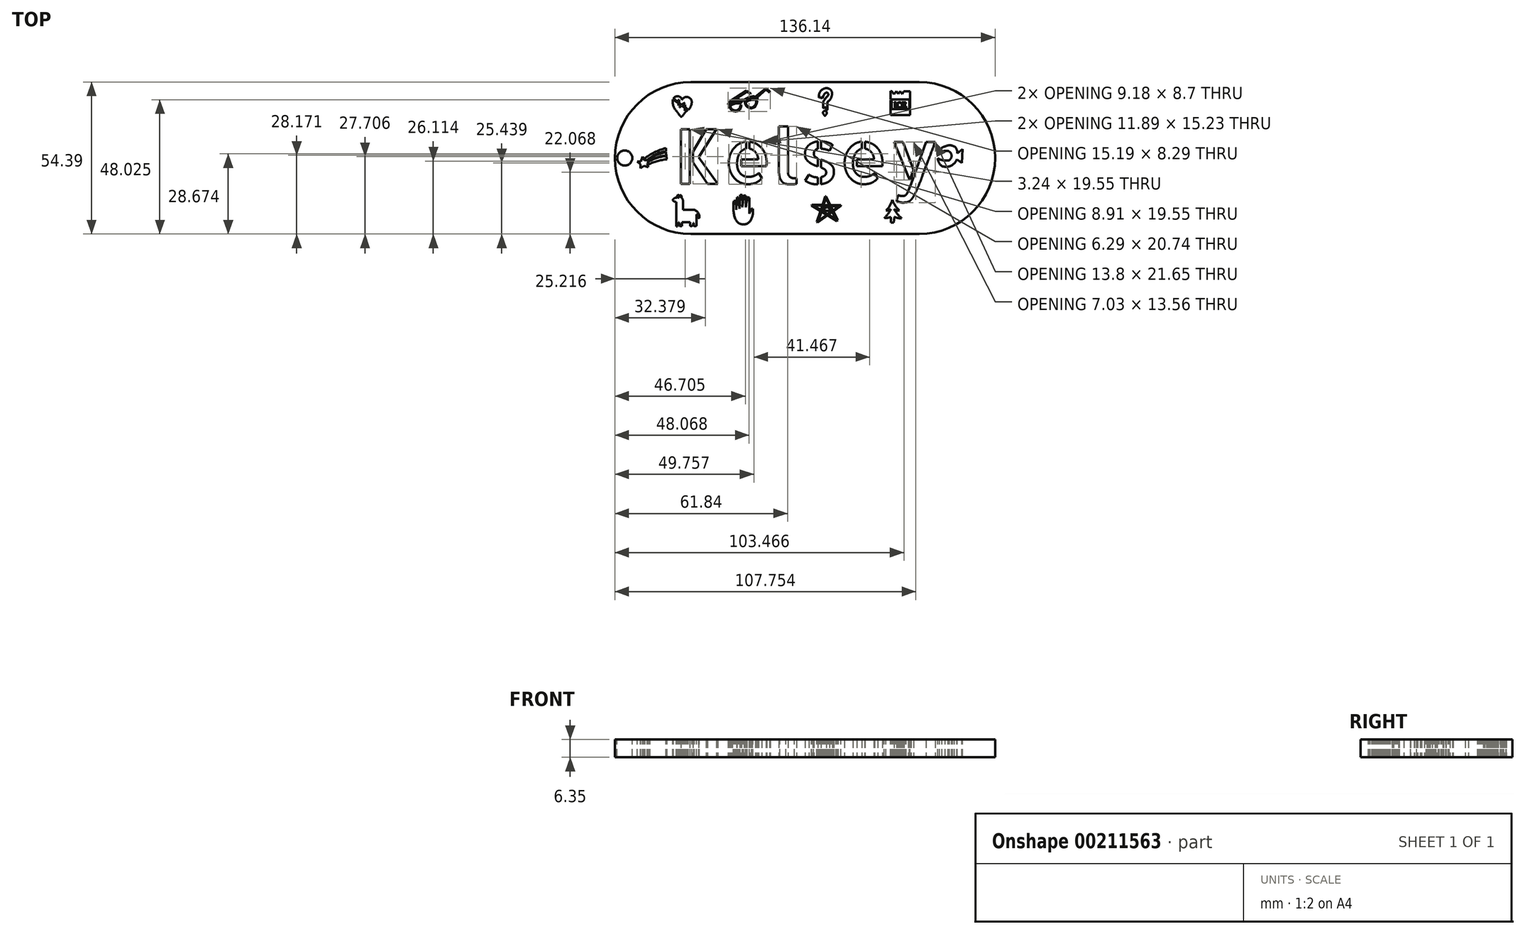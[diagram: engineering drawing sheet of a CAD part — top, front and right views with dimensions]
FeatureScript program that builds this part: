
annotation { "Feature Type Name" : "Feature", "Feature Type Description" : "" }
export const myFeature = defineFeature(function(context is Context, id is Id, definition is map)
    precondition{}
    {
        {
            var Q0;
            Q0=qCreatedBy(makeId("Top.planeOp"),FACE);
            var sketch = newSketch(context, id + "F0", { "sketchPlane" : qUnion([Q0])});
            skLineSegment(sketch, "E0", {"start": v(-66.68, 37.13) * mm, "end": v(15.06, 37.13) * mm});
            skLineSegment(sketch, "E1", {"start": v(15.06, -17.26) * mm, "end": v(-66.68, -17.26) * mm});
            skArc(sketch, "E2", {"start": v(15.06, -17.26) * mm, "mid": v(42.26, 9.93) * mm, "end": v(15.06, 37.13) * mm});
            skArc(sketch, "E3", {"start": v(-66.68, 37.13) * mm, "mid": v(-93.88, 9.93) * mm, "end": v(-66.68, -17.26) * mm});
            skText(sketch, "E4", { "text": "Kelsey", "fontName": "AllertaStencil-Regular.ttf"});
            const initialGuessF0  = {"E4": [-0.07275, 0.00067, 1, 0, 0.01956]};
            skSetInitialGuess(sketch, initialGuessF0);
            skSolve(sketch);
        }
        {
            var Q0;
            Q0=makeQuery(id+"F0.imprint","IMPRINT",FACE,{"disambiguationData":[TD([[makeQuery(id+"F0.imprint","IMPRINT",EDGE,{"derivedFrom":sQuery(id+"F0.wireOp",EDGE,"E0")}),-1.0]])]});
            var sketch = newSketch(context, id + "F1", { "sketchPlane" : qUnion([Q0])});
            skLineSegment(sketch, "E5", {"start": v(-45.3, 32.83) * mm, "end": v(-46.62, 33.7) * mm});
            skLineSegment(sketch, "E6", {"start": v(-46.62, 33.7) * mm, "end": v(-51.86, 30.42) * mm});
            skLineSegment(sketch, "E7", {"start": v(-42.97, 31.66) * mm, "end": v(-39.8, 34.47) * mm});
            skLineSegment(sketch, "E8", {"start": v(-39.8, 34.47) * mm, "end": v(-38.48, 33.25) * mm});
            skLineSegment(sketch, "E9", {"start": v(-38.48, 33.25) * mm, "end": v(-38.22, 33.53) * mm});
            skLineSegment(sketch, "E10", {"start": v(-38.22, 33.53) * mm, "end": v(-39.7, 34.91) * mm});
            skLineSegment(sketch, "E11", {"start": v(-39.7, 34.91) * mm, "end": v(-43.62, 31.93) * mm});
            skLineSegment(sketch, "E12", {"start": v(-45.3, 32.83) * mm, "end": v(-45.17, 33.02) * mm});
            skLineSegment(sketch, "E13", {"start": v(-45.17, 33.02) * mm, "end": v(-46.74, 34.05) * mm});
            skLineSegment(sketch, "E14", {"start": v(-46.74, 34.05) * mm, "end": v(-52.43, 30.37) * mm});
            skArc(sketch, "E15", {"start": v(-48.79, 30.65) * mm, "mid": v(-50.35, 30.92) * mm, "end": v(-51.86, 30.42) * mm});
            skArc(sketch, "E16", {"start": v(-47.64, 30.65) * mm, "mid": v(-48.21, 30.79) * mm, "end": v(-48.79, 30.65) * mm});
            skArc(sketch, "E17", {"start": v(-43.62, 31.93) * mm, "mid": v(-45.78, 31.76) * mm, "end": v(-47.64, 30.65) * mm});
            skArc(sketch, "E18", {"start": v(-42.76, 31.15) * mm, "mid": v(-42.81, 31.43) * mm, "end": v(-42.97, 31.66) * mm});
            skArc(sketch, "E19", {"start": v(-42.97, 31) * mm, "mid": v(-42.82, 31) * mm, "end": v(-42.76, 31.15) * mm});
            skArc(sketch, "E20", {"start": v(-43.62, 28.36) * mm, "mid": v(-43.12, 29.33) * mm, "end": v(-42.93, 30.4) * mm});
            skArc(sketch, "E21", {"start": v(-47.33, 29.92) * mm, "mid": v(-45.98, 27.92) * mm, "end": v(-43.62, 28.36) * mm});
            skArc(sketch, "E22", {"start": v(-47.64, 30.42) * mm, "mid": v(-48.15, 30.48) * mm, "end": v(-48.63, 30.28) * mm});
            skArc(sketch, "E23", {"start": v(-48.54, 29.74) * mm, "mid": v(-48.5, 30.02) * mm, "end": v(-48.63, 30.28) * mm});
            skArc(sketch, "E24", {"start": v(-48.79, 29.74) * mm, "mid": v(-48.66, 29.7) * mm, "end": v(-48.54, 29.74) * mm});
            skArc(sketch, "E25", {"start": v(-49.16, 27.17) * mm, "mid": v(-48.75, 28.02) * mm, "end": v(-48.64, 28.97) * mm});
            skArc(sketch, "E26", {"start": v(-52.24, 27.17) * mm, "mid": v(-50.7, 26.62) * mm, "end": v(-49.16, 27.17) * mm});
            skArc(sketch, "E27", {"start": v(-52.92, 28.67) * mm, "mid": v(-52.72, 27.86) * mm, "end": v(-52.24, 27.17) * mm});
            skArc(sketch, "E28", {"start": v(-52.43, 30.37) * mm, "mid": v(-53.02, 29.83) * mm, "end": v(-53.4, 29.12) * mm});
            skArc(sketch, "E29", {"start": v(-49.04, 29.93) * mm, "mid": v(-51.02, 29.83) * mm, "end": v(-52.82, 29) * mm});
            skArc(sketch, "E30", {"start": v(-49.04, 30.37) * mm, "mid": v(-51.17, 30.39) * mm, "end": v(-53.09, 29.45) * mm});
            skArc(sketch, "E31", {"start": v(-49.04, 29.93) * mm, "mid": v(-48.87, 30.15) * mm, "end": v(-49.04, 30.37) * mm});
            skArc(sketch, "E32", {"start": v(-49.04, 29.5) * mm, "mid": v(-50.88, 29.42) * mm, "end": v(-52.57, 28.67) * mm});
            skArc(sketch, "E33", {"start": v(-50.3, 26.99) * mm, "mid": v(-49.3, 27.71) * mm, "end": v(-48.92, 28.9) * mm});
            skArc(sketch, "E34", {"start": v(-52.57, 28.67) * mm, "mid": v(-51.8, 27.32) * mm, "end": v(-50.3, 26.99) * mm});
            skArc(sketch, "E35", {"start": v(-43.15, 31.48) * mm, "mid": v(-45.32, 31.48) * mm, "end": v(-47.33, 30.65) * mm});
            skArc(sketch, "E36", {"start": v(-43.2, 31.13) * mm, "mid": v(-45.25, 31.05) * mm, "end": v(-47.18, 30.36) * mm});
            skArc(sketch, "E37", {"start": v(-43.2, 31.13) * mm, "mid": v(-43.09, 31.3) * mm, "end": v(-43.15, 31.48) * mm});
            skArc(sketch, "E38", {"start": v(-47.33, 30.65) * mm, "mid": v(-47.35, 30.56) * mm, "end": v(-47.33, 30.47) * mm});
            skArc(sketch, "E39", {"start": v(-43.49, 30.82) * mm, "mid": v(-45.32, 30.67) * mm, "end": v(-47.03, 29.96) * mm});
            skArc(sketch, "E40", {"start": v(-44.66, 28.06) * mm, "mid": v(-43.62, 28.96) * mm, "end": v(-43.35, 30.32) * mm});
            skArc(sketch, "E41", {"start": v(-47.03, 29.96) * mm, "mid": v(-46.3, 28.44) * mm, "end": v(-44.66, 28.06) * mm});
            skLineSegment(sketch, "E42", {"start": v(-52.82, 29) * mm, "end": v(-52.92, 28.67) * mm});
            skLineSegment(sketch, "E43", {"start": v(-53.09, 29.45) * mm, "end": v(-53.4, 29.12) * mm});
            skPoint(sketch, "E44.center.orphan", {"position": v(-52.82, 29.26) * mm});
            skLineSegment(sketch, "E45", {"start": v(-47.33, 29.92) * mm, "end": v(-47.18, 30.36) * mm});
            skLineSegment(sketch, "E46", {"start": v(-47.64, 30.42) * mm, "end": v(-47.33, 30.47) * mm});
            skPoint(sketch, "E46.endSnap0", {"position": v(-47.33, 30.47) * mm});
            skLineSegment(sketch, "E47", {"start": v(-49.04, 29.5) * mm, "end": v(-48.72, 29.5) * mm});
            skLineSegment(sketch, "E48", {"start": v(-48.92, 28.9) * mm, "end": v(-48.64, 28.97) * mm});
            skLineSegment(sketch, "E49", {"start": v(-43.43, 30.66) * mm, "end": v(-42.94, 30.8) * mm});
            skLineSegment(sketch, "E50", {"start": v(-43.35, 30.32) * mm, "end": v(-42.93, 30.4) * mm});
            skArc(sketch, "E51.trimOffspring", {"start": v(-42.94, 30.8) * mm, "mid": v(-42.95, 30.9) * mm, "end": v(-42.97, 31) * mm});
            skArc(sketch, "E52.trimOffspring", {"start": v(-43.43, 30.66) * mm, "mid": v(-43.46, 30.74) * mm, "end": v(-43.49, 30.82) * mm});
            skArc(sketch, "E53.trimOffspring", {"start": v(-48.72, 29.5) * mm, "mid": v(-48.75, 29.63) * mm, "end": v(-48.79, 29.74) * mm});
            skLineSegment(sketch, "E54", {"start": v(-47.33, 30.47) * mm, "end": v(-47.33, 30.47) * mm});
            skSolve(sketch);
        }
        {
            var Q0;
            Q0 = qSketchRegion(id + "F0", true);
            extrude(context, id + "F2", {"entities" : qUnion([Q0]), "depth" : 6.35 * mm});
        }
        {
            var Q0;
            Q0 = qSketchRegion(id + "F1", true);
            extrude(context, id + "F3", {"entities" : qUnion([Q0]), "operationType" : NewBodyOperationType.REMOVE, "endBound" : BoundingType.THROUGH_ALL, "depth" : 25.4 * mm});
        }
        {
            var Q0;
            Q0=makeQuery(id+"F2.opExtrude","CAP_FACE",FACE,{"disambiguationData":[OSD([sQuery(id+"F0.wireOp",EDGE,"E0"),sQuery(id+"F0.wireOp",EDGE,"E1"),sQuery(id+"F0.wireOp",EDGE,"E2"),sQuery(id+"F0.wireOp",EDGE,"E3"),sQuery(id+"F0.wireOp",EDGE,"E4.sketch_text.stroke-0"),sQuery(id+"F0.wireOp",EDGE,"E4.sketch_text.stroke-1"),sQuery(id+"F0.wireOp",EDGE,"E4.sketch_text.stroke-2"),sQuery(id+"F0.wireOp",EDGE,"E4.sketch_text.stroke-3"),sQuery(id+"F0.wireOp",EDGE,"E4.sketch_text.stroke-4"),sQuery(id+"F0.wireOp",EDGE,"E4.sketch_text.stroke-5"),sQuery(id+"F0.wireOp",EDGE,"E4.sketch_text.stroke-6"),sQuery(id+"F0.wireOp",EDGE,"E4.sketch_text.stroke-7"),sQuery(id+"F0.wireOp",EDGE,"E4.sketch_text.stroke-8"),sQuery(id+"F0.wireOp",EDGE,"E4.sketch_text.stroke-9"),sQuery(id+"F0.wireOp",EDGE,"E4.sketch_text.stroke-10"),sQuery(id+"F0.wireOp",EDGE,"E4.sketch_text.stroke-11"),sQuery(id+"F0.wireOp",EDGE,"E4.sketch_text.stroke-12"),sQuery(id+"F0.wireOp",EDGE,"E4.sketch_text.stroke-13"),sQuery(id+"F0.wireOp",EDGE,"E4.sketch_text.stroke-14"),sQuery(id+"F0.wireOp",EDGE,"E4.sketch_text.stroke-15"),sQuery(id+"F0.wireOp",EDGE,"E4.sketch_text.stroke-16"),sQuery(id+"F0.wireOp",EDGE,"E4.sketch_text.stroke-17"),sQuery(id+"F0.wireOp",EDGE,"E4.sketch_text.stroke-18"),sQuery(id+"F0.wireOp",EDGE,"E4.sketch_text.stroke-19"),sQuery(id+"F0.wireOp",EDGE,"E4.sketch_text.stroke-20"),sQuery(id+"F0.wireOp",EDGE,"E4.sketch_text.stroke-21"),sQuery(id+"F0.wireOp",EDGE,"E4.sketch_text.stroke-22"),sQuery(id+"F0.wireOp",EDGE,"E4.sketch_text.stroke-23"),sQuery(id+"F0.wireOp",EDGE,"E4.sketch_text.stroke-24"),sQuery(id+"F0.wireOp",EDGE,"E4.sketch_text.stroke-25"),sQuery(id+"F0.wireOp",EDGE,"E4.sketch_text.stroke-26"),sQuery(id+"F0.wireOp",EDGE,"E4.sketch_text.stroke-27"),sQuery(id+"F0.wireOp",EDGE,"E4.sketch_text.stroke-28"),sQuery(id+"F0.wireOp",EDGE,"E4.sketch_text.stroke-29"),sQuery(id+"F0.wireOp",EDGE,"E4.sketch_text.stroke-30"),sQuery(id+"F0.wireOp",EDGE,"E4.sketch_text.stroke-31"),sQuery(id+"F0.wireOp",EDGE,"E4.sketch_text.stroke-32"),sQuery(id+"F0.wireOp",EDGE,"E4.sketch_text.stroke-33"),sQuery(id+"F0.wireOp",EDGE,"E4.sketch_text.stroke-34"),sQuery(id+"F0.wireOp",EDGE,"E4.sketch_text.stroke-35"),sQuery(id+"F0.wireOp",EDGE,"E4.sketch_text.stroke-36"),sQuery(id+"F0.wireOp",EDGE,"E4.sketch_text.stroke-37"),sQuery(id+"F0.wireOp",EDGE,"E4.sketch_text.stroke-38"),sQuery(id+"F0.wireOp",EDGE,"E4.sketch_text.stroke-39"),sQuery(id+"F0.wireOp",EDGE,"E4.sketch_text.stroke-40"),sQuery(id+"F0.wireOp",EDGE,"E4.sketch_text.stroke-41"),sQuery(id+"F0.wireOp",EDGE,"E4.sketch_text.stroke-42"),sQuery(id+"F0.wireOp",EDGE,"E4.sketch_text.stroke-43"),sQuery(id+"F0.wireOp",EDGE,"E4.sketch_text.stroke-44"),sQuery(id+"F0.wireOp",EDGE,"E4.sketch_text.stroke-45"),sQuery(id+"F0.wireOp",EDGE,"E4.sketch_text.stroke-46"),sQuery(id+"F0.wireOp",EDGE,"E4.sketch_text.stroke-47"),sQuery(id+"F0.wireOp",EDGE,"E4.sketch_text.stroke-48"),sQuery(id+"F0.wireOp",EDGE,"E4.sketch_text.stroke-49"),sQuery(id+"F0.wireOp",EDGE,"E4.sketch_text.stroke-50"),sQuery(id+"F0.wireOp",EDGE,"E4.sketch_text.stroke-51"),sQuery(id+"F0.wireOp",EDGE,"E4.sketch_text.stroke-52"),sQuery(id+"F0.wireOp",EDGE,"E4.sketch_text.stroke-53"),sQuery(id+"F0.wireOp",EDGE,"E4.sketch_text.stroke-54"),sQuery(id+"F0.wireOp",EDGE,"E4.sketch_text.stroke-55"),sQuery(id+"F0.wireOp",EDGE,"E4.sketch_text.stroke-56"),sQuery(id+"F0.wireOp",EDGE,"E4.sketch_text.stroke-57"),sQuery(id+"F0.wireOp",EDGE,"E4.sketch_text.stroke-58"),sQuery(id+"F0.wireOp",EDGE,"E4.sketch_text.stroke-59"),sQuery(id+"F0.wireOp",EDGE,"E4.sketch_text.stroke-60"),sQuery(id+"F0.wireOp",EDGE,"E4.sketch_text.stroke-61"),sQuery(id+"F0.wireOp",EDGE,"E4.sketch_text.stroke-62"),sQuery(id+"F0.wireOp",EDGE,"E4.sketch_text.stroke-63"),sQuery(id+"F0.wireOp",EDGE,"E4.sketch_text.stroke-64"),sQuery(id+"F0.wireOp",EDGE,"E4.sketch_text.stroke-65"),sQuery(id+"F0.wireOp",EDGE,"E4.sketch_text.stroke-66"),sQuery(id+"F0.wireOp",EDGE,"E4.sketch_text.stroke-67"),sQuery(id+"F0.wireOp",EDGE,"E4.sketch_text.stroke-68"),sQuery(id+"F0.wireOp",EDGE,"E4.sketch_text.stroke-69"),sQuery(id+"F0.wireOp",EDGE,"E4.sketch_text.stroke-70"),sQuery(id+"F0.wireOp",EDGE,"E4.sketch_text.stroke-71"),sQuery(id+"F0.wireOp",EDGE,"E4.sketch_text.stroke-72"),sQuery(id+"F0.wireOp",EDGE,"E4.sketch_text.stroke-73"),sQuery(id+"F0.wireOp",EDGE,"E4.sketch_text.stroke-74"),sQuery(id+"F0.wireOp",EDGE,"E4.sketch_text.stroke-75"),sQuery(id+"F0.wireOp",EDGE,"E4.sketch_text.stroke-76"),sQuery(id+"F0.wireOp",EDGE,"E4.sketch_text.stroke-77"),sQuery(id+"F0.wireOp",EDGE,"E4.sketch_text.stroke-78"),sQuery(id+"F0.wireOp",EDGE,"E4.sketch_text.stroke-79"),sQuery(id+"F0.wireOp",EDGE,"E4.sketch_text.stroke-80"),sQuery(id+"F0.wireOp",EDGE,"E4.sketch_text.stroke-81"),sQuery(id+"F0.wireOp",EDGE,"E4.sketch_text.stroke-82"),sQuery(id+"F0.wireOp",EDGE,"E4.sketch_text.stroke-83"),sQuery(id+"F0.wireOp",EDGE,"E4.sketch_text.stroke-84"),sQuery(id+"F0.wireOp",EDGE,"E4.sketch_text.stroke-85"),sQuery(id+"F0.wireOp",EDGE,"E4.sketch_text.stroke-86"),sQuery(id+"F0.wireOp",EDGE,"E4.sketch_text.stroke-87"),sQuery(id+"F0.wireOp",EDGE,"E4.sketch_text.stroke-88"),sQuery(id+"F0.wireOp",EDGE,"E4.sketch_text.stroke-89"),sQuery(id+"F0.wireOp",EDGE,"E4.sketch_text.stroke-90"),sQuery(id+"F0.wireOp",EDGE,"E4.sketch_text.stroke-91"),sQuery(id+"F0.wireOp",EDGE,"E4.sketch_text.stroke-92"),sQuery(id+"F0.wireOp",EDGE,"E4.sketch_text.stroke-93"),sQuery(id+"F0.wireOp",EDGE,"E4.sketch_text.stroke-94"),sQuery(id+"F0.wireOp",EDGE,"E4.sketch_text.stroke-95"),sQuery(id+"F0.wireOp",EDGE,"E4.sketch_text.stroke-96"),sQuery(id+"F0.wireOp",EDGE,"E4.sketch_text.stroke-97"),sQuery(id+"F0.wireOp",EDGE,"E4.sketch_text.stroke-98"),sQuery(id+"F0.wireOp",EDGE,"E4.sketch_text.stroke-99"),sQuery(id+"F0.wireOp",EDGE,"E4.sketch_text.stroke-100"),sQuery(id+"F0.wireOp",EDGE,"E4.sketch_text.stroke-101"),sQuery(id+"F0.wireOp",EDGE,"E4.sketch_text.stroke-102"),sQuery(id+"F0.wireOp",EDGE,"E4.sketch_text.stroke-103"),sQuery(id+"F0.wireOp",EDGE,"E4.sketch_text.stroke-104"),sQuery(id+"F0.wireOp",EDGE,"E4.sketch_text.stroke-105"),sQuery(id+"F0.wireOp",EDGE,"E4.sketch_text.stroke-106"),sQuery(id+"F0.wireOp",EDGE,"E4.sketch_text.stroke-107"),sQuery(id+"F0.wireOp",EDGE,"E4.sketch_text.stroke-108"),sQuery(id+"F0.wireOp",EDGE,"E4.sketch_text.stroke-109"),sQuery(id+"F0.wireOp",EDGE,"E4.sketch_text.stroke-110"),sQuery(id+"F0.wireOp",EDGE,"E4.sketch_text.stroke-111"),sQuery(id+"F0.wireOp",EDGE,"E4.sketch_text.stroke-112"),sQuery(id+"F0.wireOp",EDGE,"E4.sketch_text.stroke-113"),sQuery(id+"F0.wireOp",EDGE,"E4.sketch_text.stroke-114"),sQuery(id+"F0.wireOp",EDGE,"E4.sketch_text.stroke-115"),sQuery(id+"F0.wireOp",EDGE,"E4.sketch_text.stroke-116"),sQuery(id+"F0.wireOp",EDGE,"E4.sketch_text.stroke-117"),sQuery(id+"F0.wireOp",EDGE,"E4.sketch_text.stroke-118"),sQuery(id+"F0.wireOp",EDGE,"E4.sketch_text.stroke-119"),sQuery(id+"F0.wireOp",EDGE,"E4.sketch_text.stroke-120"),sQuery(id+"F0.wireOp",EDGE,"E4.sketch_text.stroke-121"),sQuery(id+"F0.wireOp",EDGE,"E4.sketch_text.stroke-122"),sQuery(id+"F0.wireOp",EDGE,"E4.sketch_text.stroke-123"),sQuery(id+"F0.wireOp",EDGE,"E4.sketch_text.stroke-124"),sQuery(id+"F0.wireOp",EDGE,"E4.sketch_text.stroke-125"),sQuery(id+"F0.wireOp",EDGE,"E4.sketch_text.stroke-126"),sQuery(id+"F0.wireOp",EDGE,"E4.sketch_text.stroke-127"),sQuery(id+"F0.wireOp",EDGE,"E4.sketch_text.stroke-128"),sQuery(id+"F0.wireOp",EDGE,"E4.sketch_text.stroke-129"),sQuery(id+"F0.wireOp",EDGE,"E4.sketch_text.stroke-130"),sQuery(id+"F0.wireOp",EDGE,"E4.sketch_text.stroke-131"),sQuery(id+"F0.wireOp",EDGE,"E4.sketch_text.stroke-132"),sQuery(id+"F0.wireOp",EDGE,"E4.sketch_text.stroke-133"),sQuery(id+"F0.wireOp",EDGE,"E4.sketch_text.stroke-134"),sQuery(id+"F0.wireOp",EDGE,"E4.sketch_text.stroke-135"),sQuery(id+"F0.wireOp",EDGE,"E4.sketch_text.stroke-136"),sQuery(id+"F0.wireOp",EDGE,"E4.sketch_text.stroke-137"),sQuery(id+"F0.wireOp",EDGE,"E4.sketch_text.stroke-138"),sQuery(id+"F0.wireOp",EDGE,"E4.sketch_text.stroke-139"),sQuery(id+"F0.wireOp",EDGE,"E4.sketch_text.stroke-140"),sQuery(id+"F0.wireOp",EDGE,"E4.sketch_text.stroke-141"),sQuery(id+"F0.wireOp",EDGE,"E4.sketch_text.stroke-142"),sQuery(id+"F0.wireOp",EDGE,"E4.sketch_text.stroke-143"),sQuery(id+"F0.wireOp",EDGE,"E4.sketch_text.stroke-144"),sQuery(id+"F0.wireOp",EDGE,"E4.sketch_text.stroke-145"),sQuery(id+"F0.wireOp",EDGE,"E4.sketch_text.stroke-146"),sQuery(id+"F0.wireOp",EDGE,"E4.sketch_text.stroke-147"),sQuery(id+"F0.wireOp",EDGE,"E4.sketch_text.stroke-148"),sQuery(id+"F0.wireOp",EDGE,"E4.sketch_text.stroke-149"),sQuery(id+"F0.wireOp",EDGE,"E4.sketch_text.stroke-150"),sQuery(id+"F0.wireOp",EDGE,"E4.sketch_text.stroke-151"),sQuery(id+"F0.wireOp",EDGE,"E4.sketch_text.stroke-152"),sQuery(id+"F0.wireOp",EDGE,"E4.sketch_text.stroke-153"),sQuery(id+"F0.wireOp",EDGE,"E4.sketch_text.stroke-154"),sQuery(id+"F0.wireOp",EDGE,"E4.sketch_text.stroke-155"),sQuery(id+"F0.wireOp",EDGE,"E4.sketch_text.stroke-156"),sQuery(id+"F0.wireOp",EDGE,"E4.sketch_text.stroke-157"),sQuery(id+"F0.wireOp",EDGE,"E4.sketch_text.stroke-158"),sQuery(id+"F0.wireOp",EDGE,"E4.sketch_text.stroke-159"),sQuery(id+"F0.wireOp",EDGE,"E4.sketch_text.stroke-160"),sQuery(id+"F0.wireOp",EDGE,"E4.sketch_text.stroke-161"),sQuery(id+"F0.wireOp",EDGE,"E4.sketch_text.stroke-162"),sQuery(id+"F0.wireOp",EDGE,"E4.sketch_text.stroke-163"),sQuery(id+"F0.wireOp",EDGE,"E4.sketch_text.stroke-164"),sQuery(id+"F0.wireOp",EDGE,"E4.sketch_text.stroke-165"),sQuery(id+"F0.wireOp",EDGE,"E4.sketch_text.stroke-166"),sQuery(id+"F0.wireOp",EDGE,"E4.sketch_text.stroke-167"),sQuery(id+"F0.wireOp",EDGE,"E4.sketch_text.stroke-168"),sQuery(id+"F0.wireOp",EDGE,"E4.sketch_text.stroke-169"),sQuery(id+"F0.wireOp",EDGE,"E4.sketch_text.stroke-170"),sQuery(id+"F0.wireOp",EDGE,"E4.sketch_text.stroke-171"),sQuery(id+"F0.wireOp",EDGE,"E4.sketch_text.stroke-172"),sQuery(id+"F0.wireOp",EDGE,"E4.sketch_text.stroke-173"),sQuery(id+"F0.wireOp",EDGE,"E4.sketch_text.stroke-174")])],"isStart":false});
            var sketch = newSketch(context, id + "F4", { "sketchPlane" : qUnion([Q0])});
            skArc(sketch, "E55", {"start": v(-18.14, 33.41) * mm, "mid": v(-19.07, 32.53) * mm, "end": v(-19.44, 31.3) * mm});
            skArc(sketch, "E56", {"start": v(-17.69, 32.15) * mm, "mid": v(-17.5, 32.93) * mm, "end": v(-18.14, 33.41) * mm});
            skArc(sketch, "E57", {"start": v(-17.69, 32.15) * mm, "mid": v(-18.57, 31.14) * mm, "end": v(-19.3, 30.01) * mm});
            skArc(sketch, "E58", {"start": v(-17.8, 29.97) * mm, "mid": v(-16.6, 31.21) * mm, "end": v(-16.17, 32.89) * mm});
            skArc(sketch, "E59", {"start": v(-16.17, 32.89) * mm, "mid": v(-16.42, 34.06) * mm, "end": v(-17.36, 34.8) * mm});
            skArc(sketch, "E60", {"start": v(-17.36, 34.8) * mm, "mid": v(-18.92, 34.83) * mm, "end": v(-20.18, 33.93) * mm});
            skArc(sketch, "E61", {"start": v(-20.18, 33.93) * mm, "mid": v(-20.77, 32.8) * mm, "end": v(-20.82, 31.52) * mm});
            skArc(sketch, "E62", {"start": v(-18.03, 26.21) * mm, "mid": v(-18.78, 26.8) * mm, "end": v(-19.39, 26.06) * mm});
            skArc(sketch, "E63", {"start": v(-18.4, 25.51) * mm, "mid": v(-18.07, 25.78) * mm, "end": v(-18.03, 26.21) * mm});
            skArc(sketch, "E64", {"start": v(-19.39, 26.06) * mm, "mid": v(-19.25, 25.72) * mm, "end": v(-18.93, 25.53) * mm});
            skArc(sketch, "E65", {"start": v(-18.93, 25.53) * mm, "mid": v(-18.9, 25.23) * mm, "end": v(-18.69, 25.02) * mm});
            skArc(sketch, "E66", {"start": v(-18.69, 25.02) * mm, "mid": v(-18.44, 25.2) * mm, "end": v(-18.4, 25.51) * mm});
            skLineSegment(sketch, "E67", {"start": v(-17.8, 29.97) * mm, "end": v(-17.8, 27.46) * mm});
            skLineSegment(sketch, "E68", {"start": v(-19.3, 30.01) * mm, "end": v(-19.3, 28.05) * mm});
            skArc(sketch, "E69", {"start": v(-19.8, 31.96) * mm, "mid": v(-19.68, 31.6) * mm, "end": v(-19.44, 31.3) * mm});
            skArc(sketch, "E70", {"start": v(-20.07, 31.3) * mm, "mid": v(-19.85, 31.6) * mm, "end": v(-19.8, 31.96) * mm});
            skArc(sketch, "E71", {"start": v(-20.39, 31.96) * mm, "mid": v(-20.3, 31.6) * mm, "end": v(-20.07, 31.3) * mm});
            skArc(sketch, "E72", {"start": v(-20.82, 31.52) * mm, "mid": v(-20.55, 31.69) * mm, "end": v(-20.39, 31.96) * mm});
            skArc(sketch, "E73", {"start": v(-18.94, 28.2) * mm, "mid": v(-18.86, 28.02) * mm, "end": v(-18.7, 27.9) * mm});
            skArc(sketch, "E74", {"start": v(-18.7, 27.9) * mm, "mid": v(-18.48, 28.15) * mm, "end": v(-18.39, 28.47) * mm});
            skArc(sketch, "E75", {"start": v(-18.39, 28.47) * mm, "mid": v(-18.36, 27.7) * mm, "end": v(-18.06, 27) * mm});
            skArc(sketch, "E76", {"start": v(-18.06, 27) * mm, "mid": v(-17.87, 27.2) * mm, "end": v(-17.8, 27.46) * mm});
            skArc(sketch, "E77", {"start": v(-19.3, 28.05) * mm, "mid": v(-19.27, 27.87) * mm, "end": v(-19.19, 27.7) * mm});
            skArc(sketch, "E78", {"start": v(-19.19, 27.7) * mm, "mid": v(-19.03, 27.94) * mm, "end": v(-18.94, 28.2) * mm});
            skPoint(sketch, "E79", {"position": v(-18.94, 28.2) * mm});
            skSolve(sketch);
        }
        {
            var Q0;
            Q0 = qSketchRegion(id + "F4", true);
            extrude(context, id + "F5", {"entities" : qUnion([Q0]), "operationType" : NewBodyOperationType.REMOVE, "endBound" : BoundingType.THROUGH_ALL, "oppositeDirection" : true, "depth" : 25.4 * mm});
        }
        {
            var Q0;
            Q0=makeQuery(id+"F2.opExtrude","CAP_FACE",FACE,{"disambiguationData":[OSD([sQuery(id+"F0.wireOp",EDGE,"E0"),sQuery(id+"F0.wireOp",EDGE,"E1"),sQuery(id+"F0.wireOp",EDGE,"E2"),sQuery(id+"F0.wireOp",EDGE,"E3"),sQuery(id+"F0.wireOp",EDGE,"E4.sketch_text.stroke-0"),sQuery(id+"F0.wireOp",EDGE,"E4.sketch_text.stroke-1"),sQuery(id+"F0.wireOp",EDGE,"E4.sketch_text.stroke-2"),sQuery(id+"F0.wireOp",EDGE,"E4.sketch_text.stroke-3"),sQuery(id+"F0.wireOp",EDGE,"E4.sketch_text.stroke-4"),sQuery(id+"F0.wireOp",EDGE,"E4.sketch_text.stroke-5"),sQuery(id+"F0.wireOp",EDGE,"E4.sketch_text.stroke-6"),sQuery(id+"F0.wireOp",EDGE,"E4.sketch_text.stroke-7"),sQuery(id+"F0.wireOp",EDGE,"E4.sketch_text.stroke-8"),sQuery(id+"F0.wireOp",EDGE,"E4.sketch_text.stroke-9"),sQuery(id+"F0.wireOp",EDGE,"E4.sketch_text.stroke-10"),sQuery(id+"F0.wireOp",EDGE,"E4.sketch_text.stroke-11"),sQuery(id+"F0.wireOp",EDGE,"E4.sketch_text.stroke-12"),sQuery(id+"F0.wireOp",EDGE,"E4.sketch_text.stroke-13"),sQuery(id+"F0.wireOp",EDGE,"E4.sketch_text.stroke-14"),sQuery(id+"F0.wireOp",EDGE,"E4.sketch_text.stroke-15"),sQuery(id+"F0.wireOp",EDGE,"E4.sketch_text.stroke-16"),sQuery(id+"F0.wireOp",EDGE,"E4.sketch_text.stroke-17"),sQuery(id+"F0.wireOp",EDGE,"E4.sketch_text.stroke-18"),sQuery(id+"F0.wireOp",EDGE,"E4.sketch_text.stroke-19"),sQuery(id+"F0.wireOp",EDGE,"E4.sketch_text.stroke-20"),sQuery(id+"F0.wireOp",EDGE,"E4.sketch_text.stroke-21"),sQuery(id+"F0.wireOp",EDGE,"E4.sketch_text.stroke-22"),sQuery(id+"F0.wireOp",EDGE,"E4.sketch_text.stroke-23"),sQuery(id+"F0.wireOp",EDGE,"E4.sketch_text.stroke-24"),sQuery(id+"F0.wireOp",EDGE,"E4.sketch_text.stroke-25"),sQuery(id+"F0.wireOp",EDGE,"E4.sketch_text.stroke-26"),sQuery(id+"F0.wireOp",EDGE,"E4.sketch_text.stroke-27"),sQuery(id+"F0.wireOp",EDGE,"E4.sketch_text.stroke-28"),sQuery(id+"F0.wireOp",EDGE,"E4.sketch_text.stroke-29"),sQuery(id+"F0.wireOp",EDGE,"E4.sketch_text.stroke-30"),sQuery(id+"F0.wireOp",EDGE,"E4.sketch_text.stroke-31"),sQuery(id+"F0.wireOp",EDGE,"E4.sketch_text.stroke-32"),sQuery(id+"F0.wireOp",EDGE,"E4.sketch_text.stroke-33"),sQuery(id+"F0.wireOp",EDGE,"E4.sketch_text.stroke-34"),sQuery(id+"F0.wireOp",EDGE,"E4.sketch_text.stroke-35"),sQuery(id+"F0.wireOp",EDGE,"E4.sketch_text.stroke-36"),sQuery(id+"F0.wireOp",EDGE,"E4.sketch_text.stroke-37"),sQuery(id+"F0.wireOp",EDGE,"E4.sketch_text.stroke-38"),sQuery(id+"F0.wireOp",EDGE,"E4.sketch_text.stroke-39"),sQuery(id+"F0.wireOp",EDGE,"E4.sketch_text.stroke-40"),sQuery(id+"F0.wireOp",EDGE,"E4.sketch_text.stroke-41"),sQuery(id+"F0.wireOp",EDGE,"E4.sketch_text.stroke-42"),sQuery(id+"F0.wireOp",EDGE,"E4.sketch_text.stroke-43"),sQuery(id+"F0.wireOp",EDGE,"E4.sketch_text.stroke-44"),sQuery(id+"F0.wireOp",EDGE,"E4.sketch_text.stroke-45"),sQuery(id+"F0.wireOp",EDGE,"E4.sketch_text.stroke-46"),sQuery(id+"F0.wireOp",EDGE,"E4.sketch_text.stroke-47"),sQuery(id+"F0.wireOp",EDGE,"E4.sketch_text.stroke-48"),sQuery(id+"F0.wireOp",EDGE,"E4.sketch_text.stroke-49"),sQuery(id+"F0.wireOp",EDGE,"E4.sketch_text.stroke-50"),sQuery(id+"F0.wireOp",EDGE,"E4.sketch_text.stroke-51"),sQuery(id+"F0.wireOp",EDGE,"E4.sketch_text.stroke-52"),sQuery(id+"F0.wireOp",EDGE,"E4.sketch_text.stroke-53"),sQuery(id+"F0.wireOp",EDGE,"E4.sketch_text.stroke-54"),sQuery(id+"F0.wireOp",EDGE,"E4.sketch_text.stroke-55"),sQuery(id+"F0.wireOp",EDGE,"E4.sketch_text.stroke-56"),sQuery(id+"F0.wireOp",EDGE,"E4.sketch_text.stroke-57"),sQuery(id+"F0.wireOp",EDGE,"E4.sketch_text.stroke-58"),sQuery(id+"F0.wireOp",EDGE,"E4.sketch_text.stroke-59"),sQuery(id+"F0.wireOp",EDGE,"E4.sketch_text.stroke-60"),sQuery(id+"F0.wireOp",EDGE,"E4.sketch_text.stroke-61"),sQuery(id+"F0.wireOp",EDGE,"E4.sketch_text.stroke-62"),sQuery(id+"F0.wireOp",EDGE,"E4.sketch_text.stroke-63"),sQuery(id+"F0.wireOp",EDGE,"E4.sketch_text.stroke-64"),sQuery(id+"F0.wireOp",EDGE,"E4.sketch_text.stroke-65"),sQuery(id+"F0.wireOp",EDGE,"E4.sketch_text.stroke-66"),sQuery(id+"F0.wireOp",EDGE,"E4.sketch_text.stroke-67"),sQuery(id+"F0.wireOp",EDGE,"E4.sketch_text.stroke-68"),sQuery(id+"F0.wireOp",EDGE,"E4.sketch_text.stroke-69"),sQuery(id+"F0.wireOp",EDGE,"E4.sketch_text.stroke-70"),sQuery(id+"F0.wireOp",EDGE,"E4.sketch_text.stroke-71"),sQuery(id+"F0.wireOp",EDGE,"E4.sketch_text.stroke-72"),sQuery(id+"F0.wireOp",EDGE,"E4.sketch_text.stroke-73"),sQuery(id+"F0.wireOp",EDGE,"E4.sketch_text.stroke-74"),sQuery(id+"F0.wireOp",EDGE,"E4.sketch_text.stroke-75"),sQuery(id+"F0.wireOp",EDGE,"E4.sketch_text.stroke-76"),sQuery(id+"F0.wireOp",EDGE,"E4.sketch_text.stroke-77"),sQuery(id+"F0.wireOp",EDGE,"E4.sketch_text.stroke-78"),sQuery(id+"F0.wireOp",EDGE,"E4.sketch_text.stroke-79"),sQuery(id+"F0.wireOp",EDGE,"E4.sketch_text.stroke-80"),sQuery(id+"F0.wireOp",EDGE,"E4.sketch_text.stroke-81"),sQuery(id+"F0.wireOp",EDGE,"E4.sketch_text.stroke-82"),sQuery(id+"F0.wireOp",EDGE,"E4.sketch_text.stroke-83"),sQuery(id+"F0.wireOp",EDGE,"E4.sketch_text.stroke-84"),sQuery(id+"F0.wireOp",EDGE,"E4.sketch_text.stroke-85"),sQuery(id+"F0.wireOp",EDGE,"E4.sketch_text.stroke-86"),sQuery(id+"F0.wireOp",EDGE,"E4.sketch_text.stroke-87"),sQuery(id+"F0.wireOp",EDGE,"E4.sketch_text.stroke-88"),sQuery(id+"F0.wireOp",EDGE,"E4.sketch_text.stroke-89"),sQuery(id+"F0.wireOp",EDGE,"E4.sketch_text.stroke-90"),sQuery(id+"F0.wireOp",EDGE,"E4.sketch_text.stroke-91"),sQuery(id+"F0.wireOp",EDGE,"E4.sketch_text.stroke-92"),sQuery(id+"F0.wireOp",EDGE,"E4.sketch_text.stroke-93"),sQuery(id+"F0.wireOp",EDGE,"E4.sketch_text.stroke-94"),sQuery(id+"F0.wireOp",EDGE,"E4.sketch_text.stroke-95"),sQuery(id+"F0.wireOp",EDGE,"E4.sketch_text.stroke-96"),sQuery(id+"F0.wireOp",EDGE,"E4.sketch_text.stroke-97"),sQuery(id+"F0.wireOp",EDGE,"E4.sketch_text.stroke-98"),sQuery(id+"F0.wireOp",EDGE,"E4.sketch_text.stroke-99"),sQuery(id+"F0.wireOp",EDGE,"E4.sketch_text.stroke-100"),sQuery(id+"F0.wireOp",EDGE,"E4.sketch_text.stroke-101"),sQuery(id+"F0.wireOp",EDGE,"E4.sketch_text.stroke-102"),sQuery(id+"F0.wireOp",EDGE,"E4.sketch_text.stroke-103"),sQuery(id+"F0.wireOp",EDGE,"E4.sketch_text.stroke-104"),sQuery(id+"F0.wireOp",EDGE,"E4.sketch_text.stroke-105"),sQuery(id+"F0.wireOp",EDGE,"E4.sketch_text.stroke-106"),sQuery(id+"F0.wireOp",EDGE,"E4.sketch_text.stroke-107"),sQuery(id+"F0.wireOp",EDGE,"E4.sketch_text.stroke-108"),sQuery(id+"F0.wireOp",EDGE,"E4.sketch_text.stroke-109"),sQuery(id+"F0.wireOp",EDGE,"E4.sketch_text.stroke-110"),sQuery(id+"F0.wireOp",EDGE,"E4.sketch_text.stroke-111"),sQuery(id+"F0.wireOp",EDGE,"E4.sketch_text.stroke-112"),sQuery(id+"F0.wireOp",EDGE,"E4.sketch_text.stroke-113"),sQuery(id+"F0.wireOp",EDGE,"E4.sketch_text.stroke-114"),sQuery(id+"F0.wireOp",EDGE,"E4.sketch_text.stroke-115"),sQuery(id+"F0.wireOp",EDGE,"E4.sketch_text.stroke-116"),sQuery(id+"F0.wireOp",EDGE,"E4.sketch_text.stroke-117"),sQuery(id+"F0.wireOp",EDGE,"E4.sketch_text.stroke-118"),sQuery(id+"F0.wireOp",EDGE,"E4.sketch_text.stroke-119"),sQuery(id+"F0.wireOp",EDGE,"E4.sketch_text.stroke-120"),sQuery(id+"F0.wireOp",EDGE,"E4.sketch_text.stroke-121"),sQuery(id+"F0.wireOp",EDGE,"E4.sketch_text.stroke-122"),sQuery(id+"F0.wireOp",EDGE,"E4.sketch_text.stroke-123"),sQuery(id+"F0.wireOp",EDGE,"E4.sketch_text.stroke-124"),sQuery(id+"F0.wireOp",EDGE,"E4.sketch_text.stroke-125"),sQuery(id+"F0.wireOp",EDGE,"E4.sketch_text.stroke-126"),sQuery(id+"F0.wireOp",EDGE,"E4.sketch_text.stroke-127"),sQuery(id+"F0.wireOp",EDGE,"E4.sketch_text.stroke-128"),sQuery(id+"F0.wireOp",EDGE,"E4.sketch_text.stroke-129"),sQuery(id+"F0.wireOp",EDGE,"E4.sketch_text.stroke-130"),sQuery(id+"F0.wireOp",EDGE,"E4.sketch_text.stroke-131"),sQuery(id+"F0.wireOp",EDGE,"E4.sketch_text.stroke-132"),sQuery(id+"F0.wireOp",EDGE,"E4.sketch_text.stroke-133"),sQuery(id+"F0.wireOp",EDGE,"E4.sketch_text.stroke-134"),sQuery(id+"F0.wireOp",EDGE,"E4.sketch_text.stroke-135"),sQuery(id+"F0.wireOp",EDGE,"E4.sketch_text.stroke-136"),sQuery(id+"F0.wireOp",EDGE,"E4.sketch_text.stroke-137"),sQuery(id+"F0.wireOp",EDGE,"E4.sketch_text.stroke-138"),sQuery(id+"F0.wireOp",EDGE,"E4.sketch_text.stroke-139"),sQuery(id+"F0.wireOp",EDGE,"E4.sketch_text.stroke-140"),sQuery(id+"F0.wireOp",EDGE,"E4.sketch_text.stroke-141"),sQuery(id+"F0.wireOp",EDGE,"E4.sketch_text.stroke-142"),sQuery(id+"F0.wireOp",EDGE,"E4.sketch_text.stroke-143"),sQuery(id+"F0.wireOp",EDGE,"E4.sketch_text.stroke-144"),sQuery(id+"F0.wireOp",EDGE,"E4.sketch_text.stroke-145"),sQuery(id+"F0.wireOp",EDGE,"E4.sketch_text.stroke-146"),sQuery(id+"F0.wireOp",EDGE,"E4.sketch_text.stroke-147"),sQuery(id+"F0.wireOp",EDGE,"E4.sketch_text.stroke-148"),sQuery(id+"F0.wireOp",EDGE,"E4.sketch_text.stroke-149"),sQuery(id+"F0.wireOp",EDGE,"E4.sketch_text.stroke-150"),sQuery(id+"F0.wireOp",EDGE,"E4.sketch_text.stroke-151"),sQuery(id+"F0.wireOp",EDGE,"E4.sketch_text.stroke-152"),sQuery(id+"F0.wireOp",EDGE,"E4.sketch_text.stroke-153"),sQuery(id+"F0.wireOp",EDGE,"E4.sketch_text.stroke-154"),sQuery(id+"F0.wireOp",EDGE,"E4.sketch_text.stroke-155"),sQuery(id+"F0.wireOp",EDGE,"E4.sketch_text.stroke-156"),sQuery(id+"F0.wireOp",EDGE,"E4.sketch_text.stroke-157"),sQuery(id+"F0.wireOp",EDGE,"E4.sketch_text.stroke-158"),sQuery(id+"F0.wireOp",EDGE,"E4.sketch_text.stroke-159"),sQuery(id+"F0.wireOp",EDGE,"E4.sketch_text.stroke-160"),sQuery(id+"F0.wireOp",EDGE,"E4.sketch_text.stroke-161"),sQuery(id+"F0.wireOp",EDGE,"E4.sketch_text.stroke-162"),sQuery(id+"F0.wireOp",EDGE,"E4.sketch_text.stroke-163"),sQuery(id+"F0.wireOp",EDGE,"E4.sketch_text.stroke-164"),sQuery(id+"F0.wireOp",EDGE,"E4.sketch_text.stroke-165"),sQuery(id+"F0.wireOp",EDGE,"E4.sketch_text.stroke-166"),sQuery(id+"F0.wireOp",EDGE,"E4.sketch_text.stroke-167"),sQuery(id+"F0.wireOp",EDGE,"E4.sketch_text.stroke-168"),sQuery(id+"F0.wireOp",EDGE,"E4.sketch_text.stroke-169"),sQuery(id+"F0.wireOp",EDGE,"E4.sketch_text.stroke-170"),sQuery(id+"F0.wireOp",EDGE,"E4.sketch_text.stroke-171"),sQuery(id+"F0.wireOp",EDGE,"E4.sketch_text.stroke-172"),sQuery(id+"F0.wireOp",EDGE,"E4.sketch_text.stroke-173"),sQuery(id+"F0.wireOp",EDGE,"E4.sketch_text.stroke-174")])],"isStart":false});
            var sketch = newSketch(context, id + "F6", { "sketchPlane" : qUnion([Q0])});
            skLineSegment(sketch, "E80", {"start": v(5.14, 30.85) * mm, "end": v(11.6, 30.85) * mm});
            skLineSegment(sketch, "E81", {"start": v(11.84, 30.85) * mm, "end": v(11.84, 33.8) * mm});
            skLineSegment(sketch, "E82", {"start": v(11.84, 33.8) * mm, "end": v(9.47, 33.8) * mm});
            skLineSegment(sketch, "E83", {"start": v(9.47, 33.8) * mm, "end": v(9.01, 32.79) * mm});
            skLineSegment(sketch, "E84", {"start": v(9.01, 32.79) * mm, "end": v(8.18, 33.83) * mm});
            skLineSegment(sketch, "E85", {"start": v(8.18, 33.83) * mm, "end": v(7.62, 32.94) * mm});
            skLineSegment(sketch, "E86", {"start": v(7.62, 32.94) * mm, "end": v(6.88, 33.82) * mm});
            skLineSegment(sketch, "E87", {"start": v(6.88, 33.82) * mm, "end": v(6.04, 32.84) * mm});
            skLineSegment(sketch, "E88", {"start": v(6.04, 32.84) * mm, "end": v(5.14, 33.78) * mm});
            skLineSegment(sketch, "E89", {"start": v(5.14, 27.44) * mm, "end": v(5.14, 25.28) * mm});
            skLineSegment(sketch, "E90", {"start": v(5.14, 25.28) * mm, "end": v(11.6, 25.28) * mm});
            skLineSegment(sketch, "E91", {"start": v(11.6, 27.46) * mm, "end": v(5.14, 27.44) * mm});
            skText(sketch, "E92", { "text": "ICE", "fontName": "Tinos-Regular.ttf"});
            skLineSegment(sketch, "E93", {"start": v(5.14, 25.28) * mm, "end": v(4.83, 25.28) * mm});
            skLineSegment(sketch, "E94", {"start": v(4.83, 25.28) * mm, "end": v(4.83, 30.64) * mm});
            skLineSegment(sketch, "E95", {"start": v(4.83, 30.64) * mm, "end": v(5.14, 30.64) * mm});
            skLineSegment(sketch, "E96", {"start": v(5.14, 30.64) * mm, "end": v(5.14, 27.44) * mm});
            skLineSegment(sketch, "E97", {"start": v(5.14, 30.85) * mm, "end": v(4.83, 30.85) * mm});
            skLineSegment(sketch, "E98", {"start": v(4.83, 30.85) * mm, "end": v(4.82, 34) * mm});
            skLineSegment(sketch, "E99", {"start": v(4.82, 34) * mm, "end": v(5.14, 33.78) * mm});
            skLineSegment(sketch, "E100", {"start": v(11.84, 33.8) * mm, "end": v(11.6, 33.8) * mm});
            skLineSegment(sketch, "E101", {"start": v(11.6, 30.85) * mm, "end": v(11.61, 27.68) * mm});
            skLineSegment(sketch, "E102", {"start": v(11.61, 27.68) * mm, "end": v(11.84, 27.68) * mm});
            skLineSegment(sketch, "E103", {"start": v(11.84, 27.68) * mm, "end": v(11.84, 30.85) * mm});
            skLineSegment(sketch, "E104", {"start": v(11.6, 27.46) * mm, "end": v(11.84, 27.46) * mm});
            skLineSegment(sketch, "E105", {"start": v(11.84, 27.46) * mm, "end": v(11.85, 25.28) * mm});
            skLineSegment(sketch, "E106", {"start": v(11.85, 25.28) * mm, "end": v(11.6, 25.28) * mm});
            const initialGuessF6  = {"E92": [0.00594, 0.02796, 1, 0, 0.00205]};
            skSetInitialGuess(sketch, initialGuessF6);
            skSolve(sketch);
        }
        {
            var Q0;
            Q0 = qSketchRegion(id + "F6", true);
            extrude(context, id + "F7", {"entities" : qUnion([Q0]), "operationType" : NewBodyOperationType.REMOVE, "endBound" : BoundingType.THROUGH_ALL, "oppositeDirection" : true, "depth" : 25.4 * mm});
        }
        {
            var Q0;
            Q0=makeQuery(id+"F2.opExtrude","CAP_FACE",FACE,{"disambiguationData":[OSD([sQuery(id+"F0.wireOp",EDGE,"E0"),sQuery(id+"F0.wireOp",EDGE,"E1"),sQuery(id+"F0.wireOp",EDGE,"E2"),sQuery(id+"F0.wireOp",EDGE,"E3"),sQuery(id+"F0.wireOp",EDGE,"E4.sketch_text.stroke-0"),sQuery(id+"F0.wireOp",EDGE,"E4.sketch_text.stroke-1"),sQuery(id+"F0.wireOp",EDGE,"E4.sketch_text.stroke-2"),sQuery(id+"F0.wireOp",EDGE,"E4.sketch_text.stroke-3"),sQuery(id+"F0.wireOp",EDGE,"E4.sketch_text.stroke-4"),sQuery(id+"F0.wireOp",EDGE,"E4.sketch_text.stroke-5"),sQuery(id+"F0.wireOp",EDGE,"E4.sketch_text.stroke-6"),sQuery(id+"F0.wireOp",EDGE,"E4.sketch_text.stroke-7"),sQuery(id+"F0.wireOp",EDGE,"E4.sketch_text.stroke-8"),sQuery(id+"F0.wireOp",EDGE,"E4.sketch_text.stroke-9"),sQuery(id+"F0.wireOp",EDGE,"E4.sketch_text.stroke-10"),sQuery(id+"F0.wireOp",EDGE,"E4.sketch_text.stroke-11"),sQuery(id+"F0.wireOp",EDGE,"E4.sketch_text.stroke-12"),sQuery(id+"F0.wireOp",EDGE,"E4.sketch_text.stroke-13"),sQuery(id+"F0.wireOp",EDGE,"E4.sketch_text.stroke-14"),sQuery(id+"F0.wireOp",EDGE,"E4.sketch_text.stroke-15"),sQuery(id+"F0.wireOp",EDGE,"E4.sketch_text.stroke-16"),sQuery(id+"F0.wireOp",EDGE,"E4.sketch_text.stroke-17"),sQuery(id+"F0.wireOp",EDGE,"E4.sketch_text.stroke-18"),sQuery(id+"F0.wireOp",EDGE,"E4.sketch_text.stroke-19"),sQuery(id+"F0.wireOp",EDGE,"E4.sketch_text.stroke-20"),sQuery(id+"F0.wireOp",EDGE,"E4.sketch_text.stroke-21"),sQuery(id+"F0.wireOp",EDGE,"E4.sketch_text.stroke-22"),sQuery(id+"F0.wireOp",EDGE,"E4.sketch_text.stroke-23"),sQuery(id+"F0.wireOp",EDGE,"E4.sketch_text.stroke-24"),sQuery(id+"F0.wireOp",EDGE,"E4.sketch_text.stroke-25"),sQuery(id+"F0.wireOp",EDGE,"E4.sketch_text.stroke-26"),sQuery(id+"F0.wireOp",EDGE,"E4.sketch_text.stroke-27"),sQuery(id+"F0.wireOp",EDGE,"E4.sketch_text.stroke-28"),sQuery(id+"F0.wireOp",EDGE,"E4.sketch_text.stroke-29"),sQuery(id+"F0.wireOp",EDGE,"E4.sketch_text.stroke-30"),sQuery(id+"F0.wireOp",EDGE,"E4.sketch_text.stroke-31"),sQuery(id+"F0.wireOp",EDGE,"E4.sketch_text.stroke-32"),sQuery(id+"F0.wireOp",EDGE,"E4.sketch_text.stroke-33"),sQuery(id+"F0.wireOp",EDGE,"E4.sketch_text.stroke-34"),sQuery(id+"F0.wireOp",EDGE,"E4.sketch_text.stroke-35"),sQuery(id+"F0.wireOp",EDGE,"E4.sketch_text.stroke-36"),sQuery(id+"F0.wireOp",EDGE,"E4.sketch_text.stroke-37"),sQuery(id+"F0.wireOp",EDGE,"E4.sketch_text.stroke-38"),sQuery(id+"F0.wireOp",EDGE,"E4.sketch_text.stroke-39"),sQuery(id+"F0.wireOp",EDGE,"E4.sketch_text.stroke-40"),sQuery(id+"F0.wireOp",EDGE,"E4.sketch_text.stroke-41"),sQuery(id+"F0.wireOp",EDGE,"E4.sketch_text.stroke-42"),sQuery(id+"F0.wireOp",EDGE,"E4.sketch_text.stroke-43"),sQuery(id+"F0.wireOp",EDGE,"E4.sketch_text.stroke-44"),sQuery(id+"F0.wireOp",EDGE,"E4.sketch_text.stroke-45"),sQuery(id+"F0.wireOp",EDGE,"E4.sketch_text.stroke-46"),sQuery(id+"F0.wireOp",EDGE,"E4.sketch_text.stroke-47"),sQuery(id+"F0.wireOp",EDGE,"E4.sketch_text.stroke-48"),sQuery(id+"F0.wireOp",EDGE,"E4.sketch_text.stroke-49"),sQuery(id+"F0.wireOp",EDGE,"E4.sketch_text.stroke-50"),sQuery(id+"F0.wireOp",EDGE,"E4.sketch_text.stroke-51"),sQuery(id+"F0.wireOp",EDGE,"E4.sketch_text.stroke-52"),sQuery(id+"F0.wireOp",EDGE,"E4.sketch_text.stroke-53"),sQuery(id+"F0.wireOp",EDGE,"E4.sketch_text.stroke-54"),sQuery(id+"F0.wireOp",EDGE,"E4.sketch_text.stroke-55"),sQuery(id+"F0.wireOp",EDGE,"E4.sketch_text.stroke-56"),sQuery(id+"F0.wireOp",EDGE,"E4.sketch_text.stroke-57"),sQuery(id+"F0.wireOp",EDGE,"E4.sketch_text.stroke-58"),sQuery(id+"F0.wireOp",EDGE,"E4.sketch_text.stroke-59"),sQuery(id+"F0.wireOp",EDGE,"E4.sketch_text.stroke-60"),sQuery(id+"F0.wireOp",EDGE,"E4.sketch_text.stroke-61"),sQuery(id+"F0.wireOp",EDGE,"E4.sketch_text.stroke-62"),sQuery(id+"F0.wireOp",EDGE,"E4.sketch_text.stroke-63"),sQuery(id+"F0.wireOp",EDGE,"E4.sketch_text.stroke-64"),sQuery(id+"F0.wireOp",EDGE,"E4.sketch_text.stroke-65"),sQuery(id+"F0.wireOp",EDGE,"E4.sketch_text.stroke-66"),sQuery(id+"F0.wireOp",EDGE,"E4.sketch_text.stroke-67"),sQuery(id+"F0.wireOp",EDGE,"E4.sketch_text.stroke-68"),sQuery(id+"F0.wireOp",EDGE,"E4.sketch_text.stroke-69"),sQuery(id+"F0.wireOp",EDGE,"E4.sketch_text.stroke-70"),sQuery(id+"F0.wireOp",EDGE,"E4.sketch_text.stroke-71"),sQuery(id+"F0.wireOp",EDGE,"E4.sketch_text.stroke-72"),sQuery(id+"F0.wireOp",EDGE,"E4.sketch_text.stroke-73"),sQuery(id+"F0.wireOp",EDGE,"E4.sketch_text.stroke-74"),sQuery(id+"F0.wireOp",EDGE,"E4.sketch_text.stroke-75"),sQuery(id+"F0.wireOp",EDGE,"E4.sketch_text.stroke-76"),sQuery(id+"F0.wireOp",EDGE,"E4.sketch_text.stroke-77"),sQuery(id+"F0.wireOp",EDGE,"E4.sketch_text.stroke-78"),sQuery(id+"F0.wireOp",EDGE,"E4.sketch_text.stroke-79"),sQuery(id+"F0.wireOp",EDGE,"E4.sketch_text.stroke-80"),sQuery(id+"F0.wireOp",EDGE,"E4.sketch_text.stroke-81"),sQuery(id+"F0.wireOp",EDGE,"E4.sketch_text.stroke-82"),sQuery(id+"F0.wireOp",EDGE,"E4.sketch_text.stroke-83"),sQuery(id+"F0.wireOp",EDGE,"E4.sketch_text.stroke-84"),sQuery(id+"F0.wireOp",EDGE,"E4.sketch_text.stroke-85"),sQuery(id+"F0.wireOp",EDGE,"E4.sketch_text.stroke-86"),sQuery(id+"F0.wireOp",EDGE,"E4.sketch_text.stroke-87"),sQuery(id+"F0.wireOp",EDGE,"E4.sketch_text.stroke-88"),sQuery(id+"F0.wireOp",EDGE,"E4.sketch_text.stroke-89"),sQuery(id+"F0.wireOp",EDGE,"E4.sketch_text.stroke-90"),sQuery(id+"F0.wireOp",EDGE,"E4.sketch_text.stroke-91"),sQuery(id+"F0.wireOp",EDGE,"E4.sketch_text.stroke-92"),sQuery(id+"F0.wireOp",EDGE,"E4.sketch_text.stroke-93"),sQuery(id+"F0.wireOp",EDGE,"E4.sketch_text.stroke-94"),sQuery(id+"F0.wireOp",EDGE,"E4.sketch_text.stroke-95"),sQuery(id+"F0.wireOp",EDGE,"E4.sketch_text.stroke-96"),sQuery(id+"F0.wireOp",EDGE,"E4.sketch_text.stroke-97"),sQuery(id+"F0.wireOp",EDGE,"E4.sketch_text.stroke-98"),sQuery(id+"F0.wireOp",EDGE,"E4.sketch_text.stroke-99"),sQuery(id+"F0.wireOp",EDGE,"E4.sketch_text.stroke-100"),sQuery(id+"F0.wireOp",EDGE,"E4.sketch_text.stroke-101"),sQuery(id+"F0.wireOp",EDGE,"E4.sketch_text.stroke-102"),sQuery(id+"F0.wireOp",EDGE,"E4.sketch_text.stroke-103"),sQuery(id+"F0.wireOp",EDGE,"E4.sketch_text.stroke-104"),sQuery(id+"F0.wireOp",EDGE,"E4.sketch_text.stroke-105"),sQuery(id+"F0.wireOp",EDGE,"E4.sketch_text.stroke-106"),sQuery(id+"F0.wireOp",EDGE,"E4.sketch_text.stroke-107"),sQuery(id+"F0.wireOp",EDGE,"E4.sketch_text.stroke-108"),sQuery(id+"F0.wireOp",EDGE,"E4.sketch_text.stroke-109"),sQuery(id+"F0.wireOp",EDGE,"E4.sketch_text.stroke-110"),sQuery(id+"F0.wireOp",EDGE,"E4.sketch_text.stroke-111"),sQuery(id+"F0.wireOp",EDGE,"E4.sketch_text.stroke-112"),sQuery(id+"F0.wireOp",EDGE,"E4.sketch_text.stroke-113"),sQuery(id+"F0.wireOp",EDGE,"E4.sketch_text.stroke-114"),sQuery(id+"F0.wireOp",EDGE,"E4.sketch_text.stroke-115"),sQuery(id+"F0.wireOp",EDGE,"E4.sketch_text.stroke-116"),sQuery(id+"F0.wireOp",EDGE,"E4.sketch_text.stroke-117"),sQuery(id+"F0.wireOp",EDGE,"E4.sketch_text.stroke-118"),sQuery(id+"F0.wireOp",EDGE,"E4.sketch_text.stroke-119"),sQuery(id+"F0.wireOp",EDGE,"E4.sketch_text.stroke-120"),sQuery(id+"F0.wireOp",EDGE,"E4.sketch_text.stroke-121"),sQuery(id+"F0.wireOp",EDGE,"E4.sketch_text.stroke-122"),sQuery(id+"F0.wireOp",EDGE,"E4.sketch_text.stroke-123"),sQuery(id+"F0.wireOp",EDGE,"E4.sketch_text.stroke-124"),sQuery(id+"F0.wireOp",EDGE,"E4.sketch_text.stroke-125"),sQuery(id+"F0.wireOp",EDGE,"E4.sketch_text.stroke-126"),sQuery(id+"F0.wireOp",EDGE,"E4.sketch_text.stroke-127"),sQuery(id+"F0.wireOp",EDGE,"E4.sketch_text.stroke-128"),sQuery(id+"F0.wireOp",EDGE,"E4.sketch_text.stroke-129"),sQuery(id+"F0.wireOp",EDGE,"E4.sketch_text.stroke-130"),sQuery(id+"F0.wireOp",EDGE,"E4.sketch_text.stroke-131"),sQuery(id+"F0.wireOp",EDGE,"E4.sketch_text.stroke-132"),sQuery(id+"F0.wireOp",EDGE,"E4.sketch_text.stroke-133"),sQuery(id+"F0.wireOp",EDGE,"E4.sketch_text.stroke-134"),sQuery(id+"F0.wireOp",EDGE,"E4.sketch_text.stroke-135"),sQuery(id+"F0.wireOp",EDGE,"E4.sketch_text.stroke-136"),sQuery(id+"F0.wireOp",EDGE,"E4.sketch_text.stroke-137"),sQuery(id+"F0.wireOp",EDGE,"E4.sketch_text.stroke-138"),sQuery(id+"F0.wireOp",EDGE,"E4.sketch_text.stroke-139"),sQuery(id+"F0.wireOp",EDGE,"E4.sketch_text.stroke-140"),sQuery(id+"F0.wireOp",EDGE,"E4.sketch_text.stroke-141"),sQuery(id+"F0.wireOp",EDGE,"E4.sketch_text.stroke-142"),sQuery(id+"F0.wireOp",EDGE,"E4.sketch_text.stroke-143"),sQuery(id+"F0.wireOp",EDGE,"E4.sketch_text.stroke-144"),sQuery(id+"F0.wireOp",EDGE,"E4.sketch_text.stroke-145"),sQuery(id+"F0.wireOp",EDGE,"E4.sketch_text.stroke-146"),sQuery(id+"F0.wireOp",EDGE,"E4.sketch_text.stroke-147"),sQuery(id+"F0.wireOp",EDGE,"E4.sketch_text.stroke-148"),sQuery(id+"F0.wireOp",EDGE,"E4.sketch_text.stroke-149"),sQuery(id+"F0.wireOp",EDGE,"E4.sketch_text.stroke-150"),sQuery(id+"F0.wireOp",EDGE,"E4.sketch_text.stroke-151"),sQuery(id+"F0.wireOp",EDGE,"E4.sketch_text.stroke-152"),sQuery(id+"F0.wireOp",EDGE,"E4.sketch_text.stroke-153"),sQuery(id+"F0.wireOp",EDGE,"E4.sketch_text.stroke-154"),sQuery(id+"F0.wireOp",EDGE,"E4.sketch_text.stroke-155"),sQuery(id+"F0.wireOp",EDGE,"E4.sketch_text.stroke-156"),sQuery(id+"F0.wireOp",EDGE,"E4.sketch_text.stroke-157"),sQuery(id+"F0.wireOp",EDGE,"E4.sketch_text.stroke-158"),sQuery(id+"F0.wireOp",EDGE,"E4.sketch_text.stroke-159"),sQuery(id+"F0.wireOp",EDGE,"E4.sketch_text.stroke-160"),sQuery(id+"F0.wireOp",EDGE,"E4.sketch_text.stroke-161"),sQuery(id+"F0.wireOp",EDGE,"E4.sketch_text.stroke-162"),sQuery(id+"F0.wireOp",EDGE,"E4.sketch_text.stroke-163"),sQuery(id+"F0.wireOp",EDGE,"E4.sketch_text.stroke-164"),sQuery(id+"F0.wireOp",EDGE,"E4.sketch_text.stroke-165"),sQuery(id+"F0.wireOp",EDGE,"E4.sketch_text.stroke-166"),sQuery(id+"F0.wireOp",EDGE,"E4.sketch_text.stroke-167"),sQuery(id+"F0.wireOp",EDGE,"E4.sketch_text.stroke-168"),sQuery(id+"F0.wireOp",EDGE,"E4.sketch_text.stroke-169"),sQuery(id+"F0.wireOp",EDGE,"E4.sketch_text.stroke-170"),sQuery(id+"F0.wireOp",EDGE,"E4.sketch_text.stroke-171"),sQuery(id+"F0.wireOp",EDGE,"E4.sketch_text.stroke-172"),sQuery(id+"F0.wireOp",EDGE,"E4.sketch_text.stroke-173"),sQuery(id+"F0.wireOp",EDGE,"E4.sketch_text.stroke-174")])],"isStart":false});
            var sketch = newSketch(context, id + "F8", { "sketchPlane" : qUnion([Q0])});
            skArc(sketch, "E107", {"start": v(-69.84, 30.72) * mm, "mid": v(-71.2, 32.03) * mm, "end": v(-72.92, 31.27) * mm});
            skArc(sketch, "E108", {"start": v(-66.36, 29.79) * mm, "mid": v(-67.7, 31.73) * mm, "end": v(-69.84, 30.72) * mm});
            skArc(sketch, "E109", {"start": v(-68.28, 26.7) * mm, "mid": v(-68.05, 26.84) * mm, "end": v(-67.83, 27) * mm});
            skArc(sketch, "E110", {"start": v(-73.15, 30.09) * mm, "mid": v(-72.83, 28.23) * mm, "end": v(-71.74, 26.7) * mm});
            skArc(sketch, "E111", {"start": v(-71.74, 26.7) * mm, "mid": v(-71.23, 25.94) * mm, "end": v(-70.68, 25.22) * mm});
            skArc(sketch, "E112", {"start": v(-68.28, 26.7) * mm, "mid": v(-68.8, 26.14) * mm, "end": v(-69.27, 25.55) * mm});
            skArc(sketch, "E113", {"start": v(-70.14, 24.68) * mm, "mid": v(-69.63, 25.04) * mm, "end": v(-69.27, 25.55) * mm});
            skArc(sketch, "E114", {"start": v(-70.68, 25.22) * mm, "mid": v(-70.43, 24.94) * mm, "end": v(-70.14, 24.68) * mm});
            skLineSegment(sketch, "E115", {"start": v(-71.97, 30.13) * mm, "end": v(-71.1, 29.47) * mm});
            skLineSegment(sketch, "E116", {"start": v(-71.97, 30.13) * mm, "end": v(-73.07, 30.94) * mm});
            skLineSegment(sketch, "E117", {"start": v(-68.51, 27.95) * mm, "end": v(-68.68, 28.08) * mm});
            skLineSegment(sketch, "E118", {"start": v(-68.51, 27.95) * mm, "end": v(-67.58, 27.22) * mm});
            skLineSegment(sketch, "E119", {"start": v(-68.9, 28.95) * mm, "end": v(-68.9, 28.24) * mm});
            skLineSegment(sketch, "E120", {"start": v(-68.9, 26.8) * mm, "end": v(-68.68, 26.8) * mm});
            skLineSegment(sketch, "E121", {"start": v(-68.68, 26.8) * mm, "end": v(-68.68, 27.65) * mm});
            skLineSegment(sketch, "E122", {"start": v(-68.68, 28.96) * mm, "end": v(-68.9, 28.95) * mm});
            skArc(sketch, "E123", {"start": v(-70.8, 28.05) * mm, "mid": v(-70.37, 28.32) * mm, "end": v(-69.96, 28.61) * mm});
            skArc(sketch, "E124", {"start": v(-68.87, 29.69) * mm, "mid": v(-69.43, 29.4) * mm, "end": v(-69.94, 29.03) * mm});
            skArc(sketch, "E125", {"start": v(-71.14, 28.7) * mm, "mid": v(-71.06, 29.05) * mm, "end": v(-71, 29.4) * mm});
            skArc(sketch, "E126", {"start": v(-71.14, 28.7) * mm, "mid": v(-71.12, 29.1) * mm, "end": v(-71.1, 29.47) * mm});
            skArc(sketch, "E127", {"start": v(-70.9, 30.72) * mm, "mid": v(-71.03, 30.74) * mm, "end": v(-71.13, 30.67) * mm});
            skArc(sketch, "E128.trimOffspring", {"start": v(-73.07, 30.94) * mm, "mid": v(-73.17, 30.52) * mm, "end": v(-73.15, 30.09) * mm});
            skArc(sketch, "E129.trimOffspring", {"start": v(-67.58, 27.22) * mm, "mid": v(-66.73, 28.39) * mm, "end": v(-66.36, 29.79) * mm});
            skLineSegment(sketch, "E130.trimOffspring", {"start": v(-68.68, 27.65) * mm, "end": v(-67.83, 27) * mm});
            skLineSegment(sketch, "E131.trimOffspring", {"start": v(-68.9, 27.82) * mm, "end": v(-68.9, 26.8) * mm});
            skLineSegment(sketch, "E132.trimOffspring", {"start": v(-68.68, 28.08) * mm, "end": v(-68.68, 28.96) * mm});
            skLineSegment(sketch, "E133.trimOffspring", {"start": v(-68.9, 28.24) * mm, "end": v(-69.7, 28.84) * mm});
            skLineSegment(sketch, "E134.trimOffspring", {"start": v(-69.96, 28.61) * mm, "end": v(-68.9, 27.82) * mm});
            skArc(sketch, "E135.trimOffspring", {"start": v(-70.2, 28.8) * mm, "mid": v(-70.52, 28.44) * mm, "end": v(-70.8, 28.05) * mm});
            skLineSegment(sketch, "E136.trimOffspring", {"start": v(-69.94, 29.03) * mm, "end": v(-70.94, 29.78) * mm});
            skArc(sketch, "E137.trimOffspring", {"start": v(-69.7, 28.84) * mm, "mid": v(-69.26, 29.24) * mm, "end": v(-68.87, 29.69) * mm});
            skArc(sketch, "E138.trimOffspring", {"start": v(-71.1, 29.9) * mm, "mid": v(-71.1, 30.28) * mm, "end": v(-71.13, 30.66) * mm});
            skArc(sketch, "E139.trimOffspring", {"start": v(-70.94, 29.78) * mm, "mid": v(-70.9, 30.25) * mm, "end": v(-70.9, 30.72) * mm});
            skLineSegment(sketch, "E140.trimOffspring", {"start": v(-71.1, 29.9) * mm, "end": v(-72.92, 31.27) * mm});
            skLineSegment(sketch, "E141.trimOffspring", {"start": v(-71, 29.4) * mm, "end": v(-70.2, 28.8) * mm});
            skArc(sketch, "E142", {"start": v(-71.13, 30.67) * mm, "mid": v(-71.13, 30.67) * mm, "end": v(-71.13, 30.66) * mm});
            skSolve(sketch);
        }
        {
            var Q0;
            Q0 = qSketchRegion(id + "F8", true);
            extrude(context, id + "F9", {"entities" : qUnion([Q0]), "operationType" : NewBodyOperationType.REMOVE, "endBound" : BoundingType.THROUGH_ALL, "oppositeDirection" : true, "depth" : 25.4 * mm});
        }
        {
            var Q0;
            Q0=makeQuery(id+"F2.opExtrude","CAP_FACE",FACE,{"disambiguationData":[OSD([sQuery(id+"F0.wireOp",EDGE,"E0"),sQuery(id+"F0.wireOp",EDGE,"E1"),sQuery(id+"F0.wireOp",EDGE,"E2"),sQuery(id+"F0.wireOp",EDGE,"E3"),sQuery(id+"F0.wireOp",EDGE,"E4.sketch_text.stroke-0"),sQuery(id+"F0.wireOp",EDGE,"E4.sketch_text.stroke-1"),sQuery(id+"F0.wireOp",EDGE,"E4.sketch_text.stroke-2"),sQuery(id+"F0.wireOp",EDGE,"E4.sketch_text.stroke-3"),sQuery(id+"F0.wireOp",EDGE,"E4.sketch_text.stroke-4"),sQuery(id+"F0.wireOp",EDGE,"E4.sketch_text.stroke-5"),sQuery(id+"F0.wireOp",EDGE,"E4.sketch_text.stroke-6"),sQuery(id+"F0.wireOp",EDGE,"E4.sketch_text.stroke-7"),sQuery(id+"F0.wireOp",EDGE,"E4.sketch_text.stroke-8"),sQuery(id+"F0.wireOp",EDGE,"E4.sketch_text.stroke-9"),sQuery(id+"F0.wireOp",EDGE,"E4.sketch_text.stroke-10"),sQuery(id+"F0.wireOp",EDGE,"E4.sketch_text.stroke-11"),sQuery(id+"F0.wireOp",EDGE,"E4.sketch_text.stroke-12"),sQuery(id+"F0.wireOp",EDGE,"E4.sketch_text.stroke-13"),sQuery(id+"F0.wireOp",EDGE,"E4.sketch_text.stroke-14"),sQuery(id+"F0.wireOp",EDGE,"E4.sketch_text.stroke-15"),sQuery(id+"F0.wireOp",EDGE,"E4.sketch_text.stroke-16"),sQuery(id+"F0.wireOp",EDGE,"E4.sketch_text.stroke-17"),sQuery(id+"F0.wireOp",EDGE,"E4.sketch_text.stroke-18"),sQuery(id+"F0.wireOp",EDGE,"E4.sketch_text.stroke-19"),sQuery(id+"F0.wireOp",EDGE,"E4.sketch_text.stroke-20"),sQuery(id+"F0.wireOp",EDGE,"E4.sketch_text.stroke-21"),sQuery(id+"F0.wireOp",EDGE,"E4.sketch_text.stroke-22"),sQuery(id+"F0.wireOp",EDGE,"E4.sketch_text.stroke-23"),sQuery(id+"F0.wireOp",EDGE,"E4.sketch_text.stroke-24"),sQuery(id+"F0.wireOp",EDGE,"E4.sketch_text.stroke-25"),sQuery(id+"F0.wireOp",EDGE,"E4.sketch_text.stroke-26"),sQuery(id+"F0.wireOp",EDGE,"E4.sketch_text.stroke-27"),sQuery(id+"F0.wireOp",EDGE,"E4.sketch_text.stroke-28"),sQuery(id+"F0.wireOp",EDGE,"E4.sketch_text.stroke-29"),sQuery(id+"F0.wireOp",EDGE,"E4.sketch_text.stroke-30"),sQuery(id+"F0.wireOp",EDGE,"E4.sketch_text.stroke-31"),sQuery(id+"F0.wireOp",EDGE,"E4.sketch_text.stroke-32"),sQuery(id+"F0.wireOp",EDGE,"E4.sketch_text.stroke-33"),sQuery(id+"F0.wireOp",EDGE,"E4.sketch_text.stroke-34"),sQuery(id+"F0.wireOp",EDGE,"E4.sketch_text.stroke-35"),sQuery(id+"F0.wireOp",EDGE,"E4.sketch_text.stroke-36"),sQuery(id+"F0.wireOp",EDGE,"E4.sketch_text.stroke-37"),sQuery(id+"F0.wireOp",EDGE,"E4.sketch_text.stroke-38"),sQuery(id+"F0.wireOp",EDGE,"E4.sketch_text.stroke-39"),sQuery(id+"F0.wireOp",EDGE,"E4.sketch_text.stroke-40"),sQuery(id+"F0.wireOp",EDGE,"E4.sketch_text.stroke-41"),sQuery(id+"F0.wireOp",EDGE,"E4.sketch_text.stroke-42"),sQuery(id+"F0.wireOp",EDGE,"E4.sketch_text.stroke-43"),sQuery(id+"F0.wireOp",EDGE,"E4.sketch_text.stroke-44"),sQuery(id+"F0.wireOp",EDGE,"E4.sketch_text.stroke-45"),sQuery(id+"F0.wireOp",EDGE,"E4.sketch_text.stroke-46"),sQuery(id+"F0.wireOp",EDGE,"E4.sketch_text.stroke-47"),sQuery(id+"F0.wireOp",EDGE,"E4.sketch_text.stroke-48"),sQuery(id+"F0.wireOp",EDGE,"E4.sketch_text.stroke-49"),sQuery(id+"F0.wireOp",EDGE,"E4.sketch_text.stroke-50"),sQuery(id+"F0.wireOp",EDGE,"E4.sketch_text.stroke-51"),sQuery(id+"F0.wireOp",EDGE,"E4.sketch_text.stroke-52"),sQuery(id+"F0.wireOp",EDGE,"E4.sketch_text.stroke-53"),sQuery(id+"F0.wireOp",EDGE,"E4.sketch_text.stroke-54"),sQuery(id+"F0.wireOp",EDGE,"E4.sketch_text.stroke-55"),sQuery(id+"F0.wireOp",EDGE,"E4.sketch_text.stroke-56"),sQuery(id+"F0.wireOp",EDGE,"E4.sketch_text.stroke-57"),sQuery(id+"F0.wireOp",EDGE,"E4.sketch_text.stroke-58"),sQuery(id+"F0.wireOp",EDGE,"E4.sketch_text.stroke-59"),sQuery(id+"F0.wireOp",EDGE,"E4.sketch_text.stroke-60"),sQuery(id+"F0.wireOp",EDGE,"E4.sketch_text.stroke-61"),sQuery(id+"F0.wireOp",EDGE,"E4.sketch_text.stroke-62"),sQuery(id+"F0.wireOp",EDGE,"E4.sketch_text.stroke-63"),sQuery(id+"F0.wireOp",EDGE,"E4.sketch_text.stroke-64"),sQuery(id+"F0.wireOp",EDGE,"E4.sketch_text.stroke-65"),sQuery(id+"F0.wireOp",EDGE,"E4.sketch_text.stroke-66"),sQuery(id+"F0.wireOp",EDGE,"E4.sketch_text.stroke-67"),sQuery(id+"F0.wireOp",EDGE,"E4.sketch_text.stroke-68"),sQuery(id+"F0.wireOp",EDGE,"E4.sketch_text.stroke-69"),sQuery(id+"F0.wireOp",EDGE,"E4.sketch_text.stroke-70"),sQuery(id+"F0.wireOp",EDGE,"E4.sketch_text.stroke-71"),sQuery(id+"F0.wireOp",EDGE,"E4.sketch_text.stroke-72"),sQuery(id+"F0.wireOp",EDGE,"E4.sketch_text.stroke-73"),sQuery(id+"F0.wireOp",EDGE,"E4.sketch_text.stroke-74"),sQuery(id+"F0.wireOp",EDGE,"E4.sketch_text.stroke-75"),sQuery(id+"F0.wireOp",EDGE,"E4.sketch_text.stroke-76"),sQuery(id+"F0.wireOp",EDGE,"E4.sketch_text.stroke-77"),sQuery(id+"F0.wireOp",EDGE,"E4.sketch_text.stroke-78"),sQuery(id+"F0.wireOp",EDGE,"E4.sketch_text.stroke-79"),sQuery(id+"F0.wireOp",EDGE,"E4.sketch_text.stroke-80"),sQuery(id+"F0.wireOp",EDGE,"E4.sketch_text.stroke-81"),sQuery(id+"F0.wireOp",EDGE,"E4.sketch_text.stroke-82"),sQuery(id+"F0.wireOp",EDGE,"E4.sketch_text.stroke-83"),sQuery(id+"F0.wireOp",EDGE,"E4.sketch_text.stroke-84"),sQuery(id+"F0.wireOp",EDGE,"E4.sketch_text.stroke-85"),sQuery(id+"F0.wireOp",EDGE,"E4.sketch_text.stroke-86"),sQuery(id+"F0.wireOp",EDGE,"E4.sketch_text.stroke-87"),sQuery(id+"F0.wireOp",EDGE,"E4.sketch_text.stroke-88"),sQuery(id+"F0.wireOp",EDGE,"E4.sketch_text.stroke-89"),sQuery(id+"F0.wireOp",EDGE,"E4.sketch_text.stroke-90"),sQuery(id+"F0.wireOp",EDGE,"E4.sketch_text.stroke-91"),sQuery(id+"F0.wireOp",EDGE,"E4.sketch_text.stroke-92"),sQuery(id+"F0.wireOp",EDGE,"E4.sketch_text.stroke-93"),sQuery(id+"F0.wireOp",EDGE,"E4.sketch_text.stroke-94"),sQuery(id+"F0.wireOp",EDGE,"E4.sketch_text.stroke-95"),sQuery(id+"F0.wireOp",EDGE,"E4.sketch_text.stroke-96"),sQuery(id+"F0.wireOp",EDGE,"E4.sketch_text.stroke-97"),sQuery(id+"F0.wireOp",EDGE,"E4.sketch_text.stroke-98"),sQuery(id+"F0.wireOp",EDGE,"E4.sketch_text.stroke-99"),sQuery(id+"F0.wireOp",EDGE,"E4.sketch_text.stroke-100"),sQuery(id+"F0.wireOp",EDGE,"E4.sketch_text.stroke-101"),sQuery(id+"F0.wireOp",EDGE,"E4.sketch_text.stroke-102"),sQuery(id+"F0.wireOp",EDGE,"E4.sketch_text.stroke-103"),sQuery(id+"F0.wireOp",EDGE,"E4.sketch_text.stroke-104"),sQuery(id+"F0.wireOp",EDGE,"E4.sketch_text.stroke-105"),sQuery(id+"F0.wireOp",EDGE,"E4.sketch_text.stroke-106"),sQuery(id+"F0.wireOp",EDGE,"E4.sketch_text.stroke-107"),sQuery(id+"F0.wireOp",EDGE,"E4.sketch_text.stroke-108"),sQuery(id+"F0.wireOp",EDGE,"E4.sketch_text.stroke-109"),sQuery(id+"F0.wireOp",EDGE,"E4.sketch_text.stroke-110"),sQuery(id+"F0.wireOp",EDGE,"E4.sketch_text.stroke-111"),sQuery(id+"F0.wireOp",EDGE,"E4.sketch_text.stroke-112"),sQuery(id+"F0.wireOp",EDGE,"E4.sketch_text.stroke-113"),sQuery(id+"F0.wireOp",EDGE,"E4.sketch_text.stroke-114"),sQuery(id+"F0.wireOp",EDGE,"E4.sketch_text.stroke-115"),sQuery(id+"F0.wireOp",EDGE,"E4.sketch_text.stroke-116"),sQuery(id+"F0.wireOp",EDGE,"E4.sketch_text.stroke-117"),sQuery(id+"F0.wireOp",EDGE,"E4.sketch_text.stroke-118"),sQuery(id+"F0.wireOp",EDGE,"E4.sketch_text.stroke-119"),sQuery(id+"F0.wireOp",EDGE,"E4.sketch_text.stroke-120"),sQuery(id+"F0.wireOp",EDGE,"E4.sketch_text.stroke-121"),sQuery(id+"F0.wireOp",EDGE,"E4.sketch_text.stroke-122"),sQuery(id+"F0.wireOp",EDGE,"E4.sketch_text.stroke-123"),sQuery(id+"F0.wireOp",EDGE,"E4.sketch_text.stroke-124"),sQuery(id+"F0.wireOp",EDGE,"E4.sketch_text.stroke-125"),sQuery(id+"F0.wireOp",EDGE,"E4.sketch_text.stroke-126"),sQuery(id+"F0.wireOp",EDGE,"E4.sketch_text.stroke-127"),sQuery(id+"F0.wireOp",EDGE,"E4.sketch_text.stroke-128"),sQuery(id+"F0.wireOp",EDGE,"E4.sketch_text.stroke-129"),sQuery(id+"F0.wireOp",EDGE,"E4.sketch_text.stroke-130"),sQuery(id+"F0.wireOp",EDGE,"E4.sketch_text.stroke-131"),sQuery(id+"F0.wireOp",EDGE,"E4.sketch_text.stroke-132"),sQuery(id+"F0.wireOp",EDGE,"E4.sketch_text.stroke-133"),sQuery(id+"F0.wireOp",EDGE,"E4.sketch_text.stroke-134"),sQuery(id+"F0.wireOp",EDGE,"E4.sketch_text.stroke-135"),sQuery(id+"F0.wireOp",EDGE,"E4.sketch_text.stroke-136"),sQuery(id+"F0.wireOp",EDGE,"E4.sketch_text.stroke-137"),sQuery(id+"F0.wireOp",EDGE,"E4.sketch_text.stroke-138"),sQuery(id+"F0.wireOp",EDGE,"E4.sketch_text.stroke-139"),sQuery(id+"F0.wireOp",EDGE,"E4.sketch_text.stroke-140"),sQuery(id+"F0.wireOp",EDGE,"E4.sketch_text.stroke-141"),sQuery(id+"F0.wireOp",EDGE,"E4.sketch_text.stroke-142"),sQuery(id+"F0.wireOp",EDGE,"E4.sketch_text.stroke-143"),sQuery(id+"F0.wireOp",EDGE,"E4.sketch_text.stroke-144"),sQuery(id+"F0.wireOp",EDGE,"E4.sketch_text.stroke-145"),sQuery(id+"F0.wireOp",EDGE,"E4.sketch_text.stroke-146"),sQuery(id+"F0.wireOp",EDGE,"E4.sketch_text.stroke-147"),sQuery(id+"F0.wireOp",EDGE,"E4.sketch_text.stroke-148"),sQuery(id+"F0.wireOp",EDGE,"E4.sketch_text.stroke-149"),sQuery(id+"F0.wireOp",EDGE,"E4.sketch_text.stroke-150"),sQuery(id+"F0.wireOp",EDGE,"E4.sketch_text.stroke-151"),sQuery(id+"F0.wireOp",EDGE,"E4.sketch_text.stroke-152"),sQuery(id+"F0.wireOp",EDGE,"E4.sketch_text.stroke-153"),sQuery(id+"F0.wireOp",EDGE,"E4.sketch_text.stroke-154"),sQuery(id+"F0.wireOp",EDGE,"E4.sketch_text.stroke-155"),sQuery(id+"F0.wireOp",EDGE,"E4.sketch_text.stroke-156"),sQuery(id+"F0.wireOp",EDGE,"E4.sketch_text.stroke-157"),sQuery(id+"F0.wireOp",EDGE,"E4.sketch_text.stroke-158"),sQuery(id+"F0.wireOp",EDGE,"E4.sketch_text.stroke-159"),sQuery(id+"F0.wireOp",EDGE,"E4.sketch_text.stroke-160"),sQuery(id+"F0.wireOp",EDGE,"E4.sketch_text.stroke-161"),sQuery(id+"F0.wireOp",EDGE,"E4.sketch_text.stroke-162"),sQuery(id+"F0.wireOp",EDGE,"E4.sketch_text.stroke-163"),sQuery(id+"F0.wireOp",EDGE,"E4.sketch_text.stroke-164"),sQuery(id+"F0.wireOp",EDGE,"E4.sketch_text.stroke-165"),sQuery(id+"F0.wireOp",EDGE,"E4.sketch_text.stroke-166"),sQuery(id+"F0.wireOp",EDGE,"E4.sketch_text.stroke-167"),sQuery(id+"F0.wireOp",EDGE,"E4.sketch_text.stroke-168"),sQuery(id+"F0.wireOp",EDGE,"E4.sketch_text.stroke-169"),sQuery(id+"F0.wireOp",EDGE,"E4.sketch_text.stroke-170"),sQuery(id+"F0.wireOp",EDGE,"E4.sketch_text.stroke-171"),sQuery(id+"F0.wireOp",EDGE,"E4.sketch_text.stroke-172"),sQuery(id+"F0.wireOp",EDGE,"E4.sketch_text.stroke-173"),sQuery(id+"F0.wireOp",EDGE,"E4.sketch_text.stroke-174")])],"isStart":false});
            var sketch = newSketch(context, id + "F10", { "sketchPlane" : qUnion([Q0])});
            skArc(sketch, "E143", {"start": v(-75.64, 13.45) * mm, "mid": v(-79.76, 11.92) * mm, "end": v(-83.48, 9.6) * mm});
            skArc(sketch, "E144", {"start": v(-75.59, 12.05) * mm, "mid": v(-78.86, 11.06) * mm, "end": v(-81.88, 9.44) * mm});
            skArc(sketch, "E145", {"start": v(-75.42, 10.68) * mm, "mid": v(-78.48, 10.06) * mm, "end": v(-81.37, 8.87) * mm});
            skArc(sketch, "E146", {"start": v(-75.26, 9.47) * mm, "mid": v(-78.7, 8.83) * mm, "end": v(-81.98, 7.58) * mm});
            skArc(sketch, "E147", {"start": v(-75.64, 13.45) * mm, "mid": v(-75.63, 12.89) * mm, "end": v(-75.6, 12.32) * mm});
            skLineSegment(sketch, "E148", {"start": v(-84, 10.49) * mm, "end": v(-83.18, 9.08) * mm});
            skLineSegment(sketch, "E149", {"start": v(-83.18, 9.08) * mm, "end": v(-81.51, 9.22) * mm});
            skLineSegment(sketch, "E150", {"start": v(-81.51, 9.22) * mm, "end": v(-82.25, 8.03) * mm});
            skLineSegment(sketch, "E151", {"start": v(-82.25, 8.03) * mm, "end": v(-81.87, 6.6) * mm});
            skLineSegment(sketch, "E152", {"start": v(-81.87, 6.6) * mm, "end": v(-83.44, 7.15) * mm});
            skLineSegment(sketch, "E153", {"start": v(-83.44, 7.15) * mm, "end": v(-84.66, 6.22) * mm});
            skLineSegment(sketch, "E154", {"start": v(-84.66, 6.22) * mm, "end": v(-84.7, 7.65) * mm});
            skLineSegment(sketch, "E155", {"start": v(-84.7, 7.65) * mm, "end": v(-85.9, 8.7) * mm});
            skLineSegment(sketch, "E156", {"start": v(-85.9, 8.7) * mm, "end": v(-84.56, 8.7) * mm});
            skLineSegment(sketch, "E157", {"start": v(-84.56, 8.7) * mm, "end": v(-84, 10.49) * mm});
            skArc(sketch, "E158", {"start": v(-75.6, 12.32) * mm, "mid": v(-79.1, 11.3) * mm, "end": v(-82.15, 9.33) * mm});
            skArc(sketch, "E159", {"start": v(-81.88, 9.44) * mm, "mid": v(-82, 9.33) * mm, "end": v(-82.08, 9.18) * mm});
            skArc(sketch, "E160", {"start": v(-81.37, 8.87) * mm, "mid": v(-81.63, 8.76) * mm, "end": v(-81.88, 8.64) * mm});
            skArc(sketch, "E161", {"start": v(-75.47, 10.86) * mm, "mid": v(-78.64, 10.2) * mm, "end": v(-81.61, 8.9) * mm});
            skLineSegment(sketch, "E162", {"start": v(-75.6, 12.32) * mm, "end": v(-75.6, 12.33) * mm});
            skLineSegment(sketch, "E163", {"start": v(-75.6, 12.32) * mm, "end": v(-75.6, 12.32) * mm});
            skPoint(sketch, "E164", {"position": v(-75.43, 10.68) * mm});
            skLineSegment(sketch, "E165", {"start": v(-75.47, 10.86) * mm, "end": v(-75.47, 10.86) * mm});
            skPoint(sketch, "E166.orphan", {"position": v(-83.44, 9.63) * mm});
            skArc(sketch, "E167.trimOffspring", {"start": v(-75.59, 12.05) * mm, "mid": v(-75.54, 11.45) * mm, "end": v(-75.47, 10.86) * mm});
            skArc(sketch, "E168.trimOffspring", {"start": v(-75.45, 10.68) * mm, "mid": v(-75.36, 10.07) * mm, "end": v(-75.26, 9.47) * mm});
            skLineSegment(sketch, "E169", {"start": v(-82.05, 9.27) * mm, "end": v(-81.32, 9.33) * mm});
            skPoint(sketch, "E169.endSnap0", {"position": v(-82, 9.33) * mm});
            skLineSegment(sketch, "E170", {"start": v(-81.32, 9.33) * mm, "end": v(-81.61, 8.9) * mm});
            skLineSegment(sketch, "E171", {"start": v(-83.4, 9.67) * mm, "end": v(-83.09, 9.22) * mm});
            skLineSegment(sketch, "E172", {"start": v(-83.09, 9.22) * mm, "end": v(-82.15, 9.33) * mm});
            skPoint(sketch, "E173.orphan", {"position": v(-82.35, 9.15) * mm});
            skLineSegment(sketch, "E174", {"start": v(-81.77, 8.7) * mm, "end": v(-82.12, 8.08) * mm});
            skLineSegment(sketch, "E175", {"start": v(-82.12, 8.08) * mm, "end": v(-81.98, 7.58) * mm});
            skSolve(sketch);
        }
        {
            var Q0;
            Q0 = qSketchRegion(id + "F10", true);
            extrude(context, id + "F11", {"entities" : qUnion([Q0]), "operationType" : NewBodyOperationType.REMOVE, "endBound" : BoundingType.THROUGH_ALL, "oppositeDirection" : true, "depth" : 25.4 * mm});
        }
        {
            var Q0;
            Q0=makeQuery(id+"F2.opExtrude","CAP_FACE",FACE,{"disambiguationData":[OSD([sQuery(id+"F0.wireOp",EDGE,"E0"),sQuery(id+"F0.wireOp",EDGE,"E1"),sQuery(id+"F0.wireOp",EDGE,"E2"),sQuery(id+"F0.wireOp",EDGE,"E3"),sQuery(id+"F0.wireOp",EDGE,"E4.sketch_text.stroke-0"),sQuery(id+"F0.wireOp",EDGE,"E4.sketch_text.stroke-1"),sQuery(id+"F0.wireOp",EDGE,"E4.sketch_text.stroke-2"),sQuery(id+"F0.wireOp",EDGE,"E4.sketch_text.stroke-3"),sQuery(id+"F0.wireOp",EDGE,"E4.sketch_text.stroke-4"),sQuery(id+"F0.wireOp",EDGE,"E4.sketch_text.stroke-5"),sQuery(id+"F0.wireOp",EDGE,"E4.sketch_text.stroke-6"),sQuery(id+"F0.wireOp",EDGE,"E4.sketch_text.stroke-7"),sQuery(id+"F0.wireOp",EDGE,"E4.sketch_text.stroke-8"),sQuery(id+"F0.wireOp",EDGE,"E4.sketch_text.stroke-9"),sQuery(id+"F0.wireOp",EDGE,"E4.sketch_text.stroke-10"),sQuery(id+"F0.wireOp",EDGE,"E4.sketch_text.stroke-11"),sQuery(id+"F0.wireOp",EDGE,"E4.sketch_text.stroke-12"),sQuery(id+"F0.wireOp",EDGE,"E4.sketch_text.stroke-13"),sQuery(id+"F0.wireOp",EDGE,"E4.sketch_text.stroke-14"),sQuery(id+"F0.wireOp",EDGE,"E4.sketch_text.stroke-15"),sQuery(id+"F0.wireOp",EDGE,"E4.sketch_text.stroke-16"),sQuery(id+"F0.wireOp",EDGE,"E4.sketch_text.stroke-17"),sQuery(id+"F0.wireOp",EDGE,"E4.sketch_text.stroke-18"),sQuery(id+"F0.wireOp",EDGE,"E4.sketch_text.stroke-19"),sQuery(id+"F0.wireOp",EDGE,"E4.sketch_text.stroke-20"),sQuery(id+"F0.wireOp",EDGE,"E4.sketch_text.stroke-21"),sQuery(id+"F0.wireOp",EDGE,"E4.sketch_text.stroke-22"),sQuery(id+"F0.wireOp",EDGE,"E4.sketch_text.stroke-23"),sQuery(id+"F0.wireOp",EDGE,"E4.sketch_text.stroke-24"),sQuery(id+"F0.wireOp",EDGE,"E4.sketch_text.stroke-25"),sQuery(id+"F0.wireOp",EDGE,"E4.sketch_text.stroke-26"),sQuery(id+"F0.wireOp",EDGE,"E4.sketch_text.stroke-27"),sQuery(id+"F0.wireOp",EDGE,"E4.sketch_text.stroke-28"),sQuery(id+"F0.wireOp",EDGE,"E4.sketch_text.stroke-29"),sQuery(id+"F0.wireOp",EDGE,"E4.sketch_text.stroke-30"),sQuery(id+"F0.wireOp",EDGE,"E4.sketch_text.stroke-31"),sQuery(id+"F0.wireOp",EDGE,"E4.sketch_text.stroke-32"),sQuery(id+"F0.wireOp",EDGE,"E4.sketch_text.stroke-33"),sQuery(id+"F0.wireOp",EDGE,"E4.sketch_text.stroke-34"),sQuery(id+"F0.wireOp",EDGE,"E4.sketch_text.stroke-35"),sQuery(id+"F0.wireOp",EDGE,"E4.sketch_text.stroke-36"),sQuery(id+"F0.wireOp",EDGE,"E4.sketch_text.stroke-37"),sQuery(id+"F0.wireOp",EDGE,"E4.sketch_text.stroke-38"),sQuery(id+"F0.wireOp",EDGE,"E4.sketch_text.stroke-39"),sQuery(id+"F0.wireOp",EDGE,"E4.sketch_text.stroke-40"),sQuery(id+"F0.wireOp",EDGE,"E4.sketch_text.stroke-41"),sQuery(id+"F0.wireOp",EDGE,"E4.sketch_text.stroke-42"),sQuery(id+"F0.wireOp",EDGE,"E4.sketch_text.stroke-43"),sQuery(id+"F0.wireOp",EDGE,"E4.sketch_text.stroke-44"),sQuery(id+"F0.wireOp",EDGE,"E4.sketch_text.stroke-45"),sQuery(id+"F0.wireOp",EDGE,"E4.sketch_text.stroke-46"),sQuery(id+"F0.wireOp",EDGE,"E4.sketch_text.stroke-47"),sQuery(id+"F0.wireOp",EDGE,"E4.sketch_text.stroke-48"),sQuery(id+"F0.wireOp",EDGE,"E4.sketch_text.stroke-49"),sQuery(id+"F0.wireOp",EDGE,"E4.sketch_text.stroke-50"),sQuery(id+"F0.wireOp",EDGE,"E4.sketch_text.stroke-51"),sQuery(id+"F0.wireOp",EDGE,"E4.sketch_text.stroke-52"),sQuery(id+"F0.wireOp",EDGE,"E4.sketch_text.stroke-53"),sQuery(id+"F0.wireOp",EDGE,"E4.sketch_text.stroke-54"),sQuery(id+"F0.wireOp",EDGE,"E4.sketch_text.stroke-55"),sQuery(id+"F0.wireOp",EDGE,"E4.sketch_text.stroke-56"),sQuery(id+"F0.wireOp",EDGE,"E4.sketch_text.stroke-57"),sQuery(id+"F0.wireOp",EDGE,"E4.sketch_text.stroke-58"),sQuery(id+"F0.wireOp",EDGE,"E4.sketch_text.stroke-59"),sQuery(id+"F0.wireOp",EDGE,"E4.sketch_text.stroke-60"),sQuery(id+"F0.wireOp",EDGE,"E4.sketch_text.stroke-61"),sQuery(id+"F0.wireOp",EDGE,"E4.sketch_text.stroke-62"),sQuery(id+"F0.wireOp",EDGE,"E4.sketch_text.stroke-63"),sQuery(id+"F0.wireOp",EDGE,"E4.sketch_text.stroke-64"),sQuery(id+"F0.wireOp",EDGE,"E4.sketch_text.stroke-65"),sQuery(id+"F0.wireOp",EDGE,"E4.sketch_text.stroke-66"),sQuery(id+"F0.wireOp",EDGE,"E4.sketch_text.stroke-67"),sQuery(id+"F0.wireOp",EDGE,"E4.sketch_text.stroke-68"),sQuery(id+"F0.wireOp",EDGE,"E4.sketch_text.stroke-69"),sQuery(id+"F0.wireOp",EDGE,"E4.sketch_text.stroke-70"),sQuery(id+"F0.wireOp",EDGE,"E4.sketch_text.stroke-71"),sQuery(id+"F0.wireOp",EDGE,"E4.sketch_text.stroke-72"),sQuery(id+"F0.wireOp",EDGE,"E4.sketch_text.stroke-73"),sQuery(id+"F0.wireOp",EDGE,"E4.sketch_text.stroke-74"),sQuery(id+"F0.wireOp",EDGE,"E4.sketch_text.stroke-75"),sQuery(id+"F0.wireOp",EDGE,"E4.sketch_text.stroke-76"),sQuery(id+"F0.wireOp",EDGE,"E4.sketch_text.stroke-77"),sQuery(id+"F0.wireOp",EDGE,"E4.sketch_text.stroke-78"),sQuery(id+"F0.wireOp",EDGE,"E4.sketch_text.stroke-79"),sQuery(id+"F0.wireOp",EDGE,"E4.sketch_text.stroke-80"),sQuery(id+"F0.wireOp",EDGE,"E4.sketch_text.stroke-81"),sQuery(id+"F0.wireOp",EDGE,"E4.sketch_text.stroke-82"),sQuery(id+"F0.wireOp",EDGE,"E4.sketch_text.stroke-83"),sQuery(id+"F0.wireOp",EDGE,"E4.sketch_text.stroke-84"),sQuery(id+"F0.wireOp",EDGE,"E4.sketch_text.stroke-85"),sQuery(id+"F0.wireOp",EDGE,"E4.sketch_text.stroke-86"),sQuery(id+"F0.wireOp",EDGE,"E4.sketch_text.stroke-87"),sQuery(id+"F0.wireOp",EDGE,"E4.sketch_text.stroke-88"),sQuery(id+"F0.wireOp",EDGE,"E4.sketch_text.stroke-89"),sQuery(id+"F0.wireOp",EDGE,"E4.sketch_text.stroke-90"),sQuery(id+"F0.wireOp",EDGE,"E4.sketch_text.stroke-91"),sQuery(id+"F0.wireOp",EDGE,"E4.sketch_text.stroke-92"),sQuery(id+"F0.wireOp",EDGE,"E4.sketch_text.stroke-93"),sQuery(id+"F0.wireOp",EDGE,"E4.sketch_text.stroke-94"),sQuery(id+"F0.wireOp",EDGE,"E4.sketch_text.stroke-95"),sQuery(id+"F0.wireOp",EDGE,"E4.sketch_text.stroke-96"),sQuery(id+"F0.wireOp",EDGE,"E4.sketch_text.stroke-97"),sQuery(id+"F0.wireOp",EDGE,"E4.sketch_text.stroke-98"),sQuery(id+"F0.wireOp",EDGE,"E4.sketch_text.stroke-99"),sQuery(id+"F0.wireOp",EDGE,"E4.sketch_text.stroke-100"),sQuery(id+"F0.wireOp",EDGE,"E4.sketch_text.stroke-101"),sQuery(id+"F0.wireOp",EDGE,"E4.sketch_text.stroke-102"),sQuery(id+"F0.wireOp",EDGE,"E4.sketch_text.stroke-103"),sQuery(id+"F0.wireOp",EDGE,"E4.sketch_text.stroke-104"),sQuery(id+"F0.wireOp",EDGE,"E4.sketch_text.stroke-105"),sQuery(id+"F0.wireOp",EDGE,"E4.sketch_text.stroke-106"),sQuery(id+"F0.wireOp",EDGE,"E4.sketch_text.stroke-107"),sQuery(id+"F0.wireOp",EDGE,"E4.sketch_text.stroke-108"),sQuery(id+"F0.wireOp",EDGE,"E4.sketch_text.stroke-109"),sQuery(id+"F0.wireOp",EDGE,"E4.sketch_text.stroke-110"),sQuery(id+"F0.wireOp",EDGE,"E4.sketch_text.stroke-111"),sQuery(id+"F0.wireOp",EDGE,"E4.sketch_text.stroke-112"),sQuery(id+"F0.wireOp",EDGE,"E4.sketch_text.stroke-113"),sQuery(id+"F0.wireOp",EDGE,"E4.sketch_text.stroke-114"),sQuery(id+"F0.wireOp",EDGE,"E4.sketch_text.stroke-115"),sQuery(id+"F0.wireOp",EDGE,"E4.sketch_text.stroke-116"),sQuery(id+"F0.wireOp",EDGE,"E4.sketch_text.stroke-117"),sQuery(id+"F0.wireOp",EDGE,"E4.sketch_text.stroke-118"),sQuery(id+"F0.wireOp",EDGE,"E4.sketch_text.stroke-119"),sQuery(id+"F0.wireOp",EDGE,"E4.sketch_text.stroke-120"),sQuery(id+"F0.wireOp",EDGE,"E4.sketch_text.stroke-121"),sQuery(id+"F0.wireOp",EDGE,"E4.sketch_text.stroke-122"),sQuery(id+"F0.wireOp",EDGE,"E4.sketch_text.stroke-123"),sQuery(id+"F0.wireOp",EDGE,"E4.sketch_text.stroke-124"),sQuery(id+"F0.wireOp",EDGE,"E4.sketch_text.stroke-125"),sQuery(id+"F0.wireOp",EDGE,"E4.sketch_text.stroke-126"),sQuery(id+"F0.wireOp",EDGE,"E4.sketch_text.stroke-127"),sQuery(id+"F0.wireOp",EDGE,"E4.sketch_text.stroke-128"),sQuery(id+"F0.wireOp",EDGE,"E4.sketch_text.stroke-129"),sQuery(id+"F0.wireOp",EDGE,"E4.sketch_text.stroke-130"),sQuery(id+"F0.wireOp",EDGE,"E4.sketch_text.stroke-131"),sQuery(id+"F0.wireOp",EDGE,"E4.sketch_text.stroke-132"),sQuery(id+"F0.wireOp",EDGE,"E4.sketch_text.stroke-133"),sQuery(id+"F0.wireOp",EDGE,"E4.sketch_text.stroke-134"),sQuery(id+"F0.wireOp",EDGE,"E4.sketch_text.stroke-135"),sQuery(id+"F0.wireOp",EDGE,"E4.sketch_text.stroke-136"),sQuery(id+"F0.wireOp",EDGE,"E4.sketch_text.stroke-137"),sQuery(id+"F0.wireOp",EDGE,"E4.sketch_text.stroke-138"),sQuery(id+"F0.wireOp",EDGE,"E4.sketch_text.stroke-139"),sQuery(id+"F0.wireOp",EDGE,"E4.sketch_text.stroke-140"),sQuery(id+"F0.wireOp",EDGE,"E4.sketch_text.stroke-141"),sQuery(id+"F0.wireOp",EDGE,"E4.sketch_text.stroke-142"),sQuery(id+"F0.wireOp",EDGE,"E4.sketch_text.stroke-143"),sQuery(id+"F0.wireOp",EDGE,"E4.sketch_text.stroke-144"),sQuery(id+"F0.wireOp",EDGE,"E4.sketch_text.stroke-145"),sQuery(id+"F0.wireOp",EDGE,"E4.sketch_text.stroke-146"),sQuery(id+"F0.wireOp",EDGE,"E4.sketch_text.stroke-147"),sQuery(id+"F0.wireOp",EDGE,"E4.sketch_text.stroke-148"),sQuery(id+"F0.wireOp",EDGE,"E4.sketch_text.stroke-149"),sQuery(id+"F0.wireOp",EDGE,"E4.sketch_text.stroke-150"),sQuery(id+"F0.wireOp",EDGE,"E4.sketch_text.stroke-151"),sQuery(id+"F0.wireOp",EDGE,"E4.sketch_text.stroke-152"),sQuery(id+"F0.wireOp",EDGE,"E4.sketch_text.stroke-153"),sQuery(id+"F0.wireOp",EDGE,"E4.sketch_text.stroke-154"),sQuery(id+"F0.wireOp",EDGE,"E4.sketch_text.stroke-155"),sQuery(id+"F0.wireOp",EDGE,"E4.sketch_text.stroke-156"),sQuery(id+"F0.wireOp",EDGE,"E4.sketch_text.stroke-157"),sQuery(id+"F0.wireOp",EDGE,"E4.sketch_text.stroke-158"),sQuery(id+"F0.wireOp",EDGE,"E4.sketch_text.stroke-159"),sQuery(id+"F0.wireOp",EDGE,"E4.sketch_text.stroke-160"),sQuery(id+"F0.wireOp",EDGE,"E4.sketch_text.stroke-161"),sQuery(id+"F0.wireOp",EDGE,"E4.sketch_text.stroke-162"),sQuery(id+"F0.wireOp",EDGE,"E4.sketch_text.stroke-163"),sQuery(id+"F0.wireOp",EDGE,"E4.sketch_text.stroke-164"),sQuery(id+"F0.wireOp",EDGE,"E4.sketch_text.stroke-165"),sQuery(id+"F0.wireOp",EDGE,"E4.sketch_text.stroke-166"),sQuery(id+"F0.wireOp",EDGE,"E4.sketch_text.stroke-167"),sQuery(id+"F0.wireOp",EDGE,"E4.sketch_text.stroke-168"),sQuery(id+"F0.wireOp",EDGE,"E4.sketch_text.stroke-169"),sQuery(id+"F0.wireOp",EDGE,"E4.sketch_text.stroke-170"),sQuery(id+"F0.wireOp",EDGE,"E4.sketch_text.stroke-171"),sQuery(id+"F0.wireOp",EDGE,"E4.sketch_text.stroke-172"),sQuery(id+"F0.wireOp",EDGE,"E4.sketch_text.stroke-173"),sQuery(id+"F0.wireOp",EDGE,"E4.sketch_text.stroke-174")])],"isStart":false});
            var sketch = newSketch(context, id + "F12", { "sketchPlane" : qUnion([Q0])});
            skLineSegment(sketch, "E176", {"start": v(-71.93, -5.76) * mm, "end": v(-71.93, -14.5) * mm});
            skLineSegment(sketch, "E177", {"start": v(-71.93, -14.5) * mm, "end": v(-71.45, -14.5) * mm});
            skLineSegment(sketch, "E178", {"start": v(-69.52, -8.6) * mm, "end": v(-65.4, -8.6) * mm});
            skLineSegment(sketch, "E179", {"start": v(-69.52, -8.6) * mm, "end": v(-69.52, -5.38) * mm});
            skLineSegment(sketch, "E180", {"start": v(-64.61, -10.2) * mm, "end": v(-64.61, -14.3) * mm});
            skLineSegment(sketch, "E181", {"start": v(-65.73, -13.27) * mm, "end": v(-65.73, -14.32) * mm});
            skLineSegment(sketch, "E182", {"start": v(-66.95, -13.1) * mm, "end": v(-66.95, -14.34) * mm});
            skLineSegment(sketch, "E183", {"start": v(-66.95, -13.1) * mm, "end": v(-69.9, -13.1) * mm});
            skLineSegment(sketch, "E184", {"start": v(-69.9, -13.1) * mm, "end": v(-69.9, -14.39) * mm});
            skLineSegment(sketch, "E185", {"start": v(-71.07, -13.03) * mm, "end": v(-71.45, -14.5) * mm});
            skArc(sketch, "E186", {"start": v(-73.17, -5.1) * mm, "mid": v(-72.66, -5.62) * mm, "end": v(-71.93, -5.76) * mm});
            skArc(sketch, "E187", {"start": v(-71.93, -4.26) * mm, "mid": v(-72.66, -4.5) * mm, "end": v(-73.17, -5.1) * mm});
            skArc(sketch, "E188", {"start": v(-70.93, -4.26) * mm, "mid": v(-71.43, -4.2) * mm, "end": v(-71.93, -4.26) * mm});
            skArc(sketch, "E189", {"start": v(-69.52, -5.38) * mm, "mid": v(-69.66, -4.78) * mm, "end": v(-70.05, -4.3) * mm});
            skArc(sketch, "E190", {"start": v(-70.05, -4.3) * mm, "mid": v(-70.03, -3.88) * mm, "end": v(-70.12, -3.47) * mm});
            skArc(sketch, "E191", {"start": v(-70.44, -3.41) * mm, "mid": v(-70.73, -3.8) * mm, "end": v(-70.93, -4.26) * mm});
            skArc(sketch, "E192", {"start": v(-70.12, -3.47) * mm, "mid": v(-70.27, -3.39) * mm, "end": v(-70.44, -3.41) * mm});
            skArc(sketch, "E193", {"start": v(-71.2, -3.3) * mm, "mid": v(-71.58, -3.64) * mm, "end": v(-71.71, -4.11) * mm});
            skArc(sketch, "E194", {"start": v(-70.93, -3.58) * mm, "mid": v(-71, -3.38) * mm, "end": v(-71.2, -3.3) * mm});
            skArc(sketch, "E195", {"start": v(-70.93, -4.07) * mm, "mid": v(-70.92, -3.83) * mm, "end": v(-70.93, -3.58) * mm});
            skArc(sketch, "E196", {"start": v(-70.93, -4.07) * mm, "mid": v(-71.32, -4.05) * mm, "end": v(-71.71, -4.11) * mm});
            skArc(sketch, "E197", {"start": v(-70.73, -14.36) * mm, "mid": v(-70.32, -14.49) * mm, "end": v(-69.9, -14.39) * mm});
            skArc(sketch, "E198", {"start": v(-70.73, -14.36) * mm, "mid": v(-70.78, -13.66) * mm, "end": v(-71.07, -13.03) * mm});
            skArc(sketch, "E199", {"start": v(-66.25, -14.36) * mm, "mid": v(-65.87, -13.87) * mm, "end": v(-65.73, -13.27) * mm});
            skArc(sketch, "E200", {"start": v(-66.95, -14.34) * mm, "mid": v(-66.6, -14.44) * mm, "end": v(-66.25, -14.36) * mm});
            skArc(sketch, "E201", {"start": v(-65.73, -14.32) * mm, "mid": v(-65.17, -14.5) * mm, "end": v(-64.61, -14.3) * mm});
            skArc(sketch, "E202", {"start": v(-63.93, -11.55) * mm, "mid": v(-64.14, -10.8) * mm, "end": v(-64.61, -10.2) * mm});
            skArc(sketch, "E203", {"start": v(-63.62, -11.55) * mm, "mid": v(-64.03, -9.78) * mm, "end": v(-65.4, -8.6) * mm});
            skArc(sketch, "E204", {"start": v(-63.93, -11.55) * mm, "mid": v(-63.78, -11.6) * mm, "end": v(-63.62, -11.55) * mm});
            skSolve(sketch);
        }
        {
            var Q0;
            Q0 = qSketchRegion(id + "F12", true);
            extrude(context, id + "F13", {"entities" : qUnion([Q0]), "operationType" : NewBodyOperationType.REMOVE, "endBound" : BoundingType.THROUGH_ALL, "oppositeDirection" : true, "depth" : 25.4 * mm});
        }
        {
            var Q0;
            Q0=makeQuery(id+"F2.opExtrude","CAP_FACE",FACE,{"disambiguationData":[OSD([sQuery(id+"F0.wireOp",EDGE,"E0"),sQuery(id+"F0.wireOp",EDGE,"E1"),sQuery(id+"F0.wireOp",EDGE,"E2"),sQuery(id+"F0.wireOp",EDGE,"E3"),sQuery(id+"F0.wireOp",EDGE,"E4.sketch_text.stroke-0"),sQuery(id+"F0.wireOp",EDGE,"E4.sketch_text.stroke-1"),sQuery(id+"F0.wireOp",EDGE,"E4.sketch_text.stroke-2"),sQuery(id+"F0.wireOp",EDGE,"E4.sketch_text.stroke-3"),sQuery(id+"F0.wireOp",EDGE,"E4.sketch_text.stroke-4"),sQuery(id+"F0.wireOp",EDGE,"E4.sketch_text.stroke-5"),sQuery(id+"F0.wireOp",EDGE,"E4.sketch_text.stroke-6"),sQuery(id+"F0.wireOp",EDGE,"E4.sketch_text.stroke-7"),sQuery(id+"F0.wireOp",EDGE,"E4.sketch_text.stroke-8"),sQuery(id+"F0.wireOp",EDGE,"E4.sketch_text.stroke-9"),sQuery(id+"F0.wireOp",EDGE,"E4.sketch_text.stroke-10"),sQuery(id+"F0.wireOp",EDGE,"E4.sketch_text.stroke-11"),sQuery(id+"F0.wireOp",EDGE,"E4.sketch_text.stroke-12"),sQuery(id+"F0.wireOp",EDGE,"E4.sketch_text.stroke-13"),sQuery(id+"F0.wireOp",EDGE,"E4.sketch_text.stroke-14"),sQuery(id+"F0.wireOp",EDGE,"E4.sketch_text.stroke-15"),sQuery(id+"F0.wireOp",EDGE,"E4.sketch_text.stroke-16"),sQuery(id+"F0.wireOp",EDGE,"E4.sketch_text.stroke-17"),sQuery(id+"F0.wireOp",EDGE,"E4.sketch_text.stroke-18"),sQuery(id+"F0.wireOp",EDGE,"E4.sketch_text.stroke-19"),sQuery(id+"F0.wireOp",EDGE,"E4.sketch_text.stroke-20"),sQuery(id+"F0.wireOp",EDGE,"E4.sketch_text.stroke-21"),sQuery(id+"F0.wireOp",EDGE,"E4.sketch_text.stroke-22"),sQuery(id+"F0.wireOp",EDGE,"E4.sketch_text.stroke-23"),sQuery(id+"F0.wireOp",EDGE,"E4.sketch_text.stroke-24"),sQuery(id+"F0.wireOp",EDGE,"E4.sketch_text.stroke-25"),sQuery(id+"F0.wireOp",EDGE,"E4.sketch_text.stroke-26"),sQuery(id+"F0.wireOp",EDGE,"E4.sketch_text.stroke-27"),sQuery(id+"F0.wireOp",EDGE,"E4.sketch_text.stroke-28"),sQuery(id+"F0.wireOp",EDGE,"E4.sketch_text.stroke-29"),sQuery(id+"F0.wireOp",EDGE,"E4.sketch_text.stroke-30"),sQuery(id+"F0.wireOp",EDGE,"E4.sketch_text.stroke-31"),sQuery(id+"F0.wireOp",EDGE,"E4.sketch_text.stroke-32"),sQuery(id+"F0.wireOp",EDGE,"E4.sketch_text.stroke-33"),sQuery(id+"F0.wireOp",EDGE,"E4.sketch_text.stroke-34"),sQuery(id+"F0.wireOp",EDGE,"E4.sketch_text.stroke-35"),sQuery(id+"F0.wireOp",EDGE,"E4.sketch_text.stroke-36"),sQuery(id+"F0.wireOp",EDGE,"E4.sketch_text.stroke-37"),sQuery(id+"F0.wireOp",EDGE,"E4.sketch_text.stroke-38"),sQuery(id+"F0.wireOp",EDGE,"E4.sketch_text.stroke-39"),sQuery(id+"F0.wireOp",EDGE,"E4.sketch_text.stroke-40"),sQuery(id+"F0.wireOp",EDGE,"E4.sketch_text.stroke-41"),sQuery(id+"F0.wireOp",EDGE,"E4.sketch_text.stroke-42"),sQuery(id+"F0.wireOp",EDGE,"E4.sketch_text.stroke-43"),sQuery(id+"F0.wireOp",EDGE,"E4.sketch_text.stroke-44"),sQuery(id+"F0.wireOp",EDGE,"E4.sketch_text.stroke-45"),sQuery(id+"F0.wireOp",EDGE,"E4.sketch_text.stroke-46"),sQuery(id+"F0.wireOp",EDGE,"E4.sketch_text.stroke-47"),sQuery(id+"F0.wireOp",EDGE,"E4.sketch_text.stroke-48"),sQuery(id+"F0.wireOp",EDGE,"E4.sketch_text.stroke-49"),sQuery(id+"F0.wireOp",EDGE,"E4.sketch_text.stroke-50"),sQuery(id+"F0.wireOp",EDGE,"E4.sketch_text.stroke-51"),sQuery(id+"F0.wireOp",EDGE,"E4.sketch_text.stroke-52"),sQuery(id+"F0.wireOp",EDGE,"E4.sketch_text.stroke-53"),sQuery(id+"F0.wireOp",EDGE,"E4.sketch_text.stroke-54"),sQuery(id+"F0.wireOp",EDGE,"E4.sketch_text.stroke-55"),sQuery(id+"F0.wireOp",EDGE,"E4.sketch_text.stroke-56"),sQuery(id+"F0.wireOp",EDGE,"E4.sketch_text.stroke-57"),sQuery(id+"F0.wireOp",EDGE,"E4.sketch_text.stroke-58"),sQuery(id+"F0.wireOp",EDGE,"E4.sketch_text.stroke-59"),sQuery(id+"F0.wireOp",EDGE,"E4.sketch_text.stroke-60"),sQuery(id+"F0.wireOp",EDGE,"E4.sketch_text.stroke-61"),sQuery(id+"F0.wireOp",EDGE,"E4.sketch_text.stroke-62"),sQuery(id+"F0.wireOp",EDGE,"E4.sketch_text.stroke-63"),sQuery(id+"F0.wireOp",EDGE,"E4.sketch_text.stroke-64"),sQuery(id+"F0.wireOp",EDGE,"E4.sketch_text.stroke-65"),sQuery(id+"F0.wireOp",EDGE,"E4.sketch_text.stroke-66"),sQuery(id+"F0.wireOp",EDGE,"E4.sketch_text.stroke-67"),sQuery(id+"F0.wireOp",EDGE,"E4.sketch_text.stroke-68"),sQuery(id+"F0.wireOp",EDGE,"E4.sketch_text.stroke-69"),sQuery(id+"F0.wireOp",EDGE,"E4.sketch_text.stroke-70"),sQuery(id+"F0.wireOp",EDGE,"E4.sketch_text.stroke-71"),sQuery(id+"F0.wireOp",EDGE,"E4.sketch_text.stroke-72"),sQuery(id+"F0.wireOp",EDGE,"E4.sketch_text.stroke-73"),sQuery(id+"F0.wireOp",EDGE,"E4.sketch_text.stroke-74"),sQuery(id+"F0.wireOp",EDGE,"E4.sketch_text.stroke-75"),sQuery(id+"F0.wireOp",EDGE,"E4.sketch_text.stroke-76"),sQuery(id+"F0.wireOp",EDGE,"E4.sketch_text.stroke-77"),sQuery(id+"F0.wireOp",EDGE,"E4.sketch_text.stroke-78"),sQuery(id+"F0.wireOp",EDGE,"E4.sketch_text.stroke-79"),sQuery(id+"F0.wireOp",EDGE,"E4.sketch_text.stroke-80"),sQuery(id+"F0.wireOp",EDGE,"E4.sketch_text.stroke-81"),sQuery(id+"F0.wireOp",EDGE,"E4.sketch_text.stroke-82"),sQuery(id+"F0.wireOp",EDGE,"E4.sketch_text.stroke-83"),sQuery(id+"F0.wireOp",EDGE,"E4.sketch_text.stroke-84"),sQuery(id+"F0.wireOp",EDGE,"E4.sketch_text.stroke-85"),sQuery(id+"F0.wireOp",EDGE,"E4.sketch_text.stroke-86"),sQuery(id+"F0.wireOp",EDGE,"E4.sketch_text.stroke-87"),sQuery(id+"F0.wireOp",EDGE,"E4.sketch_text.stroke-88"),sQuery(id+"F0.wireOp",EDGE,"E4.sketch_text.stroke-89"),sQuery(id+"F0.wireOp",EDGE,"E4.sketch_text.stroke-90"),sQuery(id+"F0.wireOp",EDGE,"E4.sketch_text.stroke-91"),sQuery(id+"F0.wireOp",EDGE,"E4.sketch_text.stroke-92"),sQuery(id+"F0.wireOp",EDGE,"E4.sketch_text.stroke-93"),sQuery(id+"F0.wireOp",EDGE,"E4.sketch_text.stroke-94"),sQuery(id+"F0.wireOp",EDGE,"E4.sketch_text.stroke-95"),sQuery(id+"F0.wireOp",EDGE,"E4.sketch_text.stroke-96"),sQuery(id+"F0.wireOp",EDGE,"E4.sketch_text.stroke-97"),sQuery(id+"F0.wireOp",EDGE,"E4.sketch_text.stroke-98"),sQuery(id+"F0.wireOp",EDGE,"E4.sketch_text.stroke-99"),sQuery(id+"F0.wireOp",EDGE,"E4.sketch_text.stroke-100"),sQuery(id+"F0.wireOp",EDGE,"E4.sketch_text.stroke-101"),sQuery(id+"F0.wireOp",EDGE,"E4.sketch_text.stroke-102"),sQuery(id+"F0.wireOp",EDGE,"E4.sketch_text.stroke-103"),sQuery(id+"F0.wireOp",EDGE,"E4.sketch_text.stroke-104"),sQuery(id+"F0.wireOp",EDGE,"E4.sketch_text.stroke-105"),sQuery(id+"F0.wireOp",EDGE,"E4.sketch_text.stroke-106"),sQuery(id+"F0.wireOp",EDGE,"E4.sketch_text.stroke-107"),sQuery(id+"F0.wireOp",EDGE,"E4.sketch_text.stroke-108"),sQuery(id+"F0.wireOp",EDGE,"E4.sketch_text.stroke-109"),sQuery(id+"F0.wireOp",EDGE,"E4.sketch_text.stroke-110"),sQuery(id+"F0.wireOp",EDGE,"E4.sketch_text.stroke-111"),sQuery(id+"F0.wireOp",EDGE,"E4.sketch_text.stroke-112"),sQuery(id+"F0.wireOp",EDGE,"E4.sketch_text.stroke-113"),sQuery(id+"F0.wireOp",EDGE,"E4.sketch_text.stroke-114"),sQuery(id+"F0.wireOp",EDGE,"E4.sketch_text.stroke-115"),sQuery(id+"F0.wireOp",EDGE,"E4.sketch_text.stroke-116"),sQuery(id+"F0.wireOp",EDGE,"E4.sketch_text.stroke-117"),sQuery(id+"F0.wireOp",EDGE,"E4.sketch_text.stroke-118"),sQuery(id+"F0.wireOp",EDGE,"E4.sketch_text.stroke-119"),sQuery(id+"F0.wireOp",EDGE,"E4.sketch_text.stroke-120"),sQuery(id+"F0.wireOp",EDGE,"E4.sketch_text.stroke-121"),sQuery(id+"F0.wireOp",EDGE,"E4.sketch_text.stroke-122"),sQuery(id+"F0.wireOp",EDGE,"E4.sketch_text.stroke-123"),sQuery(id+"F0.wireOp",EDGE,"E4.sketch_text.stroke-124"),sQuery(id+"F0.wireOp",EDGE,"E4.sketch_text.stroke-125"),sQuery(id+"F0.wireOp",EDGE,"E4.sketch_text.stroke-126"),sQuery(id+"F0.wireOp",EDGE,"E4.sketch_text.stroke-127"),sQuery(id+"F0.wireOp",EDGE,"E4.sketch_text.stroke-128"),sQuery(id+"F0.wireOp",EDGE,"E4.sketch_text.stroke-129"),sQuery(id+"F0.wireOp",EDGE,"E4.sketch_text.stroke-130"),sQuery(id+"F0.wireOp",EDGE,"E4.sketch_text.stroke-131"),sQuery(id+"F0.wireOp",EDGE,"E4.sketch_text.stroke-132"),sQuery(id+"F0.wireOp",EDGE,"E4.sketch_text.stroke-133"),sQuery(id+"F0.wireOp",EDGE,"E4.sketch_text.stroke-134"),sQuery(id+"F0.wireOp",EDGE,"E4.sketch_text.stroke-135"),sQuery(id+"F0.wireOp",EDGE,"E4.sketch_text.stroke-136"),sQuery(id+"F0.wireOp",EDGE,"E4.sketch_text.stroke-137"),sQuery(id+"F0.wireOp",EDGE,"E4.sketch_text.stroke-138"),sQuery(id+"F0.wireOp",EDGE,"E4.sketch_text.stroke-139"),sQuery(id+"F0.wireOp",EDGE,"E4.sketch_text.stroke-140"),sQuery(id+"F0.wireOp",EDGE,"E4.sketch_text.stroke-141"),sQuery(id+"F0.wireOp",EDGE,"E4.sketch_text.stroke-142"),sQuery(id+"F0.wireOp",EDGE,"E4.sketch_text.stroke-143"),sQuery(id+"F0.wireOp",EDGE,"E4.sketch_text.stroke-144"),sQuery(id+"F0.wireOp",EDGE,"E4.sketch_text.stroke-145"),sQuery(id+"F0.wireOp",EDGE,"E4.sketch_text.stroke-146"),sQuery(id+"F0.wireOp",EDGE,"E4.sketch_text.stroke-147"),sQuery(id+"F0.wireOp",EDGE,"E4.sketch_text.stroke-148"),sQuery(id+"F0.wireOp",EDGE,"E4.sketch_text.stroke-149"),sQuery(id+"F0.wireOp",EDGE,"E4.sketch_text.stroke-150"),sQuery(id+"F0.wireOp",EDGE,"E4.sketch_text.stroke-151"),sQuery(id+"F0.wireOp",EDGE,"E4.sketch_text.stroke-152"),sQuery(id+"F0.wireOp",EDGE,"E4.sketch_text.stroke-153"),sQuery(id+"F0.wireOp",EDGE,"E4.sketch_text.stroke-154"),sQuery(id+"F0.wireOp",EDGE,"E4.sketch_text.stroke-155"),sQuery(id+"F0.wireOp",EDGE,"E4.sketch_text.stroke-156"),sQuery(id+"F0.wireOp",EDGE,"E4.sketch_text.stroke-157"),sQuery(id+"F0.wireOp",EDGE,"E4.sketch_text.stroke-158"),sQuery(id+"F0.wireOp",EDGE,"E4.sketch_text.stroke-159"),sQuery(id+"F0.wireOp",EDGE,"E4.sketch_text.stroke-160"),sQuery(id+"F0.wireOp",EDGE,"E4.sketch_text.stroke-161"),sQuery(id+"F0.wireOp",EDGE,"E4.sketch_text.stroke-162"),sQuery(id+"F0.wireOp",EDGE,"E4.sketch_text.stroke-163"),sQuery(id+"F0.wireOp",EDGE,"E4.sketch_text.stroke-164"),sQuery(id+"F0.wireOp",EDGE,"E4.sketch_text.stroke-165"),sQuery(id+"F0.wireOp",EDGE,"E4.sketch_text.stroke-166"),sQuery(id+"F0.wireOp",EDGE,"E4.sketch_text.stroke-167"),sQuery(id+"F0.wireOp",EDGE,"E4.sketch_text.stroke-168"),sQuery(id+"F0.wireOp",EDGE,"E4.sketch_text.stroke-169"),sQuery(id+"F0.wireOp",EDGE,"E4.sketch_text.stroke-170"),sQuery(id+"F0.wireOp",EDGE,"E4.sketch_text.stroke-171"),sQuery(id+"F0.wireOp",EDGE,"E4.sketch_text.stroke-172"),sQuery(id+"F0.wireOp",EDGE,"E4.sketch_text.stroke-173"),sQuery(id+"F0.wireOp",EDGE,"E4.sketch_text.stroke-174")])],"isStart":false});
            var sketch = newSketch(context, id + "F14", { "sketchPlane" : qUnion([Q0])});
            skArc(sketch, "E205", {"start": v(-51.26, -5.38) * mm, "mid": v(-51.47, -8.64) * mm, "end": v(-50.78, -11.83) * mm});
            skArc(sketch, "E206", {"start": v(-50.78, -11.83) * mm, "mid": v(-49.8, -13.15) * mm, "end": v(-48.3, -13.83) * mm});
            skArc(sketch, "E207", {"start": v(-48.3, -13.83) * mm, "mid": v(-46.3, -13.41) * mm, "end": v(-45.02, -11.83) * mm});
            skArc(sketch, "E208", {"start": v(-45.02, -11.83) * mm, "mid": v(-44.49, -10.09) * mm, "end": v(-44.54, -8.27) * mm});
            skArc(sketch, "E209", {"start": v(-49.32, -8.27) * mm, "mid": v(-49.42, -6.23) * mm, "end": v(-49.62, -4.19) * mm});
            skArc(sketch, "E210", {"start": v(-49.32, -8.27) * mm, "mid": v(-49.13, -5.79) * mm, "end": v(-48.99, -3.3) * mm});
            skArc(sketch, "E211", {"start": v(-48.3, -7.76) * mm, "mid": v(-48.17, -5.54) * mm, "end": v(-48.28, -3.32) * mm});
            skArc(sketch, "E212", {"start": v(-48.3, -7.76) * mm, "mid": v(-48, -5.6) * mm, "end": v(-47.72, -3.42) * mm});
            skArc(sketch, "E213", {"start": v(-47.04, -7.76) * mm, "mid": v(-46.94, -5.67) * mm, "end": v(-47.07, -3.58) * mm});
            skArc(sketch, "E214", {"start": v(-46.44, -4.06) * mm, "mid": v(-46.75, -5.91) * mm, "end": v(-47.04, -7.76) * mm});
            skArc(sketch, "E215", {"start": v(-45.73, -10.02) * mm, "mid": v(-45.7, -7.13) * mm, "end": v(-45.78, -4.24) * mm});
            skArc(sketch, "E216", {"start": v(-45.73, -10.02) * mm, "mid": v(-45.36, -9.15) * mm, "end": v(-45.02, -8.27) * mm});
            skArc(sketch, "E217", {"start": v(-50.2, -4.19) * mm, "mid": v(-50.33, -6.4) * mm, "end": v(-50.45, -8.6) * mm});
            skArc(sketch, "E218", {"start": v(-50.45, -8.6) * mm, "mid": v(-50.49, -6.98) * mm, "end": v(-50.68, -5.38) * mm});
            skLineSegment(sketch, "E219", {"start": v(-51.26, -5.38) * mm, "end": v(-50.68, -5.38) * mm});
            skLineSegment(sketch, "E220", {"start": v(-50.2, -4.19) * mm, "end": v(-49.62, -4.19) * mm});
            skLineSegment(sketch, "E221", {"start": v(-48.99, -3.3) * mm, "end": v(-48.28, -3.32) * mm});
            skLineSegment(sketch, "E222", {"start": v(-47.72, -3.42) * mm, "end": v(-47.07, -3.58) * mm});
            skLineSegment(sketch, "E223", {"start": v(-46.44, -4.06) * mm, "end": v(-45.78, -4.24) * mm});
            skLineSegment(sketch, "E224", {"start": v(-45.02, -8.27) * mm, "end": v(-44.54, -8.27) * mm});
            skSolve(sketch);
        }
        {
            var Q0;
            Q0=makeQuery(id+"F14.imprint","IMPRINT",FACE,{"disambiguationData":[TD([[makeQuery(id+"F14.imprint","IMPRINT",EDGE,{"derivedFrom":sQuery(id+"F14.wireOp",EDGE,"E205")}),1.0]])]});
            extrude(context, id + "F15", {"entities" : qUnion([Q0]), "operationType" : NewBodyOperationType.REMOVE, "endBound" : BoundingType.THROUGH_ALL, "oppositeDirection" : true, "depth" : 25.4 * mm});
        }
        {
            var Q0;
            Q0=makeQuery(id+"F2.opExtrude","CAP_FACE",FACE,{"disambiguationData":[OSD([sQuery(id+"F0.wireOp",EDGE,"E0"),sQuery(id+"F0.wireOp",EDGE,"E1"),sQuery(id+"F0.wireOp",EDGE,"E2"),sQuery(id+"F0.wireOp",EDGE,"E3"),sQuery(id+"F0.wireOp",EDGE,"E4.sketch_text.stroke-0"),sQuery(id+"F0.wireOp",EDGE,"E4.sketch_text.stroke-1"),sQuery(id+"F0.wireOp",EDGE,"E4.sketch_text.stroke-2"),sQuery(id+"F0.wireOp",EDGE,"E4.sketch_text.stroke-3"),sQuery(id+"F0.wireOp",EDGE,"E4.sketch_text.stroke-4"),sQuery(id+"F0.wireOp",EDGE,"E4.sketch_text.stroke-5"),sQuery(id+"F0.wireOp",EDGE,"E4.sketch_text.stroke-6"),sQuery(id+"F0.wireOp",EDGE,"E4.sketch_text.stroke-7"),sQuery(id+"F0.wireOp",EDGE,"E4.sketch_text.stroke-8"),sQuery(id+"F0.wireOp",EDGE,"E4.sketch_text.stroke-9"),sQuery(id+"F0.wireOp",EDGE,"E4.sketch_text.stroke-10"),sQuery(id+"F0.wireOp",EDGE,"E4.sketch_text.stroke-11"),sQuery(id+"F0.wireOp",EDGE,"E4.sketch_text.stroke-12"),sQuery(id+"F0.wireOp",EDGE,"E4.sketch_text.stroke-13"),sQuery(id+"F0.wireOp",EDGE,"E4.sketch_text.stroke-14"),sQuery(id+"F0.wireOp",EDGE,"E4.sketch_text.stroke-15"),sQuery(id+"F0.wireOp",EDGE,"E4.sketch_text.stroke-16"),sQuery(id+"F0.wireOp",EDGE,"E4.sketch_text.stroke-17"),sQuery(id+"F0.wireOp",EDGE,"E4.sketch_text.stroke-18"),sQuery(id+"F0.wireOp",EDGE,"E4.sketch_text.stroke-19"),sQuery(id+"F0.wireOp",EDGE,"E4.sketch_text.stroke-20"),sQuery(id+"F0.wireOp",EDGE,"E4.sketch_text.stroke-21"),sQuery(id+"F0.wireOp",EDGE,"E4.sketch_text.stroke-22"),sQuery(id+"F0.wireOp",EDGE,"E4.sketch_text.stroke-23"),sQuery(id+"F0.wireOp",EDGE,"E4.sketch_text.stroke-24"),sQuery(id+"F0.wireOp",EDGE,"E4.sketch_text.stroke-25"),sQuery(id+"F0.wireOp",EDGE,"E4.sketch_text.stroke-26"),sQuery(id+"F0.wireOp",EDGE,"E4.sketch_text.stroke-27"),sQuery(id+"F0.wireOp",EDGE,"E4.sketch_text.stroke-28"),sQuery(id+"F0.wireOp",EDGE,"E4.sketch_text.stroke-29"),sQuery(id+"F0.wireOp",EDGE,"E4.sketch_text.stroke-30"),sQuery(id+"F0.wireOp",EDGE,"E4.sketch_text.stroke-31"),sQuery(id+"F0.wireOp",EDGE,"E4.sketch_text.stroke-32"),sQuery(id+"F0.wireOp",EDGE,"E4.sketch_text.stroke-33"),sQuery(id+"F0.wireOp",EDGE,"E4.sketch_text.stroke-34"),sQuery(id+"F0.wireOp",EDGE,"E4.sketch_text.stroke-35"),sQuery(id+"F0.wireOp",EDGE,"E4.sketch_text.stroke-36"),sQuery(id+"F0.wireOp",EDGE,"E4.sketch_text.stroke-37"),sQuery(id+"F0.wireOp",EDGE,"E4.sketch_text.stroke-38"),sQuery(id+"F0.wireOp",EDGE,"E4.sketch_text.stroke-39"),sQuery(id+"F0.wireOp",EDGE,"E4.sketch_text.stroke-40"),sQuery(id+"F0.wireOp",EDGE,"E4.sketch_text.stroke-41"),sQuery(id+"F0.wireOp",EDGE,"E4.sketch_text.stroke-42"),sQuery(id+"F0.wireOp",EDGE,"E4.sketch_text.stroke-43"),sQuery(id+"F0.wireOp",EDGE,"E4.sketch_text.stroke-44"),sQuery(id+"F0.wireOp",EDGE,"E4.sketch_text.stroke-45"),sQuery(id+"F0.wireOp",EDGE,"E4.sketch_text.stroke-46"),sQuery(id+"F0.wireOp",EDGE,"E4.sketch_text.stroke-47"),sQuery(id+"F0.wireOp",EDGE,"E4.sketch_text.stroke-48"),sQuery(id+"F0.wireOp",EDGE,"E4.sketch_text.stroke-49"),sQuery(id+"F0.wireOp",EDGE,"E4.sketch_text.stroke-50"),sQuery(id+"F0.wireOp",EDGE,"E4.sketch_text.stroke-51"),sQuery(id+"F0.wireOp",EDGE,"E4.sketch_text.stroke-52"),sQuery(id+"F0.wireOp",EDGE,"E4.sketch_text.stroke-53"),sQuery(id+"F0.wireOp",EDGE,"E4.sketch_text.stroke-54"),sQuery(id+"F0.wireOp",EDGE,"E4.sketch_text.stroke-55"),sQuery(id+"F0.wireOp",EDGE,"E4.sketch_text.stroke-56"),sQuery(id+"F0.wireOp",EDGE,"E4.sketch_text.stroke-57"),sQuery(id+"F0.wireOp",EDGE,"E4.sketch_text.stroke-58"),sQuery(id+"F0.wireOp",EDGE,"E4.sketch_text.stroke-59"),sQuery(id+"F0.wireOp",EDGE,"E4.sketch_text.stroke-60"),sQuery(id+"F0.wireOp",EDGE,"E4.sketch_text.stroke-61"),sQuery(id+"F0.wireOp",EDGE,"E4.sketch_text.stroke-62"),sQuery(id+"F0.wireOp",EDGE,"E4.sketch_text.stroke-63"),sQuery(id+"F0.wireOp",EDGE,"E4.sketch_text.stroke-64"),sQuery(id+"F0.wireOp",EDGE,"E4.sketch_text.stroke-65"),sQuery(id+"F0.wireOp",EDGE,"E4.sketch_text.stroke-66"),sQuery(id+"F0.wireOp",EDGE,"E4.sketch_text.stroke-67"),sQuery(id+"F0.wireOp",EDGE,"E4.sketch_text.stroke-68"),sQuery(id+"F0.wireOp",EDGE,"E4.sketch_text.stroke-69"),sQuery(id+"F0.wireOp",EDGE,"E4.sketch_text.stroke-70"),sQuery(id+"F0.wireOp",EDGE,"E4.sketch_text.stroke-71"),sQuery(id+"F0.wireOp",EDGE,"E4.sketch_text.stroke-72"),sQuery(id+"F0.wireOp",EDGE,"E4.sketch_text.stroke-73"),sQuery(id+"F0.wireOp",EDGE,"E4.sketch_text.stroke-74"),sQuery(id+"F0.wireOp",EDGE,"E4.sketch_text.stroke-75"),sQuery(id+"F0.wireOp",EDGE,"E4.sketch_text.stroke-76"),sQuery(id+"F0.wireOp",EDGE,"E4.sketch_text.stroke-77"),sQuery(id+"F0.wireOp",EDGE,"E4.sketch_text.stroke-78"),sQuery(id+"F0.wireOp",EDGE,"E4.sketch_text.stroke-79"),sQuery(id+"F0.wireOp",EDGE,"E4.sketch_text.stroke-80"),sQuery(id+"F0.wireOp",EDGE,"E4.sketch_text.stroke-81"),sQuery(id+"F0.wireOp",EDGE,"E4.sketch_text.stroke-82"),sQuery(id+"F0.wireOp",EDGE,"E4.sketch_text.stroke-83"),sQuery(id+"F0.wireOp",EDGE,"E4.sketch_text.stroke-84"),sQuery(id+"F0.wireOp",EDGE,"E4.sketch_text.stroke-85"),sQuery(id+"F0.wireOp",EDGE,"E4.sketch_text.stroke-86"),sQuery(id+"F0.wireOp",EDGE,"E4.sketch_text.stroke-87"),sQuery(id+"F0.wireOp",EDGE,"E4.sketch_text.stroke-88"),sQuery(id+"F0.wireOp",EDGE,"E4.sketch_text.stroke-89"),sQuery(id+"F0.wireOp",EDGE,"E4.sketch_text.stroke-90"),sQuery(id+"F0.wireOp",EDGE,"E4.sketch_text.stroke-91"),sQuery(id+"F0.wireOp",EDGE,"E4.sketch_text.stroke-92"),sQuery(id+"F0.wireOp",EDGE,"E4.sketch_text.stroke-93"),sQuery(id+"F0.wireOp",EDGE,"E4.sketch_text.stroke-94"),sQuery(id+"F0.wireOp",EDGE,"E4.sketch_text.stroke-95"),sQuery(id+"F0.wireOp",EDGE,"E4.sketch_text.stroke-96"),sQuery(id+"F0.wireOp",EDGE,"E4.sketch_text.stroke-97"),sQuery(id+"F0.wireOp",EDGE,"E4.sketch_text.stroke-98"),sQuery(id+"F0.wireOp",EDGE,"E4.sketch_text.stroke-99"),sQuery(id+"F0.wireOp",EDGE,"E4.sketch_text.stroke-100"),sQuery(id+"F0.wireOp",EDGE,"E4.sketch_text.stroke-101"),sQuery(id+"F0.wireOp",EDGE,"E4.sketch_text.stroke-102"),sQuery(id+"F0.wireOp",EDGE,"E4.sketch_text.stroke-103"),sQuery(id+"F0.wireOp",EDGE,"E4.sketch_text.stroke-104"),sQuery(id+"F0.wireOp",EDGE,"E4.sketch_text.stroke-105"),sQuery(id+"F0.wireOp",EDGE,"E4.sketch_text.stroke-106"),sQuery(id+"F0.wireOp",EDGE,"E4.sketch_text.stroke-107"),sQuery(id+"F0.wireOp",EDGE,"E4.sketch_text.stroke-108"),sQuery(id+"F0.wireOp",EDGE,"E4.sketch_text.stroke-109"),sQuery(id+"F0.wireOp",EDGE,"E4.sketch_text.stroke-110"),sQuery(id+"F0.wireOp",EDGE,"E4.sketch_text.stroke-111"),sQuery(id+"F0.wireOp",EDGE,"E4.sketch_text.stroke-112"),sQuery(id+"F0.wireOp",EDGE,"E4.sketch_text.stroke-113"),sQuery(id+"F0.wireOp",EDGE,"E4.sketch_text.stroke-114"),sQuery(id+"F0.wireOp",EDGE,"E4.sketch_text.stroke-115"),sQuery(id+"F0.wireOp",EDGE,"E4.sketch_text.stroke-116"),sQuery(id+"F0.wireOp",EDGE,"E4.sketch_text.stroke-117"),sQuery(id+"F0.wireOp",EDGE,"E4.sketch_text.stroke-118"),sQuery(id+"F0.wireOp",EDGE,"E4.sketch_text.stroke-119"),sQuery(id+"F0.wireOp",EDGE,"E4.sketch_text.stroke-120"),sQuery(id+"F0.wireOp",EDGE,"E4.sketch_text.stroke-121"),sQuery(id+"F0.wireOp",EDGE,"E4.sketch_text.stroke-122"),sQuery(id+"F0.wireOp",EDGE,"E4.sketch_text.stroke-123"),sQuery(id+"F0.wireOp",EDGE,"E4.sketch_text.stroke-124"),sQuery(id+"F0.wireOp",EDGE,"E4.sketch_text.stroke-125"),sQuery(id+"F0.wireOp",EDGE,"E4.sketch_text.stroke-126"),sQuery(id+"F0.wireOp",EDGE,"E4.sketch_text.stroke-127"),sQuery(id+"F0.wireOp",EDGE,"E4.sketch_text.stroke-128"),sQuery(id+"F0.wireOp",EDGE,"E4.sketch_text.stroke-129"),sQuery(id+"F0.wireOp",EDGE,"E4.sketch_text.stroke-130"),sQuery(id+"F0.wireOp",EDGE,"E4.sketch_text.stroke-131"),sQuery(id+"F0.wireOp",EDGE,"E4.sketch_text.stroke-132"),sQuery(id+"F0.wireOp",EDGE,"E4.sketch_text.stroke-133"),sQuery(id+"F0.wireOp",EDGE,"E4.sketch_text.stroke-134"),sQuery(id+"F0.wireOp",EDGE,"E4.sketch_text.stroke-135"),sQuery(id+"F0.wireOp",EDGE,"E4.sketch_text.stroke-136"),sQuery(id+"F0.wireOp",EDGE,"E4.sketch_text.stroke-137"),sQuery(id+"F0.wireOp",EDGE,"E4.sketch_text.stroke-138"),sQuery(id+"F0.wireOp",EDGE,"E4.sketch_text.stroke-139"),sQuery(id+"F0.wireOp",EDGE,"E4.sketch_text.stroke-140"),sQuery(id+"F0.wireOp",EDGE,"E4.sketch_text.stroke-141"),sQuery(id+"F0.wireOp",EDGE,"E4.sketch_text.stroke-142"),sQuery(id+"F0.wireOp",EDGE,"E4.sketch_text.stroke-143"),sQuery(id+"F0.wireOp",EDGE,"E4.sketch_text.stroke-144"),sQuery(id+"F0.wireOp",EDGE,"E4.sketch_text.stroke-145"),sQuery(id+"F0.wireOp",EDGE,"E4.sketch_text.stroke-146"),sQuery(id+"F0.wireOp",EDGE,"E4.sketch_text.stroke-147"),sQuery(id+"F0.wireOp",EDGE,"E4.sketch_text.stroke-148"),sQuery(id+"F0.wireOp",EDGE,"E4.sketch_text.stroke-149"),sQuery(id+"F0.wireOp",EDGE,"E4.sketch_text.stroke-150"),sQuery(id+"F0.wireOp",EDGE,"E4.sketch_text.stroke-151"),sQuery(id+"F0.wireOp",EDGE,"E4.sketch_text.stroke-152"),sQuery(id+"F0.wireOp",EDGE,"E4.sketch_text.stroke-153"),sQuery(id+"F0.wireOp",EDGE,"E4.sketch_text.stroke-154"),sQuery(id+"F0.wireOp",EDGE,"E4.sketch_text.stroke-155"),sQuery(id+"F0.wireOp",EDGE,"E4.sketch_text.stroke-156"),sQuery(id+"F0.wireOp",EDGE,"E4.sketch_text.stroke-157"),sQuery(id+"F0.wireOp",EDGE,"E4.sketch_text.stroke-158"),sQuery(id+"F0.wireOp",EDGE,"E4.sketch_text.stroke-159"),sQuery(id+"F0.wireOp",EDGE,"E4.sketch_text.stroke-160"),sQuery(id+"F0.wireOp",EDGE,"E4.sketch_text.stroke-161"),sQuery(id+"F0.wireOp",EDGE,"E4.sketch_text.stroke-162"),sQuery(id+"F0.wireOp",EDGE,"E4.sketch_text.stroke-163"),sQuery(id+"F0.wireOp",EDGE,"E4.sketch_text.stroke-164"),sQuery(id+"F0.wireOp",EDGE,"E4.sketch_text.stroke-165"),sQuery(id+"F0.wireOp",EDGE,"E4.sketch_text.stroke-166"),sQuery(id+"F0.wireOp",EDGE,"E4.sketch_text.stroke-167"),sQuery(id+"F0.wireOp",EDGE,"E4.sketch_text.stroke-168"),sQuery(id+"F0.wireOp",EDGE,"E4.sketch_text.stroke-169"),sQuery(id+"F0.wireOp",EDGE,"E4.sketch_text.stroke-170"),sQuery(id+"F0.wireOp",EDGE,"E4.sketch_text.stroke-171"),sQuery(id+"F0.wireOp",EDGE,"E4.sketch_text.stroke-172"),sQuery(id+"F0.wireOp",EDGE,"E4.sketch_text.stroke-173"),sQuery(id+"F0.wireOp",EDGE,"E4.sketch_text.stroke-174")])],"isStart":false});
            var sketch = newSketch(context, id + "F16", { "sketchPlane" : qUnion([Q0])});
            skLineSegment(sketch, "E225", {"start": v(-18.27, -3.76) * mm, "end": v(-16.88, -6.63) * mm});
            skLineSegment(sketch, "E226", {"start": v(-14.14, -12.3) * mm, "end": v(-14.4, -12.64) * mm});
            skLineSegment(sketch, "E227", {"start": v(-14.4, -12.64) * mm, "end": v(-17.45, -10.78) * mm});
            skLineSegment(sketch, "E228", {"start": v(-23.45, -7.13) * mm, "end": v(-23.39, -6.8) * mm});
            skLineSegment(sketch, "E229", {"start": v(-23.39, -6.8) * mm, "end": v(-19.9, -6.86) * mm});
            skLineSegment(sketch, "E230", {"start": v(-13.01, -7) * mm, "end": v(-12.92, -7.2) * mm});
            skLineSegment(sketch, "E231", {"start": v(-12.92, -7.2) * mm, "end": v(-15.44, -9) * mm});
            skLineSegment(sketch, "E232", {"start": v(-21.38, -13.22) * mm, "end": v(-21.62, -12.97) * mm});
            skLineSegment(sketch, "E233", {"start": v(-21.62, -12.97) * mm, "end": v(-20.36, -9.27) * mm});
            skLineSegment(sketch, "E234", {"start": v(-18.5, -3.76) * mm, "end": v(-18.27, -3.76) * mm});
            skArc(sketch, "E235", {"start": v(-16.93, -8.46) * mm, "mid": v(-17.02, -8.3) * mm, "end": v(-17.14, -8.14) * mm});
            skArc(sketch, "E236", {"start": v(-18.96, -8.4) * mm, "mid": v(-18.87, -8.55) * mm, "end": v(-18.76, -8.68) * mm});
            skLineSegment(sketch, "E237", {"start": v(-22.73, -7.15) * mm, "end": v(-20.13, -8.58) * mm});
            skLineSegment(sketch, "E238", {"start": v(-22.8, -7.1) * mm, "end": v(-19.99, -7.1) * mm});
            skLineSegment(sketch, "E239", {"start": v(-19.15, -6.88) * mm, "end": v(-18.36, -4.46) * mm});
            skLineSegment(sketch, "E240", {"start": v(-18.36, -4.46) * mm, "end": v(-17.24, -6.63) * mm});
            skLineSegment(sketch, "E241", {"start": v(-16.55, -7.32) * mm, "end": v(-13.8, -7.32) * mm});
            skLineSegment(sketch, "E242", {"start": v(-13.8, -7.32) * mm, "end": v(-15.67, -8.7) * mm});
            skLineSegment(sketch, "E243", {"start": v(-16.03, -9.42) * mm, "end": v(-14.74, -12.08) * mm});
            skLineSegment(sketch, "E244", {"start": v(-14.74, -12.08) * mm, "end": v(-17.14, -10.5) * mm});
            skLineSegment(sketch, "E245", {"start": v(-18.11, -10.38) * mm, "end": v(-21.04, -12.5) * mm});
            skLineSegment(sketch, "E246", {"start": v(-21.04, -12.5) * mm, "end": v(-19.94, -9.52) * mm});
            skLineSegment(sketch, "E247", {"start": v(-19.78, -8.85) * mm, "end": v(-19.11, -9.26) * mm});
            skLineSegment(sketch, "E248", {"start": v(-17.75, -10.09) * mm, "end": v(-17.06, -9.6) * mm});
            skLineSegment(sketch, "E249", {"start": v(-16.14, -8.96) * mm, "end": v(-16.51, -8.14) * mm});
            skLineSegment(sketch, "E250", {"start": v(-16.87, -7.35) * mm, "end": v(-17.83, -7.27) * mm});
            skLineSegment(sketch, "E251", {"start": v(-19.03, -7.17) * mm, "end": v(-19.26, -7.68) * mm});
            skLineSegment(sketch, "E252", {"start": v(-19.9, -6.86) * mm, "end": v(-19.99, -7.1) * mm});
            skLineSegment(sketch, "E253", {"start": v(-20.36, -9.27) * mm, "end": v(-19.94, -9.52) * mm});
            skLineSegment(sketch, "E254", {"start": v(-17.45, -10.78) * mm, "end": v(-17.14, -10.5) * mm});
            skLineSegment(sketch, "E255", {"start": v(-15.44, -9) * mm, "end": v(-15.67, -8.7) * mm});
            skLineSegment(sketch, "E256", {"start": v(-16.88, -6.63) * mm, "end": v(-17.24, -6.63) * mm});
            skLineSegment(sketch, "E257.trimOffspring", {"start": v(-19.15, -6.88) * mm, "end": v(-13.01, -7) * mm});
            skLineSegment(sketch, "E258.trimOffspring", {"start": v(-20.13, -8.58) * mm, "end": v(-18.5, -3.76) * mm});
            skLineSegment(sketch, "E259.trimOffspring", {"start": v(-18.11, -10.38) * mm, "end": v(-23.45, -7.13) * mm});
            skLineSegment(sketch, "E260.trimOffspring", {"start": v(-16.03, -9.42) * mm, "end": v(-21.38, -13.22) * mm});
            skLineSegment(sketch, "E261.trimOffspring", {"start": v(-16.55, -7.32) * mm, "end": v(-14.14, -12.3) * mm});
            skLineSegment(sketch, "E262", {"start": v(-18.76, -8.68) * mm, "end": v(-19.11, -9.26) * mm});
            skLineSegment(sketch, "E263", {"start": v(-18.58, -8.81) * mm, "end": v(-18.92, -9.38) * mm});
            skLineSegment(sketch, "E264", {"start": v(-17.52, -8.94) * mm, "end": v(-17.06, -9.6) * mm});
            skLineSegment(sketch, "E265", {"start": v(-17.34, -8.83) * mm, "end": v(-16.88, -9.48) * mm});
            skLineSegment(sketch, "E266", {"start": v(-17.14, -8.14) * mm, "end": v(-16.51, -8.14) * mm});
            skLineSegment(sketch, "E267", {"start": v(-17.27, -8.02) * mm, "end": v(-16.57, -8.02) * mm});
            skLineSegment(sketch, "E268", {"start": v(-17.74, -7.8) * mm, "end": v(-17.83, -7.27) * mm});
            skLineSegment(sketch, "E269", {"start": v(-18.06, -7.78) * mm, "end": v(-18.06, -7.25) * mm});
            skLineSegment(sketch, "E270", {"start": v(-18.6, -7.98) * mm, "end": v(-19.26, -7.68) * mm});
            skLineSegment(sketch, "E271", {"start": v(-18.76, -8.12) * mm, "end": v(-19.34, -7.86) * mm});
            skArc(sketch, "E272.trimOffspring", {"start": v(-18.58, -8.82) * mm, "mid": v(-18.07, -9) * mm, "end": v(-17.52, -8.94) * mm});
            skLineSegment(sketch, "E273.trimOffspring", {"start": v(-18.92, -9.38) * mm, "end": v(-17.75, -10.09) * mm});
            skLineSegment(sketch, "E274.trimOffspring", {"start": v(-19.34, -7.86) * mm, "end": v(-19.78, -8.85) * mm});
            skArc(sketch, "E275.trimOffspring", {"start": v(-18.76, -8.12) * mm, "mid": v(-18.87, -8.25) * mm, "end": v(-18.96, -8.4) * mm});
            skArc(sketch, "E276.trimOffspring", {"start": v(-18.06, -7.78) * mm, "mid": v(-18.34, -7.84) * mm, "end": v(-18.6, -7.98) * mm});
            skLineSegment(sketch, "E277.trimOffspring", {"start": v(-18.06, -7.25) * mm, "end": v(-19.03, -7.17) * mm});
            skArc(sketch, "E278.trimOffspring", {"start": v(-17.26, -8.02) * mm, "mid": v(-17.49, -7.88) * mm, "end": v(-17.74, -7.8) * mm});
            skLineSegment(sketch, "E279.trimOffspring", {"start": v(-16.57, -8.02) * mm, "end": v(-16.87, -7.35) * mm});
            skArc(sketch, "E280.trimOffspring", {"start": v(-17.32, -8.85) * mm, "mid": v(-17.1, -8.68) * mm, "end": v(-16.93, -8.46) * mm});
            skLineSegment(sketch, "E281.trimOffspring", {"start": v(-16.88, -9.48) * mm, "end": v(-16.14, -8.96) * mm});
            skLineSegment(sketch, "E282", {"start": v(-22.8, -7.1) * mm, "end": v(-22.73, -7.15) * mm});
            skSolve(sketch);
        }
        {
            var Q0;
            Q0 = qSketchRegion(id + "F16", true);
            extrude(context, id + "F17", {"entities" : qUnion([Q0]), "operationType" : NewBodyOperationType.REMOVE, "endBound" : BoundingType.THROUGH_ALL, "oppositeDirection" : true, "depth" : 25.4 * mm});
        }
        {
            var Q0;
            {var subQ0=sQuery(id+"F0.wireOp",EDGE,"E4.sketch_text.stroke-2");var subQ1=sQuery(id+"F0.wireOp",EDGE,"E4.sketch_text.stroke-122");var subQ2=sQuery(id+"F0.wireOp",EDGE,"E4.sketch_text.stroke-22");var subQ3=sQuery(id+"F0.wireOp",EDGE,"E4.sketch_text.stroke-94");var subQ4=sQuery(id+"F0.wireOp",EDGE,"E4.sketch_text.stroke-86");var subQ5=sQuery(id+"F0.wireOp",EDGE,"E4.sketch_text.stroke-92");var subQ6=sQuery(id+"F0.wireOp",EDGE,"E4.sketch_text.stroke-75");var subQ7=sQuery(id+"F0.wireOp",EDGE,"E4.sketch_text.stroke-112");var subQ8=sQuery(id+"F0.wireOp",EDGE,"E4.sketch_text.stroke-23");var subQ9=sQuery(id+"F0.wireOp",EDGE,"E4.sketch_text.stroke-114");var subQ10=sQuery(id+"F0.wireOp",EDGE,"E4.sketch_text.stroke-106");var subQ11=sQuery(id+"F0.wireOp",EDGE,"E4.sketch_text.stroke-101");var subQ12=sQuery(id+"F0.wireOp",EDGE,"E4.sketch_text.stroke-105");var subQ13=sQuery(id+"F0.wireOp",EDGE,"E4.sketch_text.stroke-104");var subQ14=sQuery(id+"F0.wireOp",EDGE,"E4.sketch_text.stroke-85");var subQ15=sQuery(id+"F0.wireOp",EDGE,"E4.sketch_text.stroke-84");var subQ16=sQuery(id+"F0.wireOp",EDGE,"E4.sketch_text.stroke-83");var subQ17=sQuery(id+"F0.wireOp",EDGE,"E4.sketch_text.stroke-82");var subQ18=sQuery(id+"F0.wireOp",EDGE,"E4.sketch_text.stroke-170");var subQ19=sQuery(id+"F0.wireOp",EDGE,"E4.sketch_text.stroke-81");var subQ20=sQuery(id+"F0.wireOp",EDGE,"E4.sketch_text.stroke-9");var subQ21=sQuery(id+"F0.wireOp",EDGE,"E4.sketch_text.stroke-169");var subQ22=sQuery(id+"F0.wireOp",EDGE,"E4.sketch_text.stroke-80");var subQ23=sQuery(id+"F0.wireOp",EDGE,"E4.sketch_text.stroke-8");var subQ24=sQuery(id+"F0.wireOp",EDGE,"E4.sketch_text.stroke-27");var subQ25=sQuery(id+"F0.wireOp",EDGE,"E4.sketch_text.stroke-79");var subQ26=sQuery(id+"F0.wireOp",EDGE,"E4.sketch_text.stroke-7");var subQ27=sQuery(id+"F0.wireOp",EDGE,"E4.sketch_text.stroke-18");var subQ28=sQuery(id+"F0.wireOp",EDGE,"E4.sketch_text.stroke-67");var subQ29=sQuery(id+"F0.wireOp",EDGE,"E4.sketch_text.stroke-66");var subQ30=sQuery(id+"F0.wireOp",EDGE,"E4.sketch_text.stroke-65");var subQ31=sQuery(id+"F0.wireOp",EDGE,"E4.sketch_text.stroke-64");var subQ32=sQuery(id+"F0.wireOp",EDGE,"E4.sketch_text.stroke-60");var subQ33=sQuery(id+"F0.wireOp",EDGE,"E4.sketch_text.stroke-148");var subQ34=sQuery(id+"F0.wireOp",EDGE,"E4.sketch_text.stroke-149");var subQ35=sQuery(id+"F0.wireOp",EDGE,"E4.sketch_text.stroke-147");var subQ36=sQuery(id+"F0.wireOp",EDGE,"E4.sketch_text.stroke-55");var subQ37=sQuery(id+"F0.wireOp",EDGE,"E4.sketch_text.stroke-54");var subQ38=sQuery(id+"F0.wireOp",EDGE,"E4.sketch_text.stroke-53");var subQ39=sQuery(id+"F0.wireOp",EDGE,"E4.sketch_text.stroke-52");var subQ40=sQuery(id+"F0.wireOp",EDGE,"E4.sketch_text.stroke-51");var subQ41=sQuery(id+"F0.wireOp",EDGE,"E4.sketch_text.stroke-50");var subQ42=sQuery(id+"F0.wireOp",EDGE,"E4.sketch_text.stroke-49");var subQ43=sQuery(id+"F0.wireOp",EDGE,"E4.sketch_text.stroke-97");var subQ44=sQuery(id+"F0.wireOp",EDGE,"E4.sketch_text.stroke-48");var subQ45=sQuery(id+"F0.wireOp",EDGE,"E4.sketch_text.stroke-47");var subQ46=sQuery(id+"F0.wireOp",EDGE,"E4.sketch_text.stroke-46");var subQ47=sQuery(id+"F0.wireOp",EDGE,"E4.sketch_text.stroke-45");var subQ48=sQuery(id+"F0.wireOp",EDGE,"E4.sketch_text.stroke-134");var subQ49=sQuery(id+"F0.wireOp",EDGE,"E4.sketch_text.stroke-21");var subQ50=sQuery(id+"F0.wireOp",EDGE,"E4.sketch_text.stroke-70");var subQ51=sQuery(id+"F0.wireOp",EDGE,"E4.sketch_text.stroke-141");var subQ52=sQuery(id+"F0.wireOp",EDGE,"E4.sketch_text.stroke-90");var subQ53=sQuery(id+"F0.wireOp",EDGE,"E4.sketch_text.stroke-161");var subQ54=sQuery(id+"F0.wireOp",EDGE,"E4.sketch_text.stroke-41");var subQ55=sQuery(id+"F0.wireOp",EDGE,"E4.sketch_text.stroke-133");var subQ56=sQuery(id+"F0.wireOp",EDGE,"E4.sketch_text.stroke-69");var subQ57=sQuery(id+"F0.wireOp",EDGE,"E4.sketch_text.stroke-140");var subQ58=sQuery(id+"F0.wireOp",EDGE,"E4.sketch_text.stroke-40");var subQ59=sQuery(id+"F0.wireOp",EDGE,"E4.sketch_text.stroke-132");var subQ60=sQuery(id+"F0.wireOp",EDGE,"E4.sketch_text.stroke-59");var subQ61=sQuery(id+"F0.wireOp",EDGE,"E4.sketch_text.stroke-160");var subQ62=sQuery(id+"F0.wireOp",EDGE,"E4.sketch_text.stroke-68");var subQ63=sQuery(id+"F0.wireOp",EDGE,"E4.sketch_text.stroke-139");var subQ64=sQuery(id+"F0.wireOp",EDGE,"E4.sketch_text.stroke-131");var subQ65=sQuery(id+"F0.wireOp",EDGE,"E4.sketch_text.stroke-58");var subQ66=sQuery(id+"F0.wireOp",EDGE,"E4.sketch_text.stroke-159");var subQ67=sQuery(id+"F0.wireOp",EDGE,"E4.sketch_text.stroke-76");var subQ68=sQuery(id+"F0.wireOp",EDGE,"E4.sketch_text.stroke-6");var subQ69=sQuery(id+"F0.wireOp",EDGE,"E4.sketch_text.stroke-78");var subQ70=sQuery(id+"F0.wireOp",EDGE,"E4.sketch_text.stroke-164");var subQ71=sQuery(id+"F0.wireOp",EDGE,"E4.sketch_text.stroke-5");var subQ72=sQuery(id+"F0.wireOp",EDGE,"E4.sketch_text.stroke-163");var subQ73=sQuery(id+"F0.wireOp",EDGE,"E4.sketch_text.stroke-1");var subQ74=sQuery(id+"F0.wireOp",EDGE,"E4.sketch_text.stroke-30");var subQ75=sQuery(id+"F0.wireOp",EDGE,"E4.sketch_text.stroke-119");var subQ76=sQuery(id+"F0.wireOp",EDGE,"E4.sketch_text.stroke-124");var subQ77=sQuery(id+"F0.wireOp",EDGE,"E4.sketch_text.stroke-4");var subQ78=sQuery(id+"F0.wireOp",EDGE,"E4.sketch_text.stroke-162");var subQ79=sQuery(id+"F0.wireOp",EDGE,"E4.sketch_text.stroke-89");var subQ80=sQuery(id+"F0.wireOp",EDGE,"E4.sketch_text.stroke-0");var subQ81=sQuery(id+"F0.wireOp",EDGE,"E4.sketch_text.stroke-118");var subQ82=sQuery(id+"F0.wireOp",EDGE,"E4.sketch_text.stroke-3");var subQ83=sQuery(id+"F0.wireOp",EDGE,"E4.sketch_text.stroke-88");var subQ84=sQuery(id+"F0.wireOp",EDGE,"E4.sketch_text.stroke-117");var subQ85=sQuery(id+"F0.wireOp",EDGE,"E4.sketch_text.stroke-87");var subQ86=sQuery(id+"F0.wireOp",EDGE,"E4.sketch_text.stroke-116");var subQ87=sQuery(id+"F0.wireOp",EDGE,"E4.sketch_text.stroke-61");var subQ88=sQuery(id+"F0.wireOp",EDGE,"E4.sketch_text.stroke-150");var subQ89=sQuery(id+"F0.wireOp",EDGE,"E4.sketch_text.stroke-25");var subQ90=sQuery(id+"F0.wireOp",EDGE,"E4.sketch_text.stroke-167");var subQ91=sQuery(id+"F0.wireOp",EDGE,"E4.sketch_text.stroke-138");var subQ92=sQuery(id+"F0.wireOp",EDGE,"E4.sketch_text.stroke-16");var subQ93=sQuery(id+"F0.wireOp",EDGE,"E4.sketch_text.stroke-15");var subQ94=sQuery(id+"F0.wireOp",EDGE,"E4.sketch_text.stroke-31");var subQ95=sQuery(id+"F0.wireOp",EDGE,"E4.sketch_text.stroke-120");var subQ96=sQuery(id+"F0.wireOp",EDGE,"E4.sketch_text.stroke-17");var subQ97=sQuery(id+"F0.wireOp",EDGE,"E4.sketch_text.stroke-33");var subQ98=sQuery(id+"F0.wireOp",EDGE,"E4.sketch_text.stroke-154");var subQ99=sQuery(id+"F0.wireOp",EDGE,"E4.sketch_text.stroke-77");var subQ100=sQuery(id+"F0.wireOp",EDGE,"E4.sketch_text.stroke-165");var subQ101=sQuery(id+"F0.wireOp",EDGE,"E4.sketch_text.stroke-57");var subQ102=sQuery(id+"F0.wireOp",EDGE,"E4.sketch_text.stroke-56");var subQ103=sQuery(id+"F0.wireOp",EDGE,"E4.sketch_text.stroke-128");var subQ104=sQuery(id+"F0.wireOp",EDGE,"E4.sketch_text.stroke-166");var subQ105=sQuery(id+"F0.wireOp",EDGE,"E4.sketch_text.stroke-63");var subQ106=sQuery(id+"F0.wireOp",EDGE,"E4.sketch_text.stroke-62");var subQ107=sQuery(id+"F0.wireOp",EDGE,"E4.sketch_text.stroke-34");var subQ108=sQuery(id+"F0.wireOp",EDGE,"E4.sketch_text.stroke-19");var subQ109=sQuery(id+"F0.wireOp",EDGE,"E4.sketch_text.stroke-26");var subQ110=sQuery(id+"F0.wireOp",EDGE,"E4.sketch_text.stroke-127");var subQ111=sQuery(id+"F0.wireOp",EDGE,"E4.sketch_text.stroke-121");var subQ112=sQuery(id+"F0.wireOp",EDGE,"E4.sketch_text.stroke-73");var subQ113=sQuery(id+"F0.wireOp",EDGE,"E4.sketch_text.stroke-35");var subQ114=sQuery(id+"F0.wireOp",EDGE,"E4.sketch_text.stroke-20");var subQ115=sQuery(id+"F0.wireOp",EDGE,"E4.sketch_text.stroke-71");var subQ116=sQuery(id+"F0.wireOp",EDGE,"E2");var subQ117=sQuery(id+"F0.wireOp",EDGE,"E4.sketch_text.stroke-99");var subQ118=sQuery(id+"F0.wireOp",EDGE,"E4.sketch_text.stroke-36");var subQ119=sQuery(id+"F0.wireOp",EDGE,"E4.sketch_text.stroke-108");var subQ120=sQuery(id+"F0.wireOp",EDGE,"E4.sketch_text.stroke-72");var subQ121=sQuery(id+"F0.wireOp",EDGE,"E3");var subQ122=sQuery(id+"F0.wireOp",EDGE,"E4.sketch_text.stroke-100");var subQ123=sQuery(id+"F0.wireOp",EDGE,"E4.sketch_text.stroke-171");var subQ124=sQuery(id+"F0.wireOp",EDGE,"E4.sketch_text.stroke-28");var subQ125=sQuery(id+"F0.wireOp",EDGE,"E4.sketch_text.stroke-129");var subQ126=sQuery(id+"F0.wireOp",EDGE,"E4.sketch_text.stroke-37");var subQ127=sQuery(id+"F0.wireOp",EDGE,"E4.sketch_text.stroke-109");var subQ128=sQuery(id+"F0.wireOp",EDGE,"E4.sketch_text.stroke-107");var subQ129=sQuery(id+"F0.wireOp",EDGE,"E4.sketch_text.stroke-91");var subQ130=sQuery(id+"F0.wireOp",EDGE,"E4.sketch_text.stroke-102");var subQ131=sQuery(id+"F0.wireOp",EDGE,"E4.sketch_text.stroke-29");var subQ132=sQuery(id+"F0.wireOp",EDGE,"E4.sketch_text.stroke-130");var subQ133=sQuery(id+"F0.wireOp",EDGE,"E4.sketch_text.stroke-38");var subQ134=sQuery(id+"F0.wireOp",EDGE,"E4.sketch_text.stroke-110");var subQ135=sQuery(id+"F0.wireOp",EDGE,"E4.sketch_text.stroke-74");var subQ136=sQuery(id+"F0.wireOp",EDGE,"E4.sketch_text.stroke-103");var subQ137=sQuery(id+"F0.wireOp",EDGE,"E4.sketch_text.stroke-39");var subQ138=sQuery(id+"F0.wireOp",EDGE,"E4.sketch_text.stroke-111");var subQ139=sQuery(id+"F0.wireOp",EDGE,"E4.sketch_text.stroke-24");var subQ140=sQuery(id+"F0.wireOp",EDGE,"E4.sketch_text.stroke-32");var subQ141=sQuery(id+"F0.wireOp",EDGE,"E4.sketch_text.stroke-93");var subQ142=sQuery(id+"F0.wireOp",EDGE,"E4.sketch_text.stroke-153");var subQ143=sQuery(id+"F0.wireOp",EDGE,"E0");var subQ144=sQuery(id+"F0.wireOp",EDGE,"E4.sketch_text.stroke-95");var subQ145=sQuery(id+"F0.wireOp",EDGE,"E4.sketch_text.stroke-96");var subQ146=sQuery(id+"F0.wireOp",EDGE,"E1");var subQ147=sQuery(id+"F0.wireOp",EDGE,"E4.sketch_text.stroke-98");var subQ148=sQuery(id+"F0.wireOp",EDGE,"E4.sketch_text.stroke-168");var subQ149=sQuery(id+"F0.wireOp",EDGE,"E4.sketch_text.stroke-10");var subQ150=sQuery(id+"F0.wireOp",EDGE,"E4.sketch_text.stroke-11");var subQ151=sQuery(id+"F0.wireOp",EDGE,"E4.sketch_text.stroke-113");var subQ152=sQuery(id+"F0.wireOp",EDGE,"E4.sketch_text.stroke-12");var subQ153=sQuery(id+"F0.wireOp",EDGE,"E4.sketch_text.stroke-13");var subQ154=sQuery(id+"F0.wireOp",EDGE,"E4.sketch_text.stroke-14");var subQ155=sQuery(id+"F0.wireOp",EDGE,"E4.sketch_text.stroke-115");var subQ156=sQuery(id+"F0.wireOp",EDGE,"E4.sketch_text.stroke-123");var subQ157=sQuery(id+"F0.wireOp",EDGE,"E4.sketch_text.stroke-125");var subQ158=sQuery(id+"F0.wireOp",EDGE,"E4.sketch_text.stroke-126");var subQ159=sQuery(id+"F0.wireOp",EDGE,"E4.sketch_text.stroke-137");var subQ160=sQuery(id+"F0.wireOp",EDGE,"E4.sketch_text.stroke-142");var subQ161=sQuery(id+"F0.wireOp",EDGE,"E4.sketch_text.stroke-42");var subQ162=sQuery(id+"F0.wireOp",EDGE,"E4.sketch_text.stroke-143");var subQ163=sQuery(id+"F0.wireOp",EDGE,"E4.sketch_text.stroke-43");var subQ164=sQuery(id+"F0.wireOp",EDGE,"E4.sketch_text.stroke-144");var subQ165=sQuery(id+"F0.wireOp",EDGE,"E4.sketch_text.stroke-44");var subQ166=sQuery(id+"F0.wireOp",EDGE,"E4.sketch_text.stroke-145");var subQ167=sQuery(id+"F0.wireOp",EDGE,"E4.sketch_text.stroke-146");var subQ168=sQuery(id+"F0.wireOp",EDGE,"E4.sketch_text.stroke-151");var subQ169=sQuery(id+"F0.wireOp",EDGE,"E4.sketch_text.stroke-135");var subQ170=sQuery(id+"F0.wireOp",EDGE,"E4.sketch_text.stroke-152");var subQ171=sQuery(id+"F0.wireOp",EDGE,"E4.sketch_text.stroke-136");var subQ172=sQuery(id+"F0.wireOp",EDGE,"E4.sketch_text.stroke-155");var subQ173=sQuery(id+"F0.wireOp",EDGE,"E4.sketch_text.stroke-156");var subQ174=sQuery(id+"F0.wireOp",EDGE,"E4.sketch_text.stroke-157");var subQ175=sQuery(id+"F0.wireOp",EDGE,"E4.sketch_text.stroke-158");var subQ176=sQuery(id+"F0.wireOp",EDGE,"E4.sketch_text.stroke-172");var subQ177=sQuery(id+"F0.wireOp",EDGE,"E4.sketch_text.stroke-173");var subQ178=sQuery(id+"F0.wireOp",EDGE,"E4.sketch_text.stroke-174");Q0=makeQuery(id+"F17.boolean.opBoolean","SPLIT",FACE,{"disambiguationData":[TD([makeQuery(id+"F2.opExtrude","SWEPT_FACE",FACE,{"disambiguationData":[OSD([subQ143])]})])],"derivedFrom":makeQuery(id+"F2.opExtrude","CAP_FACE",FACE,{"disambiguationData":[OSD([subQ143,subQ146,subQ116,subQ121,subQ80,subQ73,subQ0,subQ82,subQ77,subQ71,subQ68,subQ26,subQ23,subQ20,subQ149,subQ150,subQ152,subQ153,subQ154,subQ93,subQ92,subQ96,subQ27,subQ108,subQ114,subQ49,subQ2,subQ8,subQ139,subQ89,subQ109,subQ24,subQ124,subQ131,subQ74,subQ94,subQ140,subQ97,subQ107,subQ113,subQ118,subQ126,subQ133,subQ137,subQ58,subQ54,subQ161,subQ163,subQ165,subQ47,subQ46,subQ45,subQ44,subQ42,subQ41,subQ40,subQ39,subQ38,subQ37,subQ36,subQ102,subQ101,subQ65,subQ60,subQ32,subQ87,subQ106,subQ105,subQ31,subQ30,subQ29,subQ28,subQ62,subQ56,subQ50,subQ115,subQ120,subQ112,subQ135,subQ6,subQ67,subQ99,subQ69,subQ25,subQ22,subQ19,subQ17,subQ16,subQ15,subQ14,subQ4,subQ85,subQ83,subQ79,subQ52,subQ129,subQ5,subQ141,subQ3,subQ144,subQ145,subQ43,subQ147,subQ117,subQ122,subQ11,subQ130,subQ136,subQ13,subQ12,subQ10,subQ128,subQ119,subQ127,subQ134,subQ138,subQ7,subQ151,subQ9,subQ155,subQ86,subQ84,subQ81,subQ75,subQ95,subQ111,subQ1,subQ156,subQ76,subQ157,subQ158,subQ110,subQ103,subQ125,subQ132,subQ64,subQ59,subQ55,subQ48,subQ169,subQ171,subQ159,subQ91,subQ63,subQ57,subQ51,subQ160,subQ162,subQ164,subQ166,subQ167,subQ35,subQ33,subQ34,subQ88,subQ168,subQ170,subQ142,subQ98,subQ172,subQ173,subQ174,subQ175,subQ66,subQ61,subQ53,subQ78,subQ72,subQ70,subQ100,subQ104,subQ90,subQ148,subQ21,subQ18,subQ123,subQ176,subQ177,subQ178])],"isStart":false})});}
            var sketch = newSketch(context, id + "F18", { "sketchPlane" : qUnion([Q0])});
            skArc(sketch, "E283", {"start": v(2.57, -11.6) * mm, "mid": v(3.87, -10.08) * mm, "end": v(4.9, -8.38) * mm});
            skArc(sketch, "E284", {"start": v(3.2, -8.9) * mm, "mid": v(4.09, -8.76) * mm, "end": v(4.9, -8.38) * mm});
            skArc(sketch, "E285", {"start": v(3.2, -8.9) * mm, "mid": v(4.6, -7.1) * mm, "end": v(5.44, -5) * mm});
            skArc(sketch, "E286", {"start": v(5.44, -5) * mm, "mid": v(6.47, -7.12) * mm, "end": v(8, -8.9) * mm});
            skArc(sketch, "E287", {"start": v(6.16, -8.38) * mm, "mid": v(7.03, -8.83) * mm, "end": v(8, -8.9) * mm});
            skArc(sketch, "E288", {"start": v(6.16, -8.38) * mm, "mid": v(7.28, -10.14) * mm, "end": v(8.76, -11.63) * mm});
            skArc(sketch, "E289", {"start": v(6.16, -11.14) * mm, "mid": v(7.43, -11.55) * mm, "end": v(8.76, -11.63) * mm});
            skArc(sketch, "E290", {"start": v(2.57, -11.6) * mm, "mid": v(3.75, -11.47) * mm, "end": v(4.9, -11.2) * mm});
            skLineSegment(sketch, "E291", {"start": v(4.9, -11.2) * mm, "end": v(4.9, -13.2) * mm});
            skLineSegment(sketch, "E292", {"start": v(4.9, -13.2) * mm, "end": v(5.97, -13.2) * mm});
            skLineSegment(sketch, "E293", {"start": v(5.97, -13.2) * mm, "end": v(6.16, -11.14) * mm});
            skSolve(sketch);
        }
        {
            var Q0;
            Q0=makeQuery(id+"F18.imprint","IMPRINT",FACE,{"disambiguationData":[TD([[makeQuery(id+"F18.imprint","IMPRINT",EDGE,{"derivedFrom":sQuery(id+"F18.wireOp",EDGE,"E283")}),-1.0]])]});
            extrude(context, id + "F19", {"entities" : qUnion([Q0]), "operationType" : NewBodyOperationType.REMOVE, "endBound" : BoundingType.THROUGH_ALL, "oppositeDirection" : true, "depth" : 25.4 * mm});
        }
        {
            var Q0;
            {var subQ0=sQuery(id+"F0.wireOp",EDGE,"E4.sketch_text.stroke-2");var subQ1=sQuery(id+"F0.wireOp",EDGE,"E4.sketch_text.stroke-122");var subQ2=sQuery(id+"F0.wireOp",EDGE,"E4.sketch_text.stroke-22");var subQ3=sQuery(id+"F0.wireOp",EDGE,"E4.sketch_text.stroke-94");var subQ4=sQuery(id+"F0.wireOp",EDGE,"E4.sketch_text.stroke-86");var subQ5=sQuery(id+"F0.wireOp",EDGE,"E4.sketch_text.stroke-92");var subQ6=sQuery(id+"F0.wireOp",EDGE,"E4.sketch_text.stroke-75");var subQ7=sQuery(id+"F0.wireOp",EDGE,"E4.sketch_text.stroke-112");var subQ8=sQuery(id+"F0.wireOp",EDGE,"E4.sketch_text.stroke-23");var subQ9=sQuery(id+"F0.wireOp",EDGE,"E4.sketch_text.stroke-114");var subQ10=sQuery(id+"F0.wireOp",EDGE,"E4.sketch_text.stroke-106");var subQ11=sQuery(id+"F0.wireOp",EDGE,"E4.sketch_text.stroke-101");var subQ12=sQuery(id+"F0.wireOp",EDGE,"E4.sketch_text.stroke-105");var subQ13=sQuery(id+"F0.wireOp",EDGE,"E4.sketch_text.stroke-104");var subQ14=sQuery(id+"F0.wireOp",EDGE,"E4.sketch_text.stroke-85");var subQ15=sQuery(id+"F0.wireOp",EDGE,"E4.sketch_text.stroke-84");var subQ16=sQuery(id+"F0.wireOp",EDGE,"E4.sketch_text.stroke-83");var subQ17=sQuery(id+"F0.wireOp",EDGE,"E4.sketch_text.stroke-82");var subQ18=sQuery(id+"F0.wireOp",EDGE,"E4.sketch_text.stroke-170");var subQ19=sQuery(id+"F0.wireOp",EDGE,"E4.sketch_text.stroke-81");var subQ20=sQuery(id+"F0.wireOp",EDGE,"E4.sketch_text.stroke-9");var subQ21=sQuery(id+"F0.wireOp",EDGE,"E4.sketch_text.stroke-169");var subQ22=sQuery(id+"F0.wireOp",EDGE,"E4.sketch_text.stroke-80");var subQ23=sQuery(id+"F0.wireOp",EDGE,"E4.sketch_text.stroke-8");var subQ24=sQuery(id+"F0.wireOp",EDGE,"E4.sketch_text.stroke-27");var subQ25=sQuery(id+"F0.wireOp",EDGE,"E4.sketch_text.stroke-79");var subQ26=sQuery(id+"F0.wireOp",EDGE,"E4.sketch_text.stroke-7");var subQ27=sQuery(id+"F0.wireOp",EDGE,"E4.sketch_text.stroke-18");var subQ28=sQuery(id+"F0.wireOp",EDGE,"E4.sketch_text.stroke-67");var subQ29=sQuery(id+"F0.wireOp",EDGE,"E4.sketch_text.stroke-66");var subQ30=sQuery(id+"F0.wireOp",EDGE,"E4.sketch_text.stroke-65");var subQ31=sQuery(id+"F0.wireOp",EDGE,"E4.sketch_text.stroke-64");var subQ32=sQuery(id+"F0.wireOp",EDGE,"E4.sketch_text.stroke-60");var subQ33=sQuery(id+"F0.wireOp",EDGE,"E4.sketch_text.stroke-148");var subQ34=sQuery(id+"F0.wireOp",EDGE,"E4.sketch_text.stroke-149");var subQ35=sQuery(id+"F0.wireOp",EDGE,"E4.sketch_text.stroke-147");var subQ36=sQuery(id+"F0.wireOp",EDGE,"E4.sketch_text.stroke-55");var subQ37=sQuery(id+"F0.wireOp",EDGE,"E4.sketch_text.stroke-54");var subQ38=sQuery(id+"F0.wireOp",EDGE,"E4.sketch_text.stroke-53");var subQ39=sQuery(id+"F0.wireOp",EDGE,"E4.sketch_text.stroke-52");var subQ40=sQuery(id+"F0.wireOp",EDGE,"E4.sketch_text.stroke-51");var subQ41=sQuery(id+"F0.wireOp",EDGE,"E4.sketch_text.stroke-50");var subQ42=sQuery(id+"F0.wireOp",EDGE,"E4.sketch_text.stroke-49");var subQ43=sQuery(id+"F0.wireOp",EDGE,"E4.sketch_text.stroke-97");var subQ44=sQuery(id+"F0.wireOp",EDGE,"E4.sketch_text.stroke-48");var subQ45=sQuery(id+"F0.wireOp",EDGE,"E4.sketch_text.stroke-47");var subQ46=sQuery(id+"F0.wireOp",EDGE,"E4.sketch_text.stroke-46");var subQ47=sQuery(id+"F0.wireOp",EDGE,"E4.sketch_text.stroke-45");var subQ48=sQuery(id+"F0.wireOp",EDGE,"E4.sketch_text.stroke-134");var subQ49=sQuery(id+"F0.wireOp",EDGE,"E4.sketch_text.stroke-21");var subQ50=sQuery(id+"F0.wireOp",EDGE,"E4.sketch_text.stroke-70");var subQ51=sQuery(id+"F0.wireOp",EDGE,"E4.sketch_text.stroke-141");var subQ52=sQuery(id+"F0.wireOp",EDGE,"E4.sketch_text.stroke-90");var subQ53=sQuery(id+"F0.wireOp",EDGE,"E4.sketch_text.stroke-161");var subQ54=sQuery(id+"F0.wireOp",EDGE,"E4.sketch_text.stroke-41");var subQ55=sQuery(id+"F0.wireOp",EDGE,"E4.sketch_text.stroke-133");var subQ56=sQuery(id+"F0.wireOp",EDGE,"E4.sketch_text.stroke-69");var subQ57=sQuery(id+"F0.wireOp",EDGE,"E4.sketch_text.stroke-140");var subQ58=sQuery(id+"F0.wireOp",EDGE,"E4.sketch_text.stroke-40");var subQ59=sQuery(id+"F0.wireOp",EDGE,"E4.sketch_text.stroke-132");var subQ60=sQuery(id+"F0.wireOp",EDGE,"E4.sketch_text.stroke-59");var subQ61=sQuery(id+"F0.wireOp",EDGE,"E4.sketch_text.stroke-160");var subQ62=sQuery(id+"F0.wireOp",EDGE,"E4.sketch_text.stroke-68");var subQ63=sQuery(id+"F0.wireOp",EDGE,"E4.sketch_text.stroke-139");var subQ64=sQuery(id+"F0.wireOp",EDGE,"E4.sketch_text.stroke-131");var subQ65=sQuery(id+"F0.wireOp",EDGE,"E4.sketch_text.stroke-58");var subQ66=sQuery(id+"F0.wireOp",EDGE,"E4.sketch_text.stroke-159");var subQ67=sQuery(id+"F0.wireOp",EDGE,"E4.sketch_text.stroke-76");var subQ68=sQuery(id+"F0.wireOp",EDGE,"E4.sketch_text.stroke-6");var subQ69=sQuery(id+"F0.wireOp",EDGE,"E4.sketch_text.stroke-78");var subQ70=sQuery(id+"F0.wireOp",EDGE,"E4.sketch_text.stroke-164");var subQ71=sQuery(id+"F0.wireOp",EDGE,"E4.sketch_text.stroke-5");var subQ72=sQuery(id+"F0.wireOp",EDGE,"E4.sketch_text.stroke-163");var subQ73=sQuery(id+"F0.wireOp",EDGE,"E4.sketch_text.stroke-1");var subQ74=sQuery(id+"F0.wireOp",EDGE,"E4.sketch_text.stroke-30");var subQ75=sQuery(id+"F0.wireOp",EDGE,"E4.sketch_text.stroke-119");var subQ76=sQuery(id+"F0.wireOp",EDGE,"E4.sketch_text.stroke-124");var subQ77=sQuery(id+"F0.wireOp",EDGE,"E4.sketch_text.stroke-4");var subQ78=sQuery(id+"F0.wireOp",EDGE,"E4.sketch_text.stroke-162");var subQ79=sQuery(id+"F0.wireOp",EDGE,"E4.sketch_text.stroke-89");var subQ80=sQuery(id+"F0.wireOp",EDGE,"E4.sketch_text.stroke-0");var subQ81=sQuery(id+"F0.wireOp",EDGE,"E4.sketch_text.stroke-118");var subQ82=sQuery(id+"F0.wireOp",EDGE,"E4.sketch_text.stroke-3");var subQ83=sQuery(id+"F0.wireOp",EDGE,"E4.sketch_text.stroke-88");var subQ84=sQuery(id+"F0.wireOp",EDGE,"E4.sketch_text.stroke-117");var subQ85=sQuery(id+"F0.wireOp",EDGE,"E4.sketch_text.stroke-87");var subQ86=sQuery(id+"F0.wireOp",EDGE,"E4.sketch_text.stroke-116");var subQ87=sQuery(id+"F0.wireOp",EDGE,"E4.sketch_text.stroke-61");var subQ88=sQuery(id+"F0.wireOp",EDGE,"E4.sketch_text.stroke-150");var subQ89=sQuery(id+"F0.wireOp",EDGE,"E4.sketch_text.stroke-25");var subQ90=sQuery(id+"F0.wireOp",EDGE,"E4.sketch_text.stroke-167");var subQ91=sQuery(id+"F0.wireOp",EDGE,"E4.sketch_text.stroke-138");var subQ92=sQuery(id+"F0.wireOp",EDGE,"E4.sketch_text.stroke-16");var subQ93=sQuery(id+"F0.wireOp",EDGE,"E4.sketch_text.stroke-15");var subQ94=sQuery(id+"F0.wireOp",EDGE,"E4.sketch_text.stroke-31");var subQ95=sQuery(id+"F0.wireOp",EDGE,"E4.sketch_text.stroke-120");var subQ96=sQuery(id+"F0.wireOp",EDGE,"E4.sketch_text.stroke-17");var subQ97=sQuery(id+"F0.wireOp",EDGE,"E4.sketch_text.stroke-33");var subQ98=sQuery(id+"F0.wireOp",EDGE,"E4.sketch_text.stroke-154");var subQ99=sQuery(id+"F0.wireOp",EDGE,"E4.sketch_text.stroke-77");var subQ100=sQuery(id+"F0.wireOp",EDGE,"E4.sketch_text.stroke-165");var subQ101=sQuery(id+"F0.wireOp",EDGE,"E4.sketch_text.stroke-57");var subQ102=sQuery(id+"F0.wireOp",EDGE,"E4.sketch_text.stroke-56");var subQ103=sQuery(id+"F0.wireOp",EDGE,"E4.sketch_text.stroke-128");var subQ104=sQuery(id+"F0.wireOp",EDGE,"E4.sketch_text.stroke-166");var subQ105=sQuery(id+"F0.wireOp",EDGE,"E4.sketch_text.stroke-63");var subQ106=sQuery(id+"F0.wireOp",EDGE,"E4.sketch_text.stroke-62");var subQ107=sQuery(id+"F0.wireOp",EDGE,"E4.sketch_text.stroke-34");var subQ108=sQuery(id+"F0.wireOp",EDGE,"E4.sketch_text.stroke-19");var subQ109=sQuery(id+"F0.wireOp",EDGE,"E4.sketch_text.stroke-26");var subQ110=sQuery(id+"F0.wireOp",EDGE,"E4.sketch_text.stroke-127");var subQ111=sQuery(id+"F0.wireOp",EDGE,"E4.sketch_text.stroke-121");var subQ112=sQuery(id+"F0.wireOp",EDGE,"E4.sketch_text.stroke-73");var subQ113=sQuery(id+"F0.wireOp",EDGE,"E4.sketch_text.stroke-35");var subQ114=sQuery(id+"F0.wireOp",EDGE,"E4.sketch_text.stroke-20");var subQ115=sQuery(id+"F0.wireOp",EDGE,"E4.sketch_text.stroke-71");var subQ116=sQuery(id+"F0.wireOp",EDGE,"E2");var subQ117=sQuery(id+"F0.wireOp",EDGE,"E4.sketch_text.stroke-99");var subQ118=sQuery(id+"F0.wireOp",EDGE,"E4.sketch_text.stroke-36");var subQ119=sQuery(id+"F0.wireOp",EDGE,"E4.sketch_text.stroke-108");var subQ120=sQuery(id+"F0.wireOp",EDGE,"E4.sketch_text.stroke-72");var subQ121=sQuery(id+"F0.wireOp",EDGE,"E3");var subQ122=sQuery(id+"F0.wireOp",EDGE,"E4.sketch_text.stroke-100");var subQ123=sQuery(id+"F0.wireOp",EDGE,"E4.sketch_text.stroke-171");var subQ124=sQuery(id+"F0.wireOp",EDGE,"E4.sketch_text.stroke-28");var subQ125=sQuery(id+"F0.wireOp",EDGE,"E4.sketch_text.stroke-129");var subQ126=sQuery(id+"F0.wireOp",EDGE,"E4.sketch_text.stroke-37");var subQ127=sQuery(id+"F0.wireOp",EDGE,"E4.sketch_text.stroke-109");var subQ128=sQuery(id+"F0.wireOp",EDGE,"E4.sketch_text.stroke-107");var subQ129=sQuery(id+"F0.wireOp",EDGE,"E4.sketch_text.stroke-91");var subQ130=sQuery(id+"F0.wireOp",EDGE,"E4.sketch_text.stroke-102");var subQ131=sQuery(id+"F0.wireOp",EDGE,"E4.sketch_text.stroke-29");var subQ132=sQuery(id+"F0.wireOp",EDGE,"E4.sketch_text.stroke-130");var subQ133=sQuery(id+"F0.wireOp",EDGE,"E4.sketch_text.stroke-38");var subQ134=sQuery(id+"F0.wireOp",EDGE,"E4.sketch_text.stroke-110");var subQ135=sQuery(id+"F0.wireOp",EDGE,"E4.sketch_text.stroke-74");var subQ136=sQuery(id+"F0.wireOp",EDGE,"E4.sketch_text.stroke-103");var subQ137=sQuery(id+"F0.wireOp",EDGE,"E4.sketch_text.stroke-39");var subQ138=sQuery(id+"F0.wireOp",EDGE,"E4.sketch_text.stroke-111");var subQ139=sQuery(id+"F0.wireOp",EDGE,"E4.sketch_text.stroke-24");var subQ140=sQuery(id+"F0.wireOp",EDGE,"E4.sketch_text.stroke-32");var subQ141=sQuery(id+"F0.wireOp",EDGE,"E4.sketch_text.stroke-93");var subQ142=sQuery(id+"F0.wireOp",EDGE,"E4.sketch_text.stroke-153");var subQ143=sQuery(id+"F0.wireOp",EDGE,"E0");var subQ144=sQuery(id+"F0.wireOp",EDGE,"E4.sketch_text.stroke-95");var subQ145=sQuery(id+"F0.wireOp",EDGE,"E4.sketch_text.stroke-96");var subQ146=sQuery(id+"F0.wireOp",EDGE,"E1");var subQ147=sQuery(id+"F0.wireOp",EDGE,"E4.sketch_text.stroke-98");var subQ148=sQuery(id+"F0.wireOp",EDGE,"E4.sketch_text.stroke-168");var subQ149=sQuery(id+"F0.wireOp",EDGE,"E4.sketch_text.stroke-10");var subQ150=sQuery(id+"F0.wireOp",EDGE,"E4.sketch_text.stroke-11");var subQ151=sQuery(id+"F0.wireOp",EDGE,"E4.sketch_text.stroke-113");var subQ152=sQuery(id+"F0.wireOp",EDGE,"E4.sketch_text.stroke-12");var subQ153=sQuery(id+"F0.wireOp",EDGE,"E4.sketch_text.stroke-13");var subQ154=sQuery(id+"F0.wireOp",EDGE,"E4.sketch_text.stroke-14");var subQ155=sQuery(id+"F0.wireOp",EDGE,"E4.sketch_text.stroke-115");var subQ156=sQuery(id+"F0.wireOp",EDGE,"E4.sketch_text.stroke-123");var subQ157=sQuery(id+"F0.wireOp",EDGE,"E4.sketch_text.stroke-125");var subQ158=sQuery(id+"F0.wireOp",EDGE,"E4.sketch_text.stroke-126");var subQ159=sQuery(id+"F0.wireOp",EDGE,"E4.sketch_text.stroke-137");var subQ160=sQuery(id+"F0.wireOp",EDGE,"E4.sketch_text.stroke-142");var subQ161=sQuery(id+"F0.wireOp",EDGE,"E4.sketch_text.stroke-42");var subQ162=sQuery(id+"F0.wireOp",EDGE,"E4.sketch_text.stroke-143");var subQ163=sQuery(id+"F0.wireOp",EDGE,"E4.sketch_text.stroke-43");var subQ164=sQuery(id+"F0.wireOp",EDGE,"E4.sketch_text.stroke-144");var subQ165=sQuery(id+"F0.wireOp",EDGE,"E4.sketch_text.stroke-44");var subQ166=sQuery(id+"F0.wireOp",EDGE,"E4.sketch_text.stroke-145");var subQ167=sQuery(id+"F0.wireOp",EDGE,"E4.sketch_text.stroke-146");var subQ168=sQuery(id+"F0.wireOp",EDGE,"E4.sketch_text.stroke-151");var subQ169=sQuery(id+"F0.wireOp",EDGE,"E4.sketch_text.stroke-135");var subQ170=sQuery(id+"F0.wireOp",EDGE,"E4.sketch_text.stroke-152");var subQ171=sQuery(id+"F0.wireOp",EDGE,"E4.sketch_text.stroke-136");var subQ172=sQuery(id+"F0.wireOp",EDGE,"E4.sketch_text.stroke-155");var subQ173=sQuery(id+"F0.wireOp",EDGE,"E4.sketch_text.stroke-156");var subQ174=sQuery(id+"F0.wireOp",EDGE,"E4.sketch_text.stroke-157");var subQ175=sQuery(id+"F0.wireOp",EDGE,"E4.sketch_text.stroke-158");var subQ176=sQuery(id+"F0.wireOp",EDGE,"E4.sketch_text.stroke-172");var subQ177=sQuery(id+"F0.wireOp",EDGE,"E4.sketch_text.stroke-173");var subQ178=sQuery(id+"F0.wireOp",EDGE,"E4.sketch_text.stroke-174");Q0=makeQuery(id+"F17.boolean.opBoolean","SPLIT",FACE,{"disambiguationData":[TD([makeQuery(id+"F2.opExtrude","SWEPT_FACE",FACE,{"disambiguationData":[OSD([subQ143])]})])],"derivedFrom":makeQuery(id+"F2.opExtrude","CAP_FACE",FACE,{"disambiguationData":[OSD([subQ143,subQ146,subQ116,subQ121,subQ80,subQ73,subQ0,subQ82,subQ77,subQ71,subQ68,subQ26,subQ23,subQ20,subQ149,subQ150,subQ152,subQ153,subQ154,subQ93,subQ92,subQ96,subQ27,subQ108,subQ114,subQ49,subQ2,subQ8,subQ139,subQ89,subQ109,subQ24,subQ124,subQ131,subQ74,subQ94,subQ140,subQ97,subQ107,subQ113,subQ118,subQ126,subQ133,subQ137,subQ58,subQ54,subQ161,subQ163,subQ165,subQ47,subQ46,subQ45,subQ44,subQ42,subQ41,subQ40,subQ39,subQ38,subQ37,subQ36,subQ102,subQ101,subQ65,subQ60,subQ32,subQ87,subQ106,subQ105,subQ31,subQ30,subQ29,subQ28,subQ62,subQ56,subQ50,subQ115,subQ120,subQ112,subQ135,subQ6,subQ67,subQ99,subQ69,subQ25,subQ22,subQ19,subQ17,subQ16,subQ15,subQ14,subQ4,subQ85,subQ83,subQ79,subQ52,subQ129,subQ5,subQ141,subQ3,subQ144,subQ145,subQ43,subQ147,subQ117,subQ122,subQ11,subQ130,subQ136,subQ13,subQ12,subQ10,subQ128,subQ119,subQ127,subQ134,subQ138,subQ7,subQ151,subQ9,subQ155,subQ86,subQ84,subQ81,subQ75,subQ95,subQ111,subQ1,subQ156,subQ76,subQ157,subQ158,subQ110,subQ103,subQ125,subQ132,subQ64,subQ59,subQ55,subQ48,subQ169,subQ171,subQ159,subQ91,subQ63,subQ57,subQ51,subQ160,subQ162,subQ164,subQ166,subQ167,subQ35,subQ33,subQ34,subQ88,subQ168,subQ170,subQ142,subQ98,subQ172,subQ173,subQ174,subQ175,subQ66,subQ61,subQ53,subQ78,subQ72,subQ70,subQ100,subQ104,subQ90,subQ148,subQ21,subQ18,subQ123,subQ176,subQ177,subQ178])],"isStart":false})});}
            var sketch = newSketch(context, id + "F20", { "sketchPlane" : qUnion([Q0])});
            skLineSegment(sketch, "E294", {"start": v(30.58, 13.15) * mm, "end": v(30.29, 8.2) * mm});
            skArc(sketch, "E295", {"start": v(25.87, 9.15) * mm, "mid": v(26.64, 10.98) * mm, "end": v(25.36, 12.49) * mm});
            skArc(sketch, "E296", {"start": v(25.36, 12.49) * mm, "mid": v(23.79, 12.4) * mm, "end": v(22.28, 11.96) * mm});
            skArc(sketch, "E297", {"start": v(21.7, 9.77) * mm, "mid": v(23.73, 9.07) * mm, "end": v(25.87, 9.15) * mm});
            skArc(sketch, "E298", {"start": v(24.32, 14.1) * mm, "mid": v(23, 13.31) * mm, "end": v(22.28, 11.96) * mm});
            skArc(sketch, "E299", {"start": v(27.61, 14.1) * mm, "mid": v(25.97, 14.48) * mm, "end": v(24.32, 14.1) * mm});
            skArc(sketch, "E300", {"start": v(28.67, 11.6) * mm, "mid": v(28.5, 13) * mm, "end": v(27.61, 14.1) * mm});
            skArc(sketch, "E301", {"start": v(21.7, 9.77) * mm, "mid": v(22.17, 8.23) * mm, "end": v(23.24, 7.03) * mm});
            skArc(sketch, "E302", {"start": v(23.24, 7.03) * mm, "mid": v(25.24, 6.81) * mm, "end": v(27.1, 7.58) * mm});
            skArc(sketch, "E303", {"start": v(27.1, 7.58) * mm, "mid": v(27.98, 8.39) * mm, "end": v(28.52, 9.45) * mm});
            skLineSegment(sketch, "E304", {"start": v(28.52, 9.45) * mm, "end": v(30.29, 8.2) * mm});
            skLineSegment(sketch, "E305", {"start": v(28.67, 11.6) * mm, "end": v(30.58, 13.15) * mm});
            skSolve(sketch);
        }
        {
            var Q0;
            Q0=makeQuery(id+"F20.imprint","IMPRINT",FACE,{"disambiguationData":[TD([[makeQuery(id+"F20.imprint","IMPRINT",EDGE,{"derivedFrom":sQuery(id+"F20.wireOp",EDGE,"E294")}),-1.0]])]});
            extrude(context, id + "F21", {"entities" : qUnion([Q0]), "operationType" : NewBodyOperationType.REMOVE, "endBound" : BoundingType.THROUGH_ALL, "oppositeDirection" : true, "depth" : 25.4 * mm});
        }
        {
            var Q0;
            {var subQ0=sQuery(id+"F0.wireOp",EDGE,"E4.sketch_text.stroke-2");var subQ1=sQuery(id+"F0.wireOp",EDGE,"E4.sketch_text.stroke-122");var subQ2=sQuery(id+"F0.wireOp",EDGE,"E4.sketch_text.stroke-22");var subQ3=sQuery(id+"F0.wireOp",EDGE,"E4.sketch_text.stroke-94");var subQ4=sQuery(id+"F0.wireOp",EDGE,"E4.sketch_text.stroke-86");var subQ5=sQuery(id+"F0.wireOp",EDGE,"E4.sketch_text.stroke-92");var subQ6=sQuery(id+"F0.wireOp",EDGE,"E4.sketch_text.stroke-75");var subQ7=sQuery(id+"F0.wireOp",EDGE,"E4.sketch_text.stroke-112");var subQ8=sQuery(id+"F0.wireOp",EDGE,"E4.sketch_text.stroke-23");var subQ9=sQuery(id+"F0.wireOp",EDGE,"E4.sketch_text.stroke-114");var subQ10=sQuery(id+"F0.wireOp",EDGE,"E4.sketch_text.stroke-106");var subQ11=sQuery(id+"F0.wireOp",EDGE,"E4.sketch_text.stroke-101");var subQ12=sQuery(id+"F0.wireOp",EDGE,"E4.sketch_text.stroke-105");var subQ13=sQuery(id+"F0.wireOp",EDGE,"E4.sketch_text.stroke-104");var subQ14=sQuery(id+"F0.wireOp",EDGE,"E4.sketch_text.stroke-85");var subQ15=sQuery(id+"F0.wireOp",EDGE,"E4.sketch_text.stroke-84");var subQ16=sQuery(id+"F0.wireOp",EDGE,"E4.sketch_text.stroke-83");var subQ17=sQuery(id+"F0.wireOp",EDGE,"E4.sketch_text.stroke-82");var subQ18=sQuery(id+"F0.wireOp",EDGE,"E4.sketch_text.stroke-170");var subQ19=sQuery(id+"F0.wireOp",EDGE,"E4.sketch_text.stroke-81");var subQ20=sQuery(id+"F0.wireOp",EDGE,"E4.sketch_text.stroke-9");var subQ21=sQuery(id+"F0.wireOp",EDGE,"E4.sketch_text.stroke-169");var subQ22=sQuery(id+"F0.wireOp",EDGE,"E4.sketch_text.stroke-80");var subQ23=sQuery(id+"F0.wireOp",EDGE,"E4.sketch_text.stroke-8");var subQ24=sQuery(id+"F0.wireOp",EDGE,"E4.sketch_text.stroke-27");var subQ25=sQuery(id+"F0.wireOp",EDGE,"E4.sketch_text.stroke-79");var subQ26=sQuery(id+"F0.wireOp",EDGE,"E4.sketch_text.stroke-7");var subQ27=sQuery(id+"F0.wireOp",EDGE,"E4.sketch_text.stroke-18");var subQ28=sQuery(id+"F0.wireOp",EDGE,"E4.sketch_text.stroke-67");var subQ29=sQuery(id+"F0.wireOp",EDGE,"E4.sketch_text.stroke-66");var subQ30=sQuery(id+"F0.wireOp",EDGE,"E4.sketch_text.stroke-65");var subQ31=sQuery(id+"F0.wireOp",EDGE,"E4.sketch_text.stroke-64");var subQ32=sQuery(id+"F0.wireOp",EDGE,"E4.sketch_text.stroke-60");var subQ33=sQuery(id+"F0.wireOp",EDGE,"E4.sketch_text.stroke-148");var subQ34=sQuery(id+"F0.wireOp",EDGE,"E4.sketch_text.stroke-149");var subQ35=sQuery(id+"F0.wireOp",EDGE,"E4.sketch_text.stroke-147");var subQ36=sQuery(id+"F0.wireOp",EDGE,"E4.sketch_text.stroke-55");var subQ37=sQuery(id+"F0.wireOp",EDGE,"E4.sketch_text.stroke-54");var subQ38=sQuery(id+"F0.wireOp",EDGE,"E4.sketch_text.stroke-53");var subQ39=sQuery(id+"F0.wireOp",EDGE,"E4.sketch_text.stroke-52");var subQ40=sQuery(id+"F0.wireOp",EDGE,"E4.sketch_text.stroke-51");var subQ41=sQuery(id+"F0.wireOp",EDGE,"E4.sketch_text.stroke-50");var subQ42=sQuery(id+"F0.wireOp",EDGE,"E4.sketch_text.stroke-49");var subQ43=sQuery(id+"F0.wireOp",EDGE,"E4.sketch_text.stroke-97");var subQ44=sQuery(id+"F0.wireOp",EDGE,"E4.sketch_text.stroke-48");var subQ45=sQuery(id+"F0.wireOp",EDGE,"E4.sketch_text.stroke-47");var subQ46=sQuery(id+"F0.wireOp",EDGE,"E4.sketch_text.stroke-46");var subQ47=sQuery(id+"F0.wireOp",EDGE,"E4.sketch_text.stroke-45");var subQ48=sQuery(id+"F0.wireOp",EDGE,"E4.sketch_text.stroke-134");var subQ49=sQuery(id+"F0.wireOp",EDGE,"E4.sketch_text.stroke-21");var subQ50=sQuery(id+"F0.wireOp",EDGE,"E4.sketch_text.stroke-70");var subQ51=sQuery(id+"F0.wireOp",EDGE,"E4.sketch_text.stroke-141");var subQ52=sQuery(id+"F0.wireOp",EDGE,"E4.sketch_text.stroke-90");var subQ53=sQuery(id+"F0.wireOp",EDGE,"E4.sketch_text.stroke-161");var subQ54=sQuery(id+"F0.wireOp",EDGE,"E4.sketch_text.stroke-41");var subQ55=sQuery(id+"F0.wireOp",EDGE,"E4.sketch_text.stroke-133");var subQ56=sQuery(id+"F0.wireOp",EDGE,"E4.sketch_text.stroke-69");var subQ57=sQuery(id+"F0.wireOp",EDGE,"E4.sketch_text.stroke-140");var subQ58=sQuery(id+"F0.wireOp",EDGE,"E4.sketch_text.stroke-40");var subQ59=sQuery(id+"F0.wireOp",EDGE,"E4.sketch_text.stroke-132");var subQ60=sQuery(id+"F0.wireOp",EDGE,"E4.sketch_text.stroke-59");var subQ61=sQuery(id+"F0.wireOp",EDGE,"E4.sketch_text.stroke-160");var subQ62=sQuery(id+"F0.wireOp",EDGE,"E4.sketch_text.stroke-68");var subQ63=sQuery(id+"F0.wireOp",EDGE,"E4.sketch_text.stroke-139");var subQ64=sQuery(id+"F0.wireOp",EDGE,"E4.sketch_text.stroke-131");var subQ65=sQuery(id+"F0.wireOp",EDGE,"E4.sketch_text.stroke-58");var subQ66=sQuery(id+"F0.wireOp",EDGE,"E4.sketch_text.stroke-159");var subQ67=sQuery(id+"F0.wireOp",EDGE,"E4.sketch_text.stroke-76");var subQ68=sQuery(id+"F0.wireOp",EDGE,"E4.sketch_text.stroke-6");var subQ69=sQuery(id+"F0.wireOp",EDGE,"E4.sketch_text.stroke-78");var subQ70=sQuery(id+"F0.wireOp",EDGE,"E4.sketch_text.stroke-164");var subQ71=sQuery(id+"F0.wireOp",EDGE,"E4.sketch_text.stroke-5");var subQ72=sQuery(id+"F0.wireOp",EDGE,"E4.sketch_text.stroke-163");var subQ73=sQuery(id+"F0.wireOp",EDGE,"E4.sketch_text.stroke-1");var subQ74=sQuery(id+"F0.wireOp",EDGE,"E4.sketch_text.stroke-30");var subQ75=sQuery(id+"F0.wireOp",EDGE,"E4.sketch_text.stroke-119");var subQ76=sQuery(id+"F0.wireOp",EDGE,"E4.sketch_text.stroke-124");var subQ77=sQuery(id+"F0.wireOp",EDGE,"E4.sketch_text.stroke-4");var subQ78=sQuery(id+"F0.wireOp",EDGE,"E4.sketch_text.stroke-162");var subQ79=sQuery(id+"F0.wireOp",EDGE,"E4.sketch_text.stroke-89");var subQ80=sQuery(id+"F0.wireOp",EDGE,"E4.sketch_text.stroke-0");var subQ81=sQuery(id+"F0.wireOp",EDGE,"E4.sketch_text.stroke-118");var subQ82=sQuery(id+"F0.wireOp",EDGE,"E4.sketch_text.stroke-3");var subQ83=sQuery(id+"F0.wireOp",EDGE,"E4.sketch_text.stroke-88");var subQ84=sQuery(id+"F0.wireOp",EDGE,"E4.sketch_text.stroke-117");var subQ85=sQuery(id+"F0.wireOp",EDGE,"E4.sketch_text.stroke-87");var subQ86=sQuery(id+"F0.wireOp",EDGE,"E4.sketch_text.stroke-116");var subQ87=sQuery(id+"F0.wireOp",EDGE,"E4.sketch_text.stroke-61");var subQ88=sQuery(id+"F0.wireOp",EDGE,"E4.sketch_text.stroke-150");var subQ89=sQuery(id+"F0.wireOp",EDGE,"E4.sketch_text.stroke-25");var subQ90=sQuery(id+"F0.wireOp",EDGE,"E4.sketch_text.stroke-167");var subQ91=sQuery(id+"F0.wireOp",EDGE,"E4.sketch_text.stroke-138");var subQ92=sQuery(id+"F0.wireOp",EDGE,"E4.sketch_text.stroke-16");var subQ93=sQuery(id+"F0.wireOp",EDGE,"E4.sketch_text.stroke-15");var subQ94=sQuery(id+"F0.wireOp",EDGE,"E4.sketch_text.stroke-31");var subQ95=sQuery(id+"F0.wireOp",EDGE,"E4.sketch_text.stroke-120");var subQ96=sQuery(id+"F0.wireOp",EDGE,"E4.sketch_text.stroke-17");var subQ97=sQuery(id+"F0.wireOp",EDGE,"E4.sketch_text.stroke-33");var subQ98=sQuery(id+"F0.wireOp",EDGE,"E4.sketch_text.stroke-154");var subQ99=sQuery(id+"F0.wireOp",EDGE,"E4.sketch_text.stroke-77");var subQ100=sQuery(id+"F0.wireOp",EDGE,"E4.sketch_text.stroke-165");var subQ101=sQuery(id+"F0.wireOp",EDGE,"E4.sketch_text.stroke-57");var subQ102=sQuery(id+"F0.wireOp",EDGE,"E4.sketch_text.stroke-56");var subQ103=sQuery(id+"F0.wireOp",EDGE,"E4.sketch_text.stroke-128");var subQ104=sQuery(id+"F0.wireOp",EDGE,"E4.sketch_text.stroke-166");var subQ105=sQuery(id+"F0.wireOp",EDGE,"E4.sketch_text.stroke-63");var subQ106=sQuery(id+"F0.wireOp",EDGE,"E4.sketch_text.stroke-62");var subQ107=sQuery(id+"F0.wireOp",EDGE,"E4.sketch_text.stroke-34");var subQ108=sQuery(id+"F0.wireOp",EDGE,"E4.sketch_text.stroke-19");var subQ109=sQuery(id+"F0.wireOp",EDGE,"E4.sketch_text.stroke-26");var subQ110=sQuery(id+"F0.wireOp",EDGE,"E4.sketch_text.stroke-127");var subQ111=sQuery(id+"F0.wireOp",EDGE,"E4.sketch_text.stroke-121");var subQ112=sQuery(id+"F0.wireOp",EDGE,"E4.sketch_text.stroke-73");var subQ113=sQuery(id+"F0.wireOp",EDGE,"E4.sketch_text.stroke-35");var subQ114=sQuery(id+"F0.wireOp",EDGE,"E4.sketch_text.stroke-20");var subQ115=sQuery(id+"F0.wireOp",EDGE,"E4.sketch_text.stroke-71");var subQ116=sQuery(id+"F0.wireOp",EDGE,"E2");var subQ117=sQuery(id+"F0.wireOp",EDGE,"E4.sketch_text.stroke-99");var subQ118=sQuery(id+"F0.wireOp",EDGE,"E4.sketch_text.stroke-36");var subQ119=sQuery(id+"F0.wireOp",EDGE,"E4.sketch_text.stroke-108");var subQ120=sQuery(id+"F0.wireOp",EDGE,"E4.sketch_text.stroke-72");var subQ121=sQuery(id+"F0.wireOp",EDGE,"E3");var subQ122=sQuery(id+"F0.wireOp",EDGE,"E4.sketch_text.stroke-100");var subQ123=sQuery(id+"F0.wireOp",EDGE,"E4.sketch_text.stroke-171");var subQ124=sQuery(id+"F0.wireOp",EDGE,"E4.sketch_text.stroke-28");var subQ125=sQuery(id+"F0.wireOp",EDGE,"E4.sketch_text.stroke-129");var subQ126=sQuery(id+"F0.wireOp",EDGE,"E4.sketch_text.stroke-37");var subQ127=sQuery(id+"F0.wireOp",EDGE,"E4.sketch_text.stroke-109");var subQ128=sQuery(id+"F0.wireOp",EDGE,"E4.sketch_text.stroke-107");var subQ129=sQuery(id+"F0.wireOp",EDGE,"E4.sketch_text.stroke-91");var subQ130=sQuery(id+"F0.wireOp",EDGE,"E4.sketch_text.stroke-102");var subQ131=sQuery(id+"F0.wireOp",EDGE,"E4.sketch_text.stroke-29");var subQ132=sQuery(id+"F0.wireOp",EDGE,"E4.sketch_text.stroke-130");var subQ133=sQuery(id+"F0.wireOp",EDGE,"E4.sketch_text.stroke-38");var subQ134=sQuery(id+"F0.wireOp",EDGE,"E4.sketch_text.stroke-110");var subQ135=sQuery(id+"F0.wireOp",EDGE,"E4.sketch_text.stroke-74");var subQ136=sQuery(id+"F0.wireOp",EDGE,"E4.sketch_text.stroke-103");var subQ137=sQuery(id+"F0.wireOp",EDGE,"E4.sketch_text.stroke-39");var subQ138=sQuery(id+"F0.wireOp",EDGE,"E4.sketch_text.stroke-111");var subQ139=sQuery(id+"F0.wireOp",EDGE,"E4.sketch_text.stroke-24");var subQ140=sQuery(id+"F0.wireOp",EDGE,"E4.sketch_text.stroke-32");var subQ141=sQuery(id+"F0.wireOp",EDGE,"E4.sketch_text.stroke-93");var subQ142=sQuery(id+"F0.wireOp",EDGE,"E4.sketch_text.stroke-153");var subQ143=sQuery(id+"F0.wireOp",EDGE,"E0");var subQ144=sQuery(id+"F0.wireOp",EDGE,"E4.sketch_text.stroke-95");var subQ145=sQuery(id+"F0.wireOp",EDGE,"E4.sketch_text.stroke-96");var subQ146=sQuery(id+"F0.wireOp",EDGE,"E1");var subQ147=sQuery(id+"F0.wireOp",EDGE,"E4.sketch_text.stroke-98");var subQ148=sQuery(id+"F0.wireOp",EDGE,"E4.sketch_text.stroke-168");var subQ149=sQuery(id+"F0.wireOp",EDGE,"E4.sketch_text.stroke-10");var subQ150=sQuery(id+"F0.wireOp",EDGE,"E4.sketch_text.stroke-11");var subQ151=sQuery(id+"F0.wireOp",EDGE,"E4.sketch_text.stroke-113");var subQ152=sQuery(id+"F0.wireOp",EDGE,"E4.sketch_text.stroke-12");var subQ153=sQuery(id+"F0.wireOp",EDGE,"E4.sketch_text.stroke-13");var subQ154=sQuery(id+"F0.wireOp",EDGE,"E4.sketch_text.stroke-14");var subQ155=sQuery(id+"F0.wireOp",EDGE,"E4.sketch_text.stroke-115");var subQ156=sQuery(id+"F0.wireOp",EDGE,"E4.sketch_text.stroke-123");var subQ157=sQuery(id+"F0.wireOp",EDGE,"E4.sketch_text.stroke-125");var subQ158=sQuery(id+"F0.wireOp",EDGE,"E4.sketch_text.stroke-126");var subQ159=sQuery(id+"F0.wireOp",EDGE,"E4.sketch_text.stroke-137");var subQ160=sQuery(id+"F0.wireOp",EDGE,"E4.sketch_text.stroke-142");var subQ161=sQuery(id+"F0.wireOp",EDGE,"E4.sketch_text.stroke-42");var subQ162=sQuery(id+"F0.wireOp",EDGE,"E4.sketch_text.stroke-143");var subQ163=sQuery(id+"F0.wireOp",EDGE,"E4.sketch_text.stroke-43");var subQ164=sQuery(id+"F0.wireOp",EDGE,"E4.sketch_text.stroke-144");var subQ165=sQuery(id+"F0.wireOp",EDGE,"E4.sketch_text.stroke-44");var subQ166=sQuery(id+"F0.wireOp",EDGE,"E4.sketch_text.stroke-145");var subQ167=sQuery(id+"F0.wireOp",EDGE,"E4.sketch_text.stroke-146");var subQ168=sQuery(id+"F0.wireOp",EDGE,"E4.sketch_text.stroke-151");var subQ169=sQuery(id+"F0.wireOp",EDGE,"E4.sketch_text.stroke-135");var subQ170=sQuery(id+"F0.wireOp",EDGE,"E4.sketch_text.stroke-152");var subQ171=sQuery(id+"F0.wireOp",EDGE,"E4.sketch_text.stroke-136");var subQ172=sQuery(id+"F0.wireOp",EDGE,"E4.sketch_text.stroke-155");var subQ173=sQuery(id+"F0.wireOp",EDGE,"E4.sketch_text.stroke-156");var subQ174=sQuery(id+"F0.wireOp",EDGE,"E4.sketch_text.stroke-157");var subQ175=sQuery(id+"F0.wireOp",EDGE,"E4.sketch_text.stroke-158");var subQ176=sQuery(id+"F0.wireOp",EDGE,"E4.sketch_text.stroke-172");var subQ177=sQuery(id+"F0.wireOp",EDGE,"E4.sketch_text.stroke-173");var subQ178=sQuery(id+"F0.wireOp",EDGE,"E4.sketch_text.stroke-174");Q0=makeQuery(id+"F17.boolean.opBoolean","SPLIT",FACE,{"disambiguationData":[TD([makeQuery(id+"F2.opExtrude","SWEPT_FACE",FACE,{"disambiguationData":[OSD([subQ143])]})])],"derivedFrom":makeQuery(id+"F2.opExtrude","CAP_FACE",FACE,{"disambiguationData":[OSD([subQ143,subQ146,subQ116,subQ121,subQ80,subQ73,subQ0,subQ82,subQ77,subQ71,subQ68,subQ26,subQ23,subQ20,subQ149,subQ150,subQ152,subQ153,subQ154,subQ93,subQ92,subQ96,subQ27,subQ108,subQ114,subQ49,subQ2,subQ8,subQ139,subQ89,subQ109,subQ24,subQ124,subQ131,subQ74,subQ94,subQ140,subQ97,subQ107,subQ113,subQ118,subQ126,subQ133,subQ137,subQ58,subQ54,subQ161,subQ163,subQ165,subQ47,subQ46,subQ45,subQ44,subQ42,subQ41,subQ40,subQ39,subQ38,subQ37,subQ36,subQ102,subQ101,subQ65,subQ60,subQ32,subQ87,subQ106,subQ105,subQ31,subQ30,subQ29,subQ28,subQ62,subQ56,subQ50,subQ115,subQ120,subQ112,subQ135,subQ6,subQ67,subQ99,subQ69,subQ25,subQ22,subQ19,subQ17,subQ16,subQ15,subQ14,subQ4,subQ85,subQ83,subQ79,subQ52,subQ129,subQ5,subQ141,subQ3,subQ144,subQ145,subQ43,subQ147,subQ117,subQ122,subQ11,subQ130,subQ136,subQ13,subQ12,subQ10,subQ128,subQ119,subQ127,subQ134,subQ138,subQ7,subQ151,subQ9,subQ155,subQ86,subQ84,subQ81,subQ75,subQ95,subQ111,subQ1,subQ156,subQ76,subQ157,subQ158,subQ110,subQ103,subQ125,subQ132,subQ64,subQ59,subQ55,subQ48,subQ169,subQ171,subQ159,subQ91,subQ63,subQ57,subQ51,subQ160,subQ162,subQ164,subQ166,subQ167,subQ35,subQ33,subQ34,subQ88,subQ168,subQ170,subQ142,subQ98,subQ172,subQ173,subQ174,subQ175,subQ66,subQ61,subQ53,subQ78,subQ72,subQ70,subQ100,subQ104,subQ90,subQ148,subQ21,subQ18,subQ123,subQ176,subQ177,subQ178])],"isStart":false})});}
            var sketch = newSketch(context, id + "F22", { "sketchPlane" : qUnion([Q0])});
            skCircle(sketch, "E306", {"center": v(-90.34, 9.93) * mm, "radius": 2.7 * mm});
            skPoint(sketch, "E306.centerSnap0", {"position": v(-93.88, 9.93) * mm});
            skLineSegment(sketch, "E307", {"start": v(-28.9, 0.67) * mm, "end": v(-37.58, 0.67) * mm});
            skLineSegment(sketch, "E308", {"start": v(-37.58, 0.67) * mm, "end": v(-37.58, 2.63) * mm});
            skLineSegment(sketch, "E309", {"start": v(-37.58, 2.63) * mm, "end": v(-28.9, 2.63) * mm});
            skLineSegment(sketch, "E310", {"start": v(-35.19, 5.4) * mm, "end": v(-35.19, 2.63) * mm});
            skSolve(sketch);
        }
        {
            var Q0;
            Q0=makeQuery(id+"F22.imprint","IMPRINT",FACE,{"disambiguationData":[TD([[makeQuery(id+"F22.imprint","IMPRINT",EDGE,{"derivedFrom":sQuery(id+"F22.wireOp",EDGE,"E306")}),1.0]])]});
            extrude(context, id + "F23", {"entities" : qUnion([Q0]), "operationType" : NewBodyOperationType.REMOVE, "endBound" : BoundingType.THROUGH_ALL, "oppositeDirection" : true, "depth" : 25.4 * mm});
        }
    });
